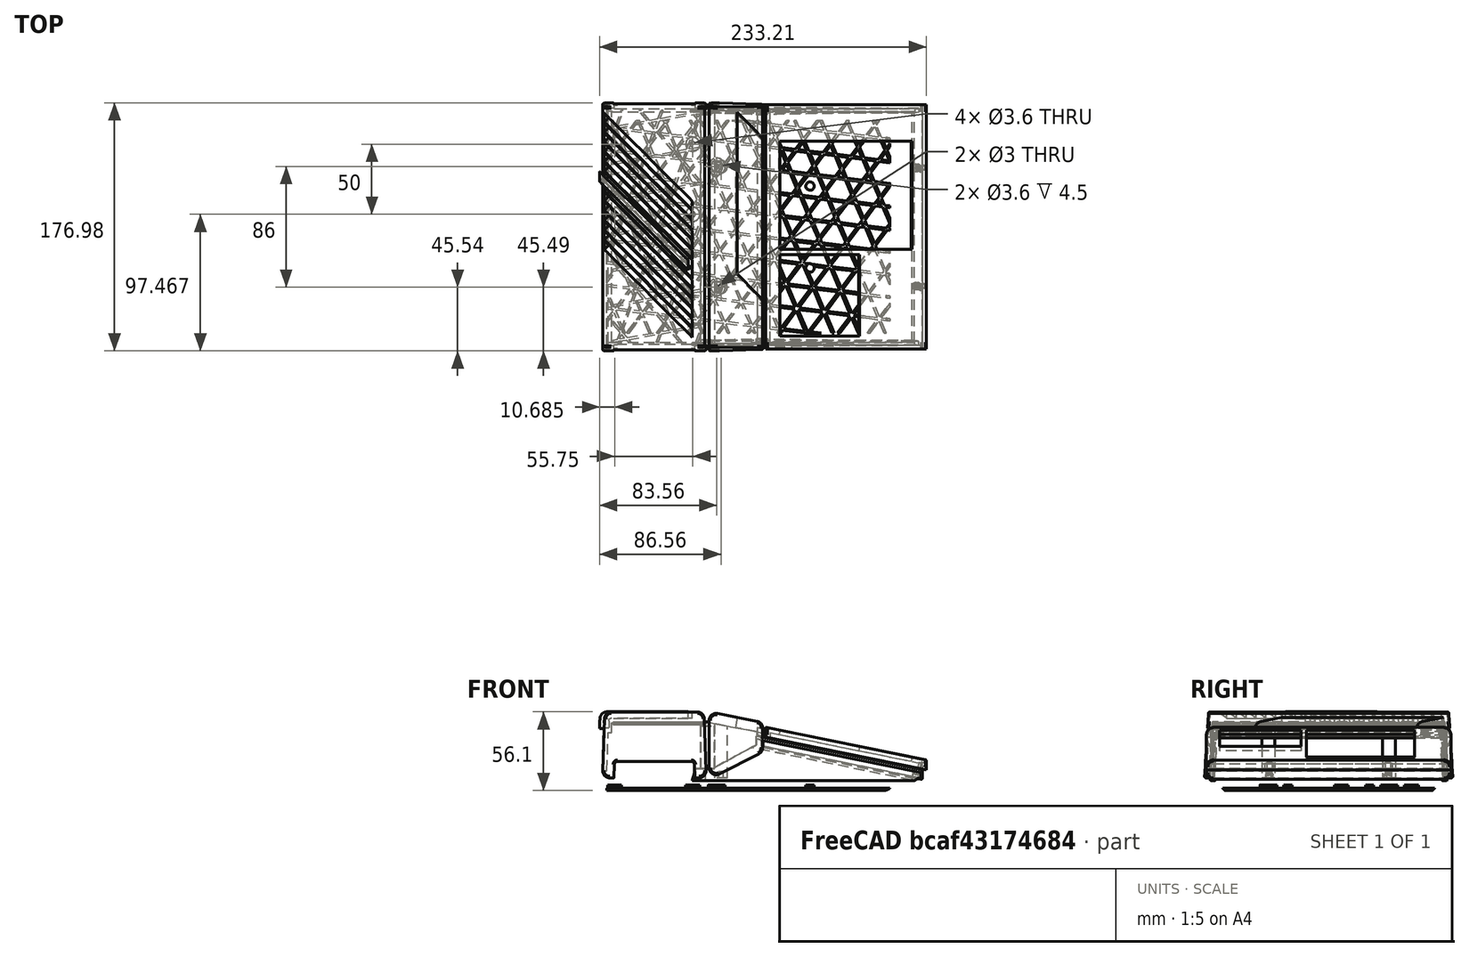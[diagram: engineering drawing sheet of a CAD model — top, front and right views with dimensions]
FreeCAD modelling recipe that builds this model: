
FCSTD DOCUMENT  (FreeCAD 0.20R29177 +426 (Git))
Label: SidecarXE85-case
License: All rights reserved
LicenseURL: http://en.wikipedia.org/wiki/All_rights_reserved
objects: Part::FeaturePython×61, Sketcher::SketchObject×58, PartDesign::Plane×37, PartDesign::Pad×26, PartDesign::Pocket×26, PartDesign::Body×23, Surface::GeomFillSurface×22, PartDesign::FeatureBase×18, PartDesign::Line×12, Part::Part2DObjectPython×10, Part::Compound×8, Surface::Sections×8, PartDesign::Fillet×7, PartDesign::LinearPattern×6, PartDesign::ShapeBinder×5, Surface::Filling×3, PartDesign::Draft×2, Part::Feature×2, Part::Offset×2, Part::Fuse×2, +13 more types
note: 410 computed .brp shape members not serialized (recipe doc carries the construction recipe); baked Part::Feature solids carry a one-line shape summary decoded from their .brp

FEATURE [Sketcher::SketchObject] Sketch  label="SketchBack"
  FullyConstrained = true
  MapMode = 5
  Placement = pos=(0,0,0) rot=(1,0,0;1.5708rad)
  Support = -> [XZ_Plane]
  sketch-geometry (4):
    g0: LineSegment StartX=0 StartY=12 StartZ=0 EndX=1.5 EndY=59 EndZ=0
    g1: LineSegment StartX=1.5 StartY=59 StartZ=0 EndX=72.5 EndY=59 EndZ=0
    g2: LineSegment StartX=72.5 StartY=59 StartZ=0 EndX=74 EndY=12 EndZ=0
    g3: LineSegment StartX=74 StartY=12 StartZ=0 EndX=0 EndY=12 EndZ=0
  constraints (12):
    c: PointOnObject(g0,g-2)
    c: Coincident(g0,g1)
    c: Horizontal(g1)
    c: Coincident(g1,g2)
    c: Coincident(g2,g3)
    c: Coincident(g3,g0)
    c: Horizontal(g3)
    c: DistanceX(g1,g1) = 71
    c: DistanceY(g0,g0) = 47
    c: DistanceY(g-1,g0) = 12
    c: DistanceX(g0,g0) = 1.5
    c: DistanceX(g1,g2) = 1.5
FEATURE [PartDesign::Pad] Pad  label="ExtrudeBack"
  Direction = (0,-1,-2e-16)
  Length = 177.1
  Length2 = 10
  Placement = pos=(0,0,0) rot=(1,0,0;1.5708rad)
  Profile = -> Sketch
  ReferenceAxis = -> Sketch [N_Axis]
  Type = 0
  expr: Length = <<Params>>.Width + 2.7
FEATURE [Spreadsheet::Sheet] Spreadsheet  label="Params"
  cells = A1=Width; B1(Width)=174.4; A2=BigFillet; B2(BigFillet)=5; A3=Walls; B3(Walls)=3
FEATURE [PartDesign::Fillet] Fillet  label="BigFilletBack"
  Base = -> Pad [Edge1,Edge2,Edge5,Edge8]
  BaseFeature = -> Pad
  Placement = pos=(0,0,0) rot=(1,0,0;1.5708rad)
  Radius = 5
  SupportTransform = false
  UseAllEdges = false
  expr: Radius = <<Params>>.BigFillet
FEATURE [Sketcher::SketchObject] Sketch001  label="SketchMiddle"
  FullyConstrained = true
  MapMode = 5
  Placement = pos=(0,0,0) rot=(1,0,0;1.5708rad)
  Support = -> [XZ_Plane001]
  sketch-geometry (4):
    g0: LineSegment StartX=76 StartY=11 StartZ=0 EndX=76 EndY=59 EndZ=0
    g1: LineSegment StartX=76 StartY=59 StartZ=0 EndX=114.286 EndY=51.5741 EndZ=0
    g2: LineSegment StartX=114.286 StartY=51.5741 StartZ=0 EndX=114.286 EndY=30.5741 EndZ=0
    g3: LineSegment StartX=114.286 StartY=30.5741 StartZ=0 EndX=76 EndY=11 EndZ=0
  constraints (12):
    c: Vertical(g0)
    c: Coincident(g0,g1)
    c: Coincident(g1,g2)
    c: Vertical(g2)
    c: Coincident(g2,g3)
    c: Coincident(g3,g0)
    c: Distance(g0,g1) = 39
    c: DistanceY(g2,g1) = 21
    c: Distance(g2,g0) = 43
    c: DistanceY(g0,g0) = 48
    c: DistanceY(g-1,g0) = 11
    c: DistanceX(g-1,g0) = 76
FEATURE [PartDesign::Pad] Pad001  label="ExtrudeMiddle"
  Direction = (0,-1,-2e-16)
  Length = 177.1
  Length2 = 10
  Placement = pos=(0,0,0) rot=(1,0,0;1.5708rad)
  Profile = -> Sketch001
  ReferenceAxis = -> Sketch001 [N_Axis]
  Type = 0
  expr: Length = <<Params>>.Width + 2.7
FEATURE [PartDesign::Fillet] Fillet001  label="BigFilletMiddle"
  Base = -> Pad001 [Edge1,Edge2,Edge5,Edge8]
  BaseFeature = -> Pad001
  Placement = pos=(0,0,0) rot=(1,0,0;1.5708rad)
  Radius = 5
  SupportTransform = false
  UseAllEdges = false
  expr: Radius = <<Params>>.BigFillet
FEATURE [Sketcher::SketchObject] Sketch002  label="SketchKeyboardTop"
  FullyConstrained = true
  MapMode = 5
  Placement = pos=(0,0,0) rot=(1,0,0;1.5708rad)
  Support = -> [XZ_Plane002]
  sketch-geometry (4):
    g0: LineSegment StartX=116.5 StartY=41 StartZ=0 EndX=116.5 EndY=48 EndZ=0
    g1: LineSegment StartX=116.5 StartY=48 StartZ=0 EndX=231.151 EndY=24.674 EndZ=0
    g2: LineSegment StartX=231.151 StartY=24.674 StartZ=0 EndX=231.151 EndY=17.674 EndZ=0
    g3: LineSegment StartX=231.151 StartY=17.674 StartZ=0 EndX=116.5 EndY=41 EndZ=0
  constraints (12):
    c: Vertical(g0)
    c: Coincident(g0,g1)
    c: Coincident(g1,g2)
    c: Vertical(g2)
    c: Coincident(g2,g3)
    c: Coincident(g3,g0)
    c: Parallel(g1,g3)
    c: Angle(g1,g-1) = 0.200713
    c: DistanceY(g0,g0) = 7
    c: Distance(g0,g2) = 117
    c: DistanceX(g-1,g0) = 116.5
    c: DistanceY(g-1,g0) = 41
FEATURE [PartDesign::Pad] Pad002  label="ExtrudeKeyboardTop"
  Direction = (0,-1,-2e-16)
  Length = 174.4
  Length2 = 10
  Placement = pos=(0,0,0) rot=(1,0,0;1.5708rad)
  Profile = -> Sketch002
  ReferenceAxis = -> Sketch002 [N_Axis]
  Type = 0
  expr: Length = <<Params>>.Width
FEATURE [PartDesign::Fillet] Fillet002  label="BigFilletKeyboardTop"
  Base = -> Pad002 [Edge7,Edge6]
  BaseFeature = -> Pad002
  Placement = pos=(0,0,0) rot=(1,0,0;1.5708rad)
  Radius = 5
  SupportTransform = false
  UseAllEdges = false
  expr: Radius = <<Params>>.BigFillet
FEATURE [PartDesign::Line] DatumLine  label="BottomLeftDatumLine"
  AttacherType = Attacher::AttachEngineLine
  Length = 20
  MapMode = 29
  Placement = pos=(0,-177.1,12) rot=(0.57735,-0.57735,-0.57735;2.0944rad)
  ResizeMode = 0
  Support = -> [Fillet]
FEATURE [PartDesign::Line] DatumLine001  label="BottomRightDatumLine"
  AttacherType = Attacher::AttachEngineLine
  Length = 20
  MapMode = 29
  Placement = pos=(0,2.7e-15,12) rot=(0.57735,-0.57735,-0.57735;2.0944rad)
  ResizeMode = 0
  Support = -> [Fillet]
FEATURE [PartDesign::Line] DatumLine002  label="TopLeftDatumLine"
  AttacherType = Attacher::AttachEngineLine
  AttachmentOffset = pos=(2.7,0,0) rot=(0,0,1;0rad)
  Length = 20
  MapMode = 29
  Placement = pos=(0,-174.4,59) rot=(0.57735,0.57735,0.57735;2.0944rad)
  ResizeMode = 0
  Support = -> [Fillet]
FEATURE [PartDesign::Line] DatumLine003  label="TopRightDatumLine"
  AttacherType = Attacher::AttachEngineLine
  AttachmentOffset = pos=(-2.7,0,0) rot=(0,0,1;0rad)
  Length = 20
  MapMode = 29
  Placement = pos=(0,-2.7,59) rot=(0.57735,0.57735,0.57735;2.0944rad)
  ResizeMode = 0
  Support = -> [Fillet]
FEATURE [PartDesign::Plane] DatumPlane  label="LeftCutDatumPlane"
  Length = 287.424
  MapMode = 13
  Placement = pos=(0.333333,-175.3,43.3333) rot=(0,0.727101,0.68653;3.14159rad)
  ResizeMode = 0
  Support = -> [DatumLine002,DatumLine]
  Width = 126.721
FEATURE [PartDesign::Plane] DatumPlane001  label="RightCutDatumPlane"
  Length = 287.424
  MapMode = 13
  Placement = pos=(0.333333,-1.8,43.3333) rot=(0,0.68653,0.727101;3.14159rad)
  ResizeMode = 0
  Support = -> [DatumLine003,DatumLine001]
  Width = 126.721
FEATURE [PartDesign::Draft] Draft  label="DraftBack"
  Angle = 3.5
  Base = -> Fillet [Face5,Face2]
  BaseFeature = -> Fillet
  NeutralPlane = -> Fillet [Face6]
  Placement = pos=(0,0,0) rot=(1,0,0;1.5708rad)
  Reversed = true
  SupportTransform = false
FEATURE [PartDesign::Plane] DatumPlane002  label="BottomDatumPlane"
  Length = 60
  MapMode = 5
  Placement = pos=(0,2.7e-15,12) rot=(1,0,0;3.14159rad)
  ResizeMode = 0
  Support = -> [Draft]
  Width = 60
FEATURE [PartDesign::Draft] Draft001  label="DraftMiddle"
  Angle = 3.5
  Base = -> Fillet001 [Face2,Face5]
  BaseFeature = -> Fillet001
  NeutralPlane = -> DatumPlane002
  Placement = pos=(0,0,0) rot=(1,0,0;1.5708rad)
  Reversed = true
  SupportTransform = false
FEATURE [PartDesign::Thickness] Thickness
  Base = -> Fillet002 [Face7]
  BaseFeature = -> Fillet002
  Intersection = false
  Join = 1
  Mode = 0
  Reversed = true
  SupportTransform = false
  Value = 3
  expr: Value = <<Params>>.Walls
FEATURE [Sketcher::SketchObject] Sketch003  label="BackCutSchema"
  ExternalGeometry = -> [Draft]
  FullyConstrained = true
  MapMode = 5
  Placement = pos=(-0.382589,0,0.0122103) rot=(-0.695738,0,0.718296;3.14159rad)
  Support = -> [Draft]
  expr: Constraints[4] = 90 - 3.5
  expr: Constraints[5] = 90 - 3.5
  expr: Constraints[6] = <<Params>>.Width - 2 * <<Params>>.Walls - 4
  sketch-geometry (6):
    g0: LineSegment StartX=0 StartY=3.22001 StartZ=0 EndX=-51.1749 EndY=6.35 EndZ=0
    g1: LineSegment StartX=-51.1749 StartY=170.75 StartZ=0 EndX=0 EndY=173.88 EndZ=0
    g2: LineSegment StartX=0 StartY=173.88 StartZ=0 EndX=0 EndY=3.22001 EndZ=0
    g3: LineSegment StartX=-54.1749 StartY=174.521 StartZ=0 EndX=-51.1749 EndY=170.75 EndZ=0
    g4: LineSegment StartX=-51.1749 StartY=6.35 StartZ=0 EndX=-54.1749 EndY=2.57859 EndZ=0
    g5: LineSegment StartX=-51.1749 StartY=170.75 StartZ=0 EndX=-51.1749 EndY=6.35 EndZ=0
  constraints (16):
    c: PointOnObject(g0,g-2)
    c: PointOnObject(g1,g-2)
    c: Coincident(g1,g2)
    c: Coincident(g2,g0)
    c: Angle(g1,g2) = 1.50971
    c: Angle(g2,g0) = 1.50971
    c: DistanceY(g0,g1) = 164.4
    c: Coincident(g3,g-3)
    c: Coincident(g3,g1)
    c: Coincident(g4,g0)
    c: Coincident(g4,g-4)
    c: Equal(g3,g4)
    c: Coincident(g5,g1)
    c: Coincident(g5,g0)
    c: Vertical(g5)
    c: DistanceX(g3,g1) = 3
FEATURE [PartDesign::Pocket] Pocket  label="BackCut"
  BaseFeature = -> Draft
  Direction = (1,0,0)
  Length = 0
  Length2 = 5
  Placement = pos=(0,0,0) rot=(1,0,0;1.5708rad)
  Profile = -> Sketch003
  ReferenceAxis = -> Sketch003 [N_Axis]
  Type = 3
  UpToFace = -> Draft [Face10]
  UseCustomVector = true
FEATURE [PartDesign::Plane] DatumPlane003  label="BackVerticalDatumPlane"
  Length = 329.861
  MapMode = 13
  Placement = pos=(1.77559,-2.74097,9.71983) rot=(0.058644,0.617116,0.784684;2.99273rad)
  ResizeMode = 0
  Support = -> [Pocket,Z_Axis]
  Width = 180.015
FEATURE [Sketcher::SketchObject] Sketch004  label="KeyboardHoleSketch"
  ExternalGeometry = -> [Thickness]
  FullyConstrained = true
  MapMode = 5
  Placement = pos=(14.0081,0,68.8522) rot=(0,1,0;0.200713rad)
  Support = -> [Thickness]
  expr: Constraints[16] = 19.05 * 4 + 1
  expr: Constraints[17] = 19.05 * 3 + 1
  expr: Constraints[18] = 19.05 / 4 - 1
  expr: Constraints[20] = 19.05 * 5 + 1
  expr: Constraints[21] = 19.05 * 3 + 1
  sketch-geometry (10):
    g0: LineSegment StartX=114.742 StartY=-25.94 StartZ=0 EndX=210.992 EndY=-25.94 EndZ=0
    g1: LineSegment StartX=210.992 StartY=-25.94 StartZ=0 EndX=210.992 EndY=-103.14 EndZ=0
    g2: LineSegment StartX=210.992 StartY=-103.14 StartZ=0 EndX=114.742 EndY=-103.14 EndZ=0
    g3: LineSegment StartX=114.742 StartY=-103.14 StartZ=0 EndX=114.742 EndY=-25.94 EndZ=0
    g4: LineSegment StartX=114.742 StartY=-106.902 StartZ=0 EndX=172.892 EndY=-106.902 EndZ=0
    g5: LineSegment StartX=172.892 StartY=-106.902 StartZ=0 EndX=172.892 EndY=-165.052 EndZ=0
    g6: LineSegment StartX=172.892 StartY=-165.052 StartZ=0 EndX=114.742 EndY=-165.052 EndZ=0
    g7: LineSegment StartX=114.742 StartY=-165.052 StartZ=0 EndX=114.742 EndY=-106.902 EndZ=0
    g8: LineSegment StartX=114.742 StartY=-25.94 StartZ=0 EndX=114.742 EndY=-5 EndZ=0
    g9: LineSegment StartX=114.742 StartY=-165.052 StartZ=0 EndX=114.742 EndY=-169.4 EndZ=0
  constraints (30):
    c: Coincident(g0,g1)
    c: Coincident(g1,g2)
    c: Coincident(g2,g3)
    c: Coincident(g3,g0)
    c: Horizontal(g0)
    c: Horizontal(g2)
    c: Vertical(g1)
    c: Vertical(g3)
    c: Coincident(g4,g5)
    c: Coincident(g5,g6)
    c: Coincident(g6,g7)
    c: Coincident(g7,g4)
    c: Horizontal(g4)
    c: Horizontal(g6)
    c: Vertical(g5)
    c: Vertical(g7)
    c: DistanceY(g3,g3) = 77.2
    c: DistanceY(g7,g7) = 58.15
    c: DistanceY(g4,g2) = 3.7625
    c: PointOnObject(g4,g3)
    c: DistanceX(g0,g0) = 96.25
    c: DistanceX(g4,g4) = 58.15
    c: Coincident(g8,g0)
    c: PointOnObject(g8,g-4)
    c: Vertical(g8)
    c: Coincident(g9,g6)
    c: PointOnObject(g9,g-5)
    c: Vertical(g9)
    c: DistanceY(g0,g8) = 20.94
    c: DistanceX(g0,g-4) = 10.6
FEATURE [PartDesign::Pocket] Pocket001  label="KeyHoles"
  BaseFeature = -> Thickness
  Direction = (-0.199368,0,-0.979925)
  Length = 5
  Length2 = 5
  Profile = -> Sketch004
  ReferenceAxis = -> Sketch004 [N_Axis]
  Type = 0
FEATURE [Sketcher::SketchObject] Sketch005  label="MiddlePocketSketch"
  ExternalGeometry = -> [Draft001]
  FullyConstrained = true
  MapMode = 5
  Placement = pos=(76,0,0) rot=(0.707107,0,-0.707107;3.14159rad)
  Support = -> [Draft001]
  expr: Constraints[15] = <<Params>>.Walls / cos(10)
  sketch-geometry (6):
    g0: LineSegment StartX=-1.54556 StartY=174.608 StartZ=0 EndX=-51.5456 EndY=171.55 EndZ=0
    g1: LineSegment StartX=-51.5456 StartY=171.55 StartZ=0 EndX=-51.5456 EndY=5.5501 EndZ=0
    g2: LineSegment StartX=-51.5456 StartY=5.5501 StartZ=0 EndX=-1.54556 EndY=2.49197 EndZ=0
    g3: LineSegment StartX=-1.54556 StartY=2.49197 StartZ=0 EndX=-1.54556 EndY=174.608 EndZ=0
    g4: LineSegment StartX=-57.8456 StartY=174.296 StartZ=0 EndX=-51.5456 EndY=171.55 EndZ=0
    g5: LineSegment StartX=-51.5456 StartY=5.5501 StartZ=0 EndX=-57.8456 EndY=2.80403 EndZ=0
  constraints (16):
    c: Coincident(g0,g1)
    c: Vertical(g1)
    c: Coincident(g1,g2)
    c: Coincident(g2,g3)
    c: Coincident(g3,g0)
    c: Vertical(g3)
    c: Parallel(g0,g-3)
    c: Parallel(g-4,g2)
    c: Coincident(g4,g-5)
    c: Coincident(g4,g0)
    c: Coincident(g5,g1)
    c: Coincident(g5,g-5)
    c: Equal(g4,g5)
    c: DistanceX(g4,g0) = 6.3
    c: DistanceX(g0,g0) = 50
    c: DistanceY(g0,g-3) = 3.04628
FEATURE [PartDesign::Pocket] Pocket002  label="MiddlePocket"
  AlongSketchNormal = false
  BaseFeature = -> Draft001
  Direction = (-0.98,0,0.19)
  Length = 0
  Length2 = 5
  Placement = pos=(0,0,0) rot=(1,0,0;1.5708rad)
  Profile = -> Sketch005
  ReferenceAxis = -> Sketch005 [N_Axis]
  Reversed = true
  Type = 3
  UpToFace = -> Draft001 [Face10]
  UseCustomVector = true
FEATURE [PartDesign::Body] Body001  label="Middle"
  Group = -> [Sketch001,Pad001,Fillet001,DatumPlane002,Draft001,Sketch005,Pocket002]
  Origin = -> Origin001
  Tip = -> Pocket002
FEATURE [PartDesign::Plane] DatumPlane004  label="SevenMmBelowTopDatumPlane"
  AttachmentOffset = pos=(0,0,-7) rot=(0,0,1;0rad)
  Length = 301.649
  MapMode = 5
  Placement = pos=(0,1.29e-14,58.161) rot=(1,0,0;3.14159rad)
  ResizeMode = 0
  Support = -> [Pocket]
  Width = 247.533
FEATURE [PartDesign::Plane] DatumPlane007
  AttachmentOffset = pos=(0,0,-1.35) rot=(0,0,1;0rad)
  Length = 311.586
  MapMode = 5
  Placement = pos=(13.739,0,67.5293) rot=(0,1,0;0.200713rad)
  ResizeMode = 0
  Support = -> [Pocket001]
  Width = 245.423
FEATURE [PartDesign::Line] DatumLine007
  AttacherType = Attacher::AttachEngineLine
  Length = 20
  MapMode = 29
  Placement = pos=(116.5,0,48) rot=(1,0,0;1.5708rad)
  ResizeMode = 0
  Support = -> [Pocket001]
FEATURE [PartDesign::Line] DatumLine008
  AttacherType = Attacher::AttachEngineLine
  Length = 20
  MapMode = 29
  Placement = pos=(14.0081,-169.4,68.8522) rot=(0.612272,0.612272,0.500247;2.2139rad)
  ResizeMode = 0
  Support = -> [Pocket001]
FEATURE [PartDesign::Line] DatumLine009
  AttacherType = Attacher::AttachEngineLine
  Length = 20
  MapMode = 29
  Placement = pos=(14.0081,-5,68.8522) rot=(0.612272,0.612272,0.500247;2.2139rad)
  ResizeMode = 0
  Support = -> [Pocket001]
FEATURE [Sketcher::SketchObject] Sketch009  label="ConnectionKeyboardMiddleSketch"
  ExternalGeometry = -> [DatumLine009,DatumLine008,DatumLine007]
  FullyConstrained = true
  MapMode = 5
  Placement = pos=(13.739,0,67.5293) rot=(0,1,0;0.200713rad)
  Support = -> [DatumPlane007]
  expr: Constraints[9] = <<Params>>.Width - 6
  sketch-geometry (7):
    g0: LineSegment StartX=106.592 StartY=-3 StartZ=0 EndX=98.5916 EndY=-3 EndZ=0
    g1: LineSegment StartX=98.5916 StartY=-3 StartZ=0 EndX=98.5916 EndY=-171.4 EndZ=0
    g2: LineSegment StartX=98.5916 StartY=-171.4 StartZ=0 EndX=106.592 EndY=-171.4 EndZ=0
    g3: LineSegment StartX=106.592 StartY=-171.4 StartZ=0 EndX=106.592 EndY=-3 EndZ=0
    g4: GeomPoint X=104.592 Y=-169.4 Z=0
    g5: LineSegment StartX=104.592 StartY=-169.4 StartZ=0 EndX=106.592 EndY=-171.4 EndZ=0
    g6: LineSegment StartX=104.592 StartY=-5 StartZ=0 EndX=106.592 EndY=-3 EndZ=0
  constraints (19):
    c: Coincident(g0,g1)
    c: Coincident(g1,g2)
    c: Coincident(g2,g3)
    c: Coincident(g3,g0)
    c: Horizontal(g0)
    c: Horizontal(g2)
    c: Vertical(g1)
    c: Vertical(g3)
    c: DistanceX(g0,g0) = 8
    c: DistanceY(g3,g3) = 168.4
    c: PointOnObject(g4,g-5)
    c: PointOnObject(g4,g-4)
    c: Coincident(g5,g4)
    c: Coincident(g5,g2)
    c: Coincident(g6,g0)
    c: Equal(g5,g6)
    c: PointOnObject(g6,g-3)
    c: PointOnObject(g6,g-5)
    c: DistanceX(g4,g2) = 2
FEATURE [PartDesign::Pad] Pad006  label="ConnectionKeyboardMiddle"
  BaseFeature = -> Pocket001
  Direction = (0,0,1)
  Length = 5.5
  Length2 = 10
  Profile = -> Sketch009
  ReferenceAxis = -> Sketch009 [N_Axis]
  Reversed = true
  Type = 0
  UseCustomVector = true
FEATURE [PartDesign::Body] Body002  label="KeyboardTop"
  Group = -> [Sketch002,Pad002,Fillet002,Thickness,Sketch004,Pocket001,DatumPlane007,DatumLine007,DatumLine008,DatumLine009,Sketch009,Pad006]
  Origin = -> Origin002
  Placement = pos=(0,-1.35,0) rot=(0,0,1;0rad)
  Tip = -> Pad006
FEATURE [PartDesign::Plane] DatumPlane008
  Length = 119.414
  MapMode = 5
  Placement = pos=(-0.382589,0,0.0122103) rot=(-0.695738,0,0.718296;3.14159rad)
  ResizeMode = 0
  Support = -> [Pad]
  Width = 229.321
FEATURE [Sketcher::SketchObject] Sketch013
  FullyConstrained = false
  MapMode = 5
  Placement = pos=(6.46926,-2e-15,0) rot=(0.57735,-0.57735,-0.57735;2.0944rad)
  sketch-geometry (4):
    g0: LineSegment StartX=170.75 StartY=54.1595 StartZ=0 EndX=171.362 EndY=44.1595 EndZ=0
    g1: LineSegment StartX=171.362 StartY=44.1595 StartZ=0 EndX=5.73806 EndY=44.1595 EndZ=0
    g2: LineSegment StartX=5.73806 StartY=44.1595 StartZ=0 EndX=6.35 EndY=54.1595 EndZ=0
    g3: LineSegment StartX=6.35 StartY=54.1595 StartZ=0 EndX=170.75 EndY=54.1595 EndZ=0
  constraints (6):
    c: Coincident(g0,g1)
    c: Horizontal(g1)
    c: Coincident(g1,g2)
    c: Coincident(g2,g3)
    c: Coincident(g3,g0)
    c: DistanceY(g0,g0) = 10
FEATURE [PartDesign::Plane] DatumPlane010
  AttachmentOffset = pos=(0,0,62) rot=(0,0,1;0rad)
  Length = 228.09
  MapMode = 5
  Placement = pos=(62,-1.38e-14,1.38e-14) rot=(0.57735,0.57735,0.57735;2.0944rad)
  ResizeMode = 0
  Support = -> [YZ_Plane]
  Width = 110.055
FEATURE [Part::Feature] Projection_Object  label="Projection Object"
  Placement = pos=(0,-1,0) rot=(0,0,1;0rad)
  shape: bbox 73.68 x 73.68 x 47 mm, 0 faces, 0 solids (baked)
FEATURE [PartDesign::ShapeBinder] ShapeBinder  label="SideProjectionBinder1"
  Placement = pos=(0,-1,0) rot=(0,0,1;0rad)
  Support = -> [Projection_Object]
  TraceSupport = false
FEATURE [Part::Feature] Projection_Object001  label="Projection Object001"
  shape: bbox 67.49 x 67.49 x 41.84 mm, 0 faces, 0 solids (baked)
FEATURE [PartDesign::ShapeBinder] ShapeBinder003  label="SideProjectionBinder2"
  Support = -> [Projection_Object001]
  TraceSupport = false
FEATURE [PartDesign::Body] Body003  label="VentIntermediary"
  Group = -> [ShapeBinder,ShapeBinder003]
  Origin = -> Origin004
FEATURE [PartDesign::Plane] DatumPlane017
  AttachmentOffset = pos=(0,0,70) rot=(0,0,1;0rad)
  Length = 228.09
  MapMode = 5
  Placement = pos=(70,-1.55e-14,1.55e-14) rot=(0.57735,0.57735,0.57735;2.0944rad)
  ResizeMode = 0
  Support = -> [YZ_Plane]
  Width = 110.055
FEATURE [Sketcher::SketchObject] Sketch023
  FullyConstrained = false
  MapMode = 5
  Placement = pos=(70,-1.55e-14,1.55e-14) rot=(0.57735,0.57735,0.57735;2.0944rad)
  Support = -> [DatumPlane017]
  expr: Constraints[11] = <<Params>>.Walls
  expr: Constraints[14] = <<Params>>.Walls
  expr: Constraints[15] = <<Params>>.Walls
  sketch-geometry (8):
    g0: LineSegment StartX=-173.764 StartY=18.5595 StartZ=0 EndX=-171.721 EndY=51.9595 EndZ=0
    g1: LineSegment StartX=-171.721 StartY=51.9595 StartZ=0 EndX=-5.37859 EndY=51.9595 EndZ=0
    g2: LineSegment StartX=-5.37859 StartY=51.9595 StartZ=0 EndX=-3.33575 EndY=18.5595 EndZ=0
    g3: LineSegment StartX=-3.33575 StartY=18.5595 StartZ=0 EndX=-6.33575 EndY=18.5595 EndZ=0
    g4: LineSegment StartX=-6.33575 StartY=18.5595 StartZ=0 EndX=-8.1951 EndY=48.9595 EndZ=0
    g5: LineSegment StartX=-8.1951 StartY=48.9595 StartZ=0 EndX=-168.905 EndY=48.9595 EndZ=0
    g6: LineSegment StartX=-168.905 StartY=48.9595 StartZ=0 EndX=-170.764 EndY=18.5595 EndZ=0
    g7: LineSegment StartX=-170.764 StartY=18.5595 StartZ=0 EndX=-173.764 EndY=18.5595 EndZ=0
  constraints (17):
    c: Coincident(g0,g1)
    c: Horizontal(g1)
    c: Coincident(g1,g2)
    c: Coincident(g2,g3)
    c: Horizontal(g3)
    c: Coincident(g3,g4)
    c: Coincident(g4,g5)
    c: Horizontal(g5)
    c: Coincident(g5,g6)
    c: Coincident(g6,g7)
    c: Coincident(g7,g0)
    c: DistanceY(g5,g0) = 3
    c: Parallel(g0,g6)
    c: Parallel(g2,g4)
    c: DistanceX(g0,g6) = 3
    c: DistanceX(g3,g2) = 3
    c: Tangent(g7,g3)
FEATURE [PartDesign::Pad] Pad011  label="ConnectionBackMiddle"
  BaseFeature = -> Pocket
  Direction = (1,-1e-16,1e-16)
  Length = 10
  Length2 = 10
  Placement = pos=(0,0,0) rot=(1,0,0;1.5708rad)
  Profile = -> Sketch023
  ReferenceAxis = -> Sketch023 [N_Axis]
  Type = 0
FEATURE [Sketcher::SketchObject] Sketch010  label="BackWallSketch"
  ExternalGeometry = -> [Pad011]
  FullyConstrained = true
  MapMode = 5
  Placement = pos=(-0.382589,0,0.0122103) rot=(-0.695738,0,0.718296;3.14159rad)
  Support = -> [DatumPlane008]
  sketch-geometry (4):
    g0: LineSegment StartX=-51.1749 StartY=170.75 StartZ=0 EndX=-17.156 EndY=172.831 EndZ=0
    g1: LineSegment StartX=-17.156 StartY=172.831 StartZ=0 EndX=-17.156 EndY=4.26932 EndZ=0
    g2: LineSegment StartX=-17.156 StartY=4.26932 StartZ=0 EndX=-51.1749 EndY=6.35 EndZ=0
    g3: LineSegment StartX=-51.1749 StartY=6.35 StartZ=0 EndX=-51.1749 EndY=170.75 EndZ=0
  constraints (8):
    c: Coincident(g0,g1)
    c: Coincident(g1,g2)
    c: Coincident(g2,g3)
    c: Coincident(g3,g0)
    c: Coincident(g0,g-3)
    c: Coincident(g-3,g0)
    c: Coincident(g2,g-4)
    c: Coincident(g1,g-4)
FEATURE [PartDesign::Pad] Pad007  label="BackWall"
  BaseFeature = -> Pad011
  Direction = (-1,0,0)
  Length = 3
  Length2 = 10
  Placement = pos=(0,0,0) rot=(1,0,0;1.5708rad)
  Profile = -> Sketch010
  ReferenceAxis = -> Sketch010 [N_Axis]
  Reversed = true
  Type = 0
  UseCustomVector = true
  expr: Length = <<Params>>.Walls
FEATURE [PartDesign::Boolean] Boolean  label="MiddleKeyboardBool"
  BaseFeature = -> Pad007
  Group = -> [Body001,Body002]
  Type = 0
FEATURE [Sketcher::SketchObject] Sketch011  label="ConsoleKeyHoleSketch"
  ExternalGeometry = -> [Boolean]
  FullyConstrained = true
  MapMode = 5
  Placement = pos=(13.784,-1.59e-14,71.0672) rot=(0,1,0;0.191578rad)
  Support = -> [Boolean]
  sketch-geometry (4):
    g0: LineSegment StartX=104.379 StartY=-27.29 StartZ=0 EndX=83.8786 EndY=-6.79 EndZ=0
    g1: LineSegment StartX=83.8786 StartY=-6.79 StartZ=0 EndX=83.8786 EndY=-122.09 EndZ=0
    g2: LineSegment StartX=83.8786 StartY=-122.09 StartZ=0 EndX=104.379 EndY=-142.59 EndZ=0
    g3: LineSegment StartX=104.379 StartY=-142.59 StartZ=0 EndX=104.379 EndY=-27.29 EndZ=0
  constraints (12):
    c: Coincident(g1,g2)
    c: Coincident(g0,g1)
    c: Coincident(g2,g3)
    c: Vertical(g1)
    c: Vertical(g3)
    c: Angle(g1,g0) = 0.785398
    c: Angle(g3,g2) = 0.785398
    c: DistanceX(g0,g0) = 20.5
    c: DistanceY(g1,g0) = 115.3
    c: Coincident(g0,g3)
    c: PointOnObject(g0,g-3)
    c: DistanceX(g0,g-3) = 11
FEATURE [PartDesign::Pocket] Pocket003  label="ConsoleKeyHole"
  BaseFeature = -> Boolean
  Direction = (-0.190408,2e-16,-0.981705)
  Length = 12
  Length2 = 5
  Profile = -> Sketch011
  ReferenceAxis = -> Sketch011 [N_Axis]
  Type = 0
FEATURE [PartDesign::Pad] Pad009  label="InsideBackVentBump"
  BaseFeature = -> Pocket003
  Direction = (-1,0,0)
  Length = 4
  Length2 = 10
  Profile = -> Sketch013
  ReferenceAxis = -> Sketch013 [N_Axis]
  Type = 0
FEATURE [PartDesign::Line] DatumLine019
  AttacherType = Attacher::AttachEngineLine
  Length = 20
  MapMode = 29
  Placement = pos=(56.9285,-173.59,69.3916) rot=(0.698753,0.658583,0.279309;2.56539rad)
  ResizeMode = 0
  Support = -> [Pad009]
FEATURE [PartDesign::Line] DatumLine024
  AttacherType = Attacher::AttachEngineLine
  Length = 20
  MapMode = 29
  Placement = pos=(206.756,-27.29,-42.065) rot=(0.705321,-0.705321,-0.071022;2.99979rad)
  ResizeMode = 0
  Support = -> [Boolean]
FEATURE [PartDesign::Line] DatumLine025
  AttacherType = Attacher::AttachEngineLine
  Length = 20
  MapMode = 29
  Placement = pos=(119.5,0,40.3896) rot=(0,0.707107,0.707107;3.14159rad)
  ResizeMode = 0
  Support = -> [Boolean]
FEATURE [PartDesign::Line] DatumLine026
  AttacherType = Attacher::AttachEngineLine
  Length = 20
  MapMode = 46
  Placement = pos=(10.1621,-0.315568,17.0116) rot=(0,1,0;1.56847rad)
  ResizeMode = 0
  Support = -> [Pad009]
FEATURE [PartDesign::Plane] DatumPlane011
  Length = 287.573
  MapMode = 13
  Placement = pos=(29.6604,-1.16859,31.0085) rot=(1,7.1e-05,6.7e-05;1.63186rad)
  ResizeMode = 0
  Support = -> [DatumLine026,Pad009]
  Width = 127.569
FEATURE [Sketcher::SketchObject] Sketch018  label="JoystickOpening"
  ExternalGeometry = -> [Pad009]
  FullyConstrained = true
  MapMode = 5
  Placement = pos=(0,0,0) rot=(1,0,0;1.5708rad)
  Support = -> [XZ_Plane003]
  sketch-geometry (10):
    g0: LineSegment StartX=8.25 StartY=12 StartZ=0 EndX=8.56269 EndY=21.7143 EndZ=0
    g1: LineSegment StartX=10.5617 StartY=23.65 StartZ=0 EndX=63.4383 EndY=23.65 EndZ=0
    g2: LineSegment StartX=65.4373 StartY=21.7143 StartZ=0 EndX=65.75 EndY=12 EndZ=0
    g3: LineSegment StartX=65.75 StartY=12 StartZ=0 EndX=8.25 EndY=12 EndZ=0
    g4: LineSegment StartX=8.25 StartY=12 StartZ=0 EndX=65.375 EndY=23.65 EndZ=0
    g5: LineSegment StartX=8.625 StartY=23.65 StartZ=0 EndX=65.75 EndY=12 EndZ=0
    g6: ArcOfCircle CenterX=10.5617 CenterY=21.65 CenterZ=0 NormalX=0 NormalY=0 NormalZ=1 AngleXU=0 Radius=2 StartAngle=1.5708 EndAngle=3.10941
    g7: ArcOfCircle CenterX=63.4383 CenterY=21.65 CenterZ=0 NormalX=0 NormalY=0 NormalZ=1 AngleXU=0 Radius=2 StartAngle=0.0321777 EndAngle=1.5708
    g8: LineSegment StartX=5.16212 StartY=12 StartZ=0 EndX=8.25 EndY=12 EndZ=0
    g9: LineSegment StartX=65.75 StartY=12 StartZ=0 EndX=68.8379 EndY=12 EndZ=0
  constraints (26):
    c: Horizontal(g1)
    c: Coincident(g2,g3)
    c: Coincident(g3,g0)
    c: Horizontal(g3)
    c: DistanceX(g5,g4) = 56.75
    c: Coincident(g4,g0)
    c: Coincident(g5,g2)
    c: Equal(g4,g5)
    c: DistanceY(g0,g5) = 11.65
    c: DistanceX(g3,g3) = 57.5
    c: PointOnObject(g5,g0)
    c: PointOnObject(g5,g1)
    c: Tangent(g0,g6) = 1.5708
    c: Tangent(g1,g6) = 1.5708
    c: PointOnObject(g4,g1)
    c: PointOnObject(g4,g2)
    c: Tangent(g1,g7) = 1.5708
    c: Tangent(g2,g7) = 1.5708
    c: Radius(g6) = 2
    c: Radius(g7) = 2
    c: PointOnObject(g0,g-4)
    c: Coincident(g8,g-4)
    c: Coincident(g8,g0)
    c: Coincident(g9,g2)
    c: Coincident(g9,g-4)
    c: Equal(g8,g9)
FEATURE [PartDesign::Pocket] Pocket004  label="RightJoystickPorts"
  BaseFeature = -> Pad009
  Direction = (0,1,2e-16)
  Length = 5
  Length2 = 5
  Profile = -> Sketch018
  ReferenceAxis = -> Sketch018 [N_Axis]
  Reversed = true
  Type = 0
FEATURE [PartDesign::Plane] DatumPlane014
  AttachmentOffset = pos=(0,0,179.4) rot=(0,0,1;0rad)
  Length = 285.488
  MapMode = 3
  Placement = pos=(0,-179.4,3.98e-14) rot=(1,0,0;1.5708rad)
  ResizeMode = 0
  Support = -> [Pocket004]
  Width = 113.337
  expr: .AttachmentOffset.Base.z = <<Params>>.Width + 5
FEATURE [Sketcher::SketchObject] Sketch019
  ExternalGeometry = -> [Pocket004]
  FullyConstrained = true
  MapMode = 5
  Placement = pos=(0,-179.4,3.98e-14) rot=(1,0,0;1.5708rad)
  Support = -> [DatumPlane014]
  sketch-geometry (10):
    g0: LineSegment StartX=8.25 StartY=12 StartZ=0 EndX=8.56269 EndY=21.7143 EndZ=0
    g1: LineSegment StartX=10.5617 StartY=23.65 StartZ=0 EndX=63.4383 EndY=23.65 EndZ=0
    g2: LineSegment StartX=65.4373 StartY=21.7143 StartZ=0 EndX=65.75 EndY=12 EndZ=0
    g3: LineSegment StartX=65.75 StartY=12 StartZ=0 EndX=8.25 EndY=12 EndZ=0
    g4: LineSegment StartX=8.25 StartY=12 StartZ=0 EndX=65.375 EndY=23.65 EndZ=0
    g5: LineSegment StartX=8.625 StartY=23.65 StartZ=0 EndX=65.75 EndY=12 EndZ=0
    g6: ArcOfCircle CenterX=10.5617 CenterY=21.65 CenterZ=0 NormalX=0 NormalY=0 NormalZ=1 AngleXU=0 Radius=2 StartAngle=1.5708 EndAngle=3.10941
    g7: ArcOfCircle CenterX=63.4383 CenterY=21.65 CenterZ=0 NormalX=0 NormalY=0 NormalZ=1 AngleXU=0 Radius=2 StartAngle=0.0321777 EndAngle=1.5708
    g8: LineSegment StartX=5.16212 StartY=12 StartZ=0 EndX=8.25 EndY=12 EndZ=0
    g9: LineSegment StartX=65.75 StartY=12 StartZ=0 EndX=68.8379 EndY=12 EndZ=0
  constraints (26):
    c: Horizontal(g1)
    c: Coincident(g2,g3)
    c: Coincident(g3,g0)
    c: Coincident(g4,g0)
    c: Coincident(g5,g2)
    c: Equal(g4,g5)
    c: DistanceX(g5,g4) = 56.75
    c: DistanceX(g3,g3) = 57.5
    c: DistanceY(g0,g5) = 11.65
    c: PointOnObject(g5,g0)
    c: PointOnObject(g5,g1)
    c: Tangent(g0,g6) = 1.5708
    c: Tangent(g1,g6) = 1.5708
    c: PointOnObject(g4,g1)
    c: PointOnObject(g4,g2)
    c: Tangent(g1,g7) = 1.5708
    c: Tangent(g2,g7) = 1.5708
    c: Radius(g6) = 2
    c: Radius(g7) = 2
    c: Horizontal(g3)
    c: Coincident(g8,g-3)
    c: Coincident(g8,g0)
    c: Coincident(g9,g2)
    c: Coincident(g9,g-3)
    c: Equal(g8,g9)
    c: PointOnObject(g0,g-3)
FEATURE [PartDesign::Pocket] Pocket005  label="LeftJoystickPorts"
  BaseFeature = -> Pocket004
  Direction = (0,1,-2e-16)
  Length = 7
  Length2 = 5
  Profile = -> Sketch019
  ReferenceAxis = -> Sketch019 [N_Axis]
  Type = 0
FEATURE [PartDesign::Plane] DatumPlane015  label="VentBasePlane1"
  AttachmentOffset = pos=(-3.5,0,0) rot=(-0.357407,0.862856,0.357407;1.71777rad)
  Length = 116.994
  MapMode = 45
  Placement = pos=(33.5,-88.55,59) rot=(-0.357407,0.862856,0.357407;1.71777rad)
  ResizeMode = 0
  Support = -> [Pocket005]
  Width = 356.981
FEATURE [PartDesign::Plane] DatumPlane016  label="VentBasePlane2"
  AttachmentOffset = pos=(-3.5,7,0) rot=(-0.357407,0.862856,0.357407;1.71777rad)
  Length = 116.994
  MapMode = 45
  Placement = pos=(33.5,-81.55,59) rot=(-0.357407,0.862856,0.357407;1.71777rad)
  ResizeMode = 0
  Support = -> [Pocket005]
  Width = 356.981
FEATURE [PartDesign::ShapeBinder] ShapeBinder001  label="VentBasePlane1Binder"
  Placement = pos=(33.5,-88.55,59) rot=(-0.357407,0.862856,0.357407;1.71777rad)
  Support = -> [DatumPlane015]
  TraceSupport = false
FEATURE [PartDesign::ShapeBinder] ShapeBinder002  label="VentBasePlane2Binder"
  Placement = pos=(33.5,-81.55,59) rot=(-0.357407,0.862856,0.357407;1.71777rad)
  Support = -> [DatumPlane016]
  TraceSupport = false
FEATURE [Sketcher::SketchObject] Sketch020
  FullyConstrained = true
  MapMode = 5
  Placement = pos=(33.5,-88.55,59) rot=(-0.357407,0.862856,0.357407;1.71777rad)
  Support = -> [ShapeBinder001]
  sketch-geometry (6):
    g0: LineSegment StartX=-118.88 StartY=71.68 StartZ=0 EndX=118.88 EndY=71.68 EndZ=0
    g1: LineSegment StartX=118.88 StartY=71.68 StartZ=0 EndX=118.88 EndY=-71.68 EndZ=0
    g2: LineSegment StartX=118.88 StartY=-71.68 StartZ=0 EndX=-118.88 EndY=-71.68 EndZ=0
    g3: LineSegment StartX=-118.88 StartY=-71.68 StartZ=0 EndX=-118.88 EndY=71.68 EndZ=0
    g4: LineSegment StartX=-118.88 StartY=-71.68 StartZ=0 EndX=118.88 EndY=71.68 EndZ=0
    g5: LineSegment StartX=-118.88 StartY=71.68 StartZ=0 EndX=118.88 EndY=-71.68 EndZ=0
  constraints (16):
    c: Coincident(g0,g1)
    c: Coincident(g1,g2)
    c: Coincident(g2,g3)
    c: Coincident(g3,g0)
    c: Horizontal(g0)
    c: Horizontal(g2)
    c: Vertical(g1)
    c: Vertical(g3)
    c: Coincident(g4,g2)
    c: Coincident(g4,g0)
    c: PointOnObject(g-1,g4)
    c: DistanceX(g0,g0) = 237.76
    c: DistanceY(g3,g3) = 143.36
    c: Coincident(g5,g0)
    c: Coincident(g5,g1)
    c: PointOnObject(g-1,g5)
FEATURE [PartDesign::Pad] Pad010  label="IntermediaryProjectionTarget"
  Direction = (0.707107,0.707107,1e-16)
  Length = 4.94975
  Length2 = 10
  Placement = pos=(33.5,-88.55,59) rot=(-0.357407,0.862856,0.357407;1.71777rad)
  Profile = -> Sketch020
  ReferenceAxis = -> Sketch020 [N_Axis]
  Type = 0
  expr: Length = 7 / sqrt(2)
FEATURE [Sketcher::SketchObject] Sketch021  label="VentSketch1"
  FullyConstrained = true
  MapMode = 5
  Placement = pos=(33.5,-88.55,59) rot=(-0.357407,0.862856,0.357407;1.71777rad)
  Support = -> [ShapeBinder001]
  sketch-geometry (7):
    g0: LineSegment StartX=0 StartY=-43.48 StartZ=0 EndX=9e-16 EndY=38.52 EndZ=0
    g1: LineSegment StartX=4.84 StartY=45.59 StartZ=0 EndX=11.84 EndY=45.9042 EndZ=0
    g2: ArcOfEllipse CenterX=4.99846 CenterY=38.52 CenterZ=0 NormalX=0 NormalY=0 NormalZ=1 MajorRadius=7.07356 MinorRadius=4.99846 AngleXU=1.5708 StartAngle=0.031707 EndAngle=1.5708
    g3: LineSegment StartX=4.99846 StartY=45.5936 StartZ=0 EndX=4.99846 EndY=31.4464 EndZ=0
    g4: LineSegment StartX=4e-16 StartY=38.52 StartZ=0 EndX=9.99692 EndY=38.52 EndZ=0
    g5: GeomPoint X=4.99846 Y=43.5251 Z=0
    g6: GeomPoint X=4.99846 Y=33.5149 Z=0
  constraints (12):
    c: PointOnObject(g0,g-2)
    c: PointOnObject(g0,g-2)
    c: InternalAlignment(g3-g6 -> g2) x4
    c: Tangent(g2,g1) = 1.5708
    c: Tangent(g2,g0) = 1.5708
    c: Angle(g0,g1) = 1.61565
    c: Vertical(g3)
    c: DistanceY(g0,g1) = 7.07
    c: DistanceX(g0,g1) = 4.84
    c: DistanceX(g1,g1) = 7
    c: DistanceY(g0,g0) = 82
    c: DistanceY(g-1,g0) = 38.52
FEATURE [Sketcher::SketchObject] Sketch022  label="VentSketch2"
  FullyConstrained = true
  MapMode = 5
  Placement = pos=(33.5,-81.55,59) rot=(-0.357407,0.862856,0.357407;1.71777rad)
  Support = -> [ShapeBinder002]
  sketch-geometry (10):
    g0: LineSegment StartX=0 StartY=-43.48 StartZ=0 EndX=1.2177e-12 EndY=38.52 EndZ=0
    g1: LineSegment StartX=4.84 StartY=45.59 StartZ=0 EndX=11.84 EndY=45.9042 EndZ=0
    g2: ArcOfEllipse CenterX=4.99846 CenterY=38.52 CenterZ=0 NormalX=0 NormalY=0 NormalZ=1 MajorRadius=7.07356 MinorRadius=4.99846 AngleXU=1.5708 StartAngle=0.031707 EndAngle=1.5708
    g3: LineSegment StartX=4.99846 StartY=45.5936 StartZ=0 EndX=4.99846 EndY=31.4464 EndZ=0
    g4: LineSegment StartX=1.2209e-12 StartY=38.52 StartZ=0 EndX=9.99692 EndY=38.52 EndZ=0
    g5: GeomPoint X=4.99846 Y=43.5251 Z=0
    g6: GeomPoint X=4.99846 Y=33.5149 Z=0
    g7: LineSegment StartX=5 StartY=-43.48 StartZ=0 EndX=5 EndY=38.9042 EndZ=0
    g8: ArcOfCircle CenterX=7 CenterY=38.9042 CenterZ=0 NormalX=0 NormalY=0 NormalZ=1 AngleXU=0 Radius=2 StartAngle=1.5708 EndAngle=3.14159
    g9: LineSegment StartX=7 StartY=40.9042 StartZ=0 EndX=11.84 EndY=40.9042 EndZ=0
  constraints (21):
    c: PointOnObject(g0,g-2)
    c: PointOnObject(g0,g-2)
    c: DistanceY(g0,g0) = 82
    c: DistanceX(g1,g1) = 7
    c: Angle(g0,g1) = 1.61565
    c: DistanceY(g0,g1) = 7.07
    c: InternalAlignment(g3-g6 -> g2) x4
    c: Tangent(g2,g1) = 1.5708
    c: Tangent(g2,g0) = 1.5708
    c: DistanceX(g0,g1) = 4.84
    c: Vertical(g7)
    c: Horizontal(g9)
    c: Radius(g8) = 2
    c: Tangent(g9,g8) = 1.5708
    c: Tangent(g8,g7) = 1.5708
    c: DistanceY(g9,g1) = 5
    c: DistanceX(g0,g7) = 5
    c: Horizontal(g0,g7)
    c: Vertical(g9,g1)
    c: DistanceY(g-1,g0) = 38.52
    c: Vertical(g3)
FEATURE [Sketcher::SketchObject] Sketch024
  AttachmentOffset = pos=(0,0,-12) rot=(0,0,1;0rad)
  ExternalGeometry = -> [Pocket005]
  FullyConstrained = true
  MapMode = 3
  Placement = pos=(0,2.7e-15,12) rot=(1,0,0;3.14159rad)
  Support = -> [Pad]
  sketch-geometry (4):
    g0: Circle CenterX=84.5 CenterY=45.5501 CenterZ=0 NormalX=0 NormalY=0 NormalZ=1 AngleXU=0 Radius=4.5
    g1: Circle CenterX=84.5 CenterY=131.55 CenterZ=0 NormalX=0 NormalY=0 NormalZ=1 AngleXU=0 Radius=4.5
    g2: LineSegment StartX=84.5 StartY=131.55 StartZ=0 EndX=80 EndY=171.55 EndZ=0
    g3: LineSegment StartX=84.5 StartY=45.5501 StartZ=0 EndX=80 EndY=5.5501 EndZ=0
  constraints (10):
    c: Vertical(g0,g1)
    c: Diameter(g0) = 9
    c: Diameter(g1) = 9
    c: Coincident(g2,g1)
    c: Coincident(g2,g-3)
    c: Coincident(g3,g0)
    c: Coincident(g3,g-3)
    c: Tangent(g1,g-3)
    c: Equal(g2,g3)
    c: DistanceY(g2,g2) = 40
FEATURE [PartDesign::Line] DatumLine027
  AttacherType = Attacher::AttachEngineLine
  Length = 20
  MapMode = 29
  Placement = pos=(73.5657,-176.745,-32.9193) rot=(0.236749,0.264698,0.934818;1.74884rad)
  ResizeMode = 0
  Support = -> [Pocket005]
FEATURE [Part::Part2DObjectPython] Shape2DView  label="TopProjectionTop"  # Draft 2D object (typed FeaturePython)
  AutoUpdate = true
  Clip = false
  FuseArch = false
  HiddenLines = false
  InPlace = true
  OnlySolids = false
  Projection = (0,0,1)
  ProjectionMode = 0
  SegmentLength = 0.05
  Tessellation = false
  VisibleOnly = false
FEATURE [Part::Part2DObjectPython] Shape2DView001  label="TopProjectionLeft"  # Draft 2D object (typed FeaturePython)
  AutoUpdate = true
  Clip = false
  FuseArch = false
  HiddenLines = false
  InPlace = true
  OnlySolids = false
  Placement = pos=(0,0,0) rot=(0,0,-1;1.5708rad)
  Projection = (0,-1,0)
  ProjectionMode = 0
  SegmentLength = 0.05
  Tessellation = false
  VisibleOnly = false
FEATURE [Part::Part2DObjectPython] Shape2DView002  label="TopProjectionFront"  # Draft 2D object (typed FeaturePython)
  AutoUpdate = true
  Clip = false
  FuseArch = false
  HiddenLines = false
  InPlace = true
  OnlySolids = false
  Placement = pos=(0,0,0) rot=(0,0,1;3.14159rad)
  Projection = (1,-1.19209e-07,1.68587e-07)
  ProjectionMode = 0
  SegmentLength = 0.05
  Tessellation = false
  VisibleOnly = false
FEATURE [Part::Part2DObjectPython] Shape2DView003  label="TopProjectionBottom"  # Draft 2D object (typed FeaturePython)
  AutoUpdate = true
  Clip = false
  FuseArch = false
  HiddenLines = false
  InPlace = true
  OnlySolids = false
  Placement = pos=(-73,0,0) rot=(0,0,-1;1.5708rad)
  Projection = (0,8.74228e-08,-1)
  ProjectionMode = 0
  SegmentLength = 0.05
  Tessellation = false
  VisibleOnly = false
FEATURE [Part::Compound] Compound001  label="CaseTopProjections"
  Links = -> [Shape2DView,Shape2DView001,Shape2DView002,Shape2DView003]
FEATURE [Sketcher::SketchObject] Sketch028  label="BottomSketch1"
  FullyConstrained = true
  MapMode = 5
  Support = -> [XY_Plane020]
  expr: Constraints[11] = <<Params>>.Width - 344 + 318
  expr: Constraints[16] = <<Params>>.Width + 2.7
  sketch-geometry (7):
    g0: LineSegment StartX=0 StartY=-14.35 StartZ=0 EndX=202 EndY=-14.35 EndZ=0
    g1: LineSegment StartX=202 StartY=-14.35 StartZ=0 EndX=202 EndY=-162.75 EndZ=0
    g2: LineSegment StartX=202 StartY=-162.75 StartZ=0 EndX=0 EndY=-162.75 EndZ=0
    g3: LineSegment StartX=0 StartY=-162.75 StartZ=0 EndX=0 EndY=-14.35 EndZ=0
    g4: GeomPoint X=0 Y=-177.1 Z=0
    g5: LineSegment StartX=0 StartY=0 StartZ=0 EndX=0 EndY=-14.35 EndZ=0
    g6: LineSegment StartX=0 StartY=-162.75 StartZ=0 EndX=0 EndY=-177.1 EndZ=0
  constraints (18):
    c: Coincident(g0,g1)
    c: Coincident(g1,g2)
    c: Coincident(g2,g3)
    c: Coincident(g3,g0)
    c: Horizontal(g0)
    c: Horizontal(g2)
    c: Vertical(g1)
    c: Vertical(g3)
    c: PointOnObject(g0,g-2)
    c: PointOnObject(g4,g-2)
    c: DistanceX(g0,g0) = 202
    c: DistanceY(g1,g1) = 148.4
    c: Coincident(g5,g-1)
    c: Coincident(g5,g0)
    c: Coincident(g6,g2)
    c: Coincident(g6,g4)
    c: DistanceY(g4,g5) = 177.1
    c: Equal(g5,g6)
FEATURE [PartDesign::Body] Body017  label="BottomReference"
  Group = -> [Sketch028]
  Origin = -> Origin020
FEATURE [PartDesign::Plane] DatumPlane018  label="4mmAboveBottom"
  AttachmentOffset = pos=(0,0,4) rot=(0,0,1;0rad)
  Length = 722.974
  MapMode = 2
  Placement = pos=(0,0,4) rot=(0,0,1;0rad)
  ResizeMode = 0
  Support = -> [XY_Plane020]
  Width = 722.974
FEATURE [Sketcher::SketchObject] Sketch029  label="BottomSketch2"
  FullyConstrained = true
  MapMode = 5
  Placement = pos=(0,0,4) rot=(0,0,1;0rad)
  Support = -> [DatumPlane018]
  expr: Constraints[17] = <<Params>>.Width + 326 - 344
  expr: Constraints[1] = <<Params>>.Width + 2.7
  sketch-geometry (7):
    g0: GeomPoint X=0 Y=-177.1 Z=0
    g1: LineSegment StartX=0 StartY=-10.35 StartZ=0 EndX=210 EndY=-10.35 EndZ=0
    g2: LineSegment StartX=210 StartY=-10.35 StartZ=0 EndX=210 EndY=-166.75 EndZ=0
    g3: LineSegment StartX=210 StartY=-166.75 StartZ=0 EndX=0 EndY=-166.75 EndZ=0
    g4: LineSegment StartX=0 StartY=-166.75 StartZ=0 EndX=0 EndY=-10.35 EndZ=0
    g5: LineSegment StartX=0 StartY=0 StartZ=0 EndX=0 EndY=-10.35 EndZ=0
    g6: LineSegment StartX=0 StartY=-166.75 StartZ=0 EndX=0 EndY=-177.1 EndZ=0
  constraints (18):
    c: PointOnObject(g0,g-2)
    c: DistanceY(g0,g-1) = 177.1
    c: Coincident(g1,g2)
    c: Coincident(g2,g3)
    c: Coincident(g3,g4)
    c: Coincident(g4,g1)
    c: Horizontal(g1)
    c: Horizontal(g3)
    c: Vertical(g2)
    c: Vertical(g4)
    c: PointOnObject(g1,g-2)
    c: Coincident(g5,g-1)
    c: Coincident(g5,g1)
    c: Coincident(g6,g3)
    c: Coincident(g6,g0)
    c: Equal(g5,g6)
    c: DistanceX(g1,g1) = 210
    c: DistanceY(g2,g2) = 156.4
FEATURE [Sketcher::SketchObject] Sketch030  label="BottomSketch3"
  FullyConstrained = true
  MapMode = 5
  Placement = pos=(0,0,4) rot=(0,0,1;0rad)
  Support = -> [DatumPlane018]
  expr: Constraints[17] = <<Params>>.Width + 335 - 344
  expr: Constraints[1] = <<Params>>.Width + 2.7
  sketch-geometry (7):
    g0: GeomPoint X=0 Y=-177.1 Z=0
    g1: LineSegment StartX=0 StartY=-5.85 StartZ=0 EndX=214 EndY=-5.85 EndZ=0
    g2: LineSegment StartX=214 StartY=-5.85 StartZ=0 EndX=214 EndY=-171.25 EndZ=0
    g3: LineSegment StartX=214 StartY=-171.25 StartZ=0 EndX=0 EndY=-171.25 EndZ=0
    g4: LineSegment StartX=0 StartY=-171.25 StartZ=0 EndX=0 EndY=-5.85 EndZ=0
    g5: LineSegment StartX=0 StartY=0 StartZ=0 EndX=0 EndY=-5.85 EndZ=0
    g6: LineSegment StartX=0 StartY=-171.25 StartZ=0 EndX=0 EndY=-177.1 EndZ=0
  constraints (18):
    c: PointOnObject(g0,g-2)
    c: DistanceY(g0,g-1) = 177.1
    c: Coincident(g1,g2)
    c: Coincident(g2,g3)
    c: Coincident(g3,g4)
    c: Coincident(g4,g1)
    c: Horizontal(g1)
    c: Horizontal(g3)
    c: Vertical(g2)
    c: Vertical(g4)
    c: PointOnObject(g1,g-2)
    c: Coincident(g5,g-1)
    c: Coincident(g5,g1)
    c: Coincident(g6,g3)
    c: Coincident(g6,g0)
    c: Equal(g5,g6)
    c: DistanceX(g1,g1) = 214
    c: DistanceY(g2,g2) = 165.4
FEATURE [PartDesign::Plane] DatumPlane019  label="12mmAboveBottom"
  AttachmentOffset = pos=(0,0,8) rot=(0,0,1;0rad)
  Length = 722.974
  MapMode = 5
  Placement = pos=(0,0,12) rot=(0,0,1;0rad)
  ResizeMode = 0
  Support = -> [DatumPlane018]
  Width = 722.974
FEATURE [Sketcher::SketchObject] Sketch031  label="BottomSketch4"
  FullyConstrained = true
  MapMode = 5
  Placement = pos=(0,0,12) rot=(0,0,1;0rad)
  Support = -> [DatumPlane019]
  expr: Constraints[16] = <<Params>>.Width + 339 - 344
  expr: Constraints[1] = <<Params>>.Width + 2.7
  sketch-geometry (7):
    g0: GeomPoint X=0 Y=-177.1 Z=0
    g1: LineSegment StartX=0 StartY=-3.85 StartZ=0 EndX=226 EndY=-3.85 EndZ=0
    g2: LineSegment StartX=226 StartY=-3.85 StartZ=0 EndX=226 EndY=-173.25 EndZ=0
    g3: LineSegment StartX=226 StartY=-173.25 StartZ=0 EndX=0 EndY=-173.25 EndZ=0
    g4: LineSegment StartX=0 StartY=-173.25 StartZ=0 EndX=0 EndY=-3.85 EndZ=0
    g5: LineSegment StartX=0 StartY=0 StartZ=0 EndX=0 EndY=-3.85 EndZ=0
    g6: LineSegment StartX=0 StartY=-173.25 StartZ=0 EndX=0 EndY=-177.1 EndZ=0
  constraints (18):
    c: PointOnObject(g0,g-2)
    c: DistanceY(g0,g-1) = 177.1
    c: Coincident(g1,g2)
    c: Coincident(g2,g3)
    c: Coincident(g3,g4)
    c: Coincident(g4,g1)
    c: Horizontal(g1)
    c: Horizontal(g3)
    c: Vertical(g2)
    c: Vertical(g4)
    c: PointOnObject(g1,g-2)
    c: Coincident(g5,g-1)
    c: Coincident(g5,g1)
    c: Coincident(g6,g3)
    c: Coincident(g6,g0)
    c: Equal(g5,g6)
    c: DistanceY(g2,g2) = 169.4
    c: DistanceX(g1,g1) = 226
FEATURE [Surface::GeomFillSurface] Surface011
  BoundaryList = -> [Sketch028]
  FillType = 0
FEATURE [Surface::Sections] Surface012
  NSections = -> [Sketch028,Sketch029]
FEATURE [Surface::Sections] Surface013
  NSections = -> [Sketch030,Sketch031]
FEATURE [Part::FeaturePython] Line012  # WARN: FeaturePython — macro-defined, semantics opaque (R4)
  Vertex1 = -> Surface013 [Vertex1]
  Vertex2 = -> Surface012 [Vertex2]
FEATURE [Surface::Sections] Surface014
  NSections = -> [Sketch030,Sketch031]
FEATURE [Surface::Sections] Surface015
  NSections = -> [Sketch028,Sketch029]
FEATURE [Surface::Sections] Surface016
  NSections = -> [Sketch028,Sketch029]
FEATURE [Surface::Sections] Surface017
  NSections = -> [Sketch030,Sketch031]
FEATURE [Surface::Sections] Surface018
  NSections = -> [Sketch030,Sketch031]
FEATURE [Surface::Sections] Surface019
  NSections = -> [Sketch028,Sketch029]
FEATURE [Part::FeaturePython] Line013  # WARN: FeaturePython — macro-defined, semantics opaque (R4)
  Vertex1 = -> Sketch029 [Vertex4]
  Vertex2 = -> Sketch030 [Vertex4]
FEATURE [Surface::Filling] Surface020
  Anisotropy = false
  BoundaryEdges = -> [Surface012,Line012,Surface013,Surface017,Surface014,Line013,Surface015,Surface016]
  BoundaryOrder = [0,0,0,0,0,0,0,0]
  Degree = 3
  Iterations = 2
  MaximumDegree = 8
  MaximumSegments = 9
  PointsOnCurve = 15
  TolAngular = 0.01
  TolCurvature = 0.1
  Tolerance2d = 1e-05
  Tolerance3d = 0.0001
FEATURE [Part::Offset] Offset
  Fill = false
  Intersection = false
  Join = 0
  Mode = 0
  SelfIntersection = false
  Source = -> Surface011
  Value = -3
FEATURE [Part::Offset] Offset001
  Fill = false
  Intersection = false
  Join = 0
  Mode = 0
  SelfIntersection = false
  Source = -> Surface020
  Value = 3
FEATURE [Part::Offset2D] Offset2D
  Fill = false
  Intersection = false
  Join = 0
  Mode = 1
  SelfIntersection = false
  Source = -> Sketch031
  Value = -3
FEATURE [Part::Face] Face
  FaceMakerClass = Part::FaceMakerBullseye
  Sources = -> [Offset2D,Sketch031]
FEATURE [Part::FeaturePython] Line014  # WARN: FeaturePython — macro-defined, semantics opaque (R4)
  Vertex1 = -> Offset001 [Vertex8]
  Vertex2 = -> Offset [Vertex2]
FEATURE [Part::FeaturePython] Line015  # WARN: FeaturePython — macro-defined, semantics opaque (R4)
  Vertex1 = -> Offset [Vertex4]
  Vertex2 = -> Offset001 [Vertex2]
FEATURE [Surface::GeomFillSurface] Surface022
  BoundaryList = -> [Offset001,Line014,Offset,Line015]
  FillType = 0
FEATURE [Part::FeaturePython] Line016  # WARN: FeaturePython — macro-defined, semantics opaque (R4)
FEATURE [Part::FeaturePython] Line017  # WARN: FeaturePython — macro-defined, semantics opaque (R4)
  Placement = pos=(3,0,0) rot=(0,0,1;0rad)
  Vertex1 = -> Offset001 [Vertex6]
  Vertex2 = -> Offset001 [Vertex7]
  expr: .Placement.Base.x = <<Params>>.Walls
FEATURE [Part::FeaturePython] Line018  # WARN: FeaturePython — macro-defined, semantics opaque (R4)
  Placement = pos=(3,0,0) rot=(0,0,1;0rad)
  Vertex1 = -> Offset [Vertex3]
  Vertex2 = -> Offset [Vertex1]
  expr: .Placement.Base.x = <<Params>>.Walls
FEATURE [Part::FeaturePython] Line019  # WARN: FeaturePython — macro-defined, semantics opaque (R4)
  Placement = pos=(3,0,0) rot=(0,0,1;0rad)
  Vertex1 = -> Offset001 [Vertex1]
  Vertex2 = -> Offset001 [Vertex3]
  expr: .Placement.Base.x = <<Params>>.Walls
FEATURE [Part::FeaturePython] Line020  # WARN: FeaturePython — macro-defined, semantics opaque (R4)
  Placement = pos=(0,-2,0) rot=(0,0,1;0rad)
  Vertex1 = -> Line019 [Vertex2]
  Vertex2 = -> Offset001 [Vertex4]
FEATURE [Part::FeaturePython] Line021  # WARN: FeaturePython — macro-defined, semantics opaque (R4)
  Placement = pos=(0,2,0) rot=(0,0,1;0rad)
  Vertex1 = -> Line017 [Vertex1]
  Vertex2 = -> Offset001 [Vertex5]
FEATURE [Part::FeaturePython] Line022  # WARN: FeaturePython — macro-defined, semantics opaque (R4)
  Vertex1 = -> Line021 [Vertex2]
  Vertex2 = -> Offset2D [Vertex3]
FEATURE [Part::FeaturePython] Line023  # WARN: FeaturePython — macro-defined, semantics opaque (R4)
  Vertex1 = -> Line021 [Vertex1]
  Vertex2 = -> Offset2D [Vertex4]
FEATURE [Part::FeaturePython] Line024  # WARN: FeaturePython — macro-defined, semantics opaque (R4)
  Vertex1 = -> Line018 [Vertex2]
  Vertex2 = -> Line017 [Vertex2]
FEATURE [Part::FeaturePython] Line025  # WARN: FeaturePython — macro-defined, semantics opaque (R4)
  Vertex1 = -> Line018 [Vertex1]
  Vertex2 = -> Line019 [Vertex1]
FEATURE [Part::FeaturePython] Line026  # WARN: FeaturePython — macro-defined, semantics opaque (R4)
  Vertex1 = -> Line020 [Vertex1]
  Vertex2 = -> Offset2D [Vertex1]
FEATURE [Part::FeaturePython] Line027  # WARN: FeaturePython — macro-defined, semantics opaque (R4)
  Vertex1 = -> Offset2D [Vertex2]
  Vertex2 = -> Line020 [Vertex2]
FEATURE [Part::FeaturePython] Line028  # WARN: FeaturePython — macro-defined, semantics opaque (R4)
  Vertex1 = -> Line027 [Vertex2]
  Vertex2 = -> Line021 [Vertex2]
FEATURE [Surface::GeomFillSurface] Surface023
  BoundaryList = -> [Line027,Offset2D,Line022]
  FillType = 0
FEATURE [Part::FeaturePython] Line029  # WARN: FeaturePython — macro-defined, semantics opaque (R4)
  Vertex1 = -> Line018 [Vertex2]
  Vertex2 = -> Line014 [Vertex2]
FEATURE [Part::FeaturePython] Line030  # WARN: FeaturePython — macro-defined, semantics opaque (R4)
  Vertex1 = -> Line014 [Vertex1]
  Vertex2 = -> Line017 [Vertex2]
FEATURE [Surface::GeomFillSurface] Surface024
  BoundaryList = -> [Line030,Line024,Line029,Line014]
  FillType = 0
FEATURE [Part::FeaturePython] Line031  # WARN: FeaturePython — macro-defined, semantics opaque (R4)
  Vertex1 = -> Line019 [Vertex1]
  Vertex2 = -> Line024 [Vertex2]
FEATURE [Surface::GeomFillSurface] Surface025
  BoundaryList = -> [Line024,Line031,Line025]
  FillType = 0
FEATURE [Surface::GeomFillSurface] Surface026
  BoundaryList = -> [Line020,Line026,Offset2D]
  FillType = 0
FEATURE [Part::FeaturePython] Line032  # WARN: FeaturePython — macro-defined, semantics opaque (R4)
  Vertex1 = -> Line015 [Vertex2]
  Vertex2 = -> Line019 [Vertex1]
FEATURE [Part::FeaturePython] Line033  # WARN: FeaturePython — macro-defined, semantics opaque (R4)
  Vertex1 = -> Line018 [Vertex1]
  Vertex2 = -> Line015 [Vertex1]
FEATURE [Surface::GeomFillSurface] Surface027
  BoundaryList = -> [Line032,Line015,Line033,Line025]
  FillType = 0
FEATURE [Surface::GeomFillSurface] Surface028
  BoundaryList = -> [Line022,Offset2D,Line023]
  FillType = 0
FEATURE [Surface::GeomFillSurface] Surface029
  BoundaryList = -> [Line026,Offset2D,Line023]
  FillType = 0
FEATURE [Surface::GeomFillSurface] Surface030
  BoundaryList = -> [Surface025,Surface027,Surface022]
  FillType = 0
FEATURE [Part::Compound] Compound002  label="OuterShell"
  Links = -> [Surface011,Surface012,Surface020,Surface013,Surface017,Surface016,Surface015,Surface014,Surface018,Surface019]
FEATURE [Part::FeaturePython] Line034  # WARN: FeaturePython — macro-defined, semantics opaque (R4)
  Vertex1 = -> Surface025 [Vertex4]
  Vertex2 = -> Surface026 [Vertex2]
FEATURE [Part::FeaturePython] Line035  # WARN: FeaturePython — macro-defined, semantics opaque (R4)
  Vertex1 = -> Surface024 [Vertex3]
  Vertex2 = -> Surface028 [Vertex2]
FEATURE [Part::FeaturePython] Line036  # WARN: FeaturePython — macro-defined, semantics opaque (R4)
  Vertex1 = -> Surface023 [Vertex1]
  Vertex2 = -> Line035 [Vertex2]
FEATURE [Part::FeaturePython] Line037  # WARN: FeaturePython — macro-defined, semantics opaque (R4)
  Vertex1 = -> Line036 [Vertex1]
  Vertex2 = -> Surface026 [Vertex4]
FEATURE [Surface::Filling] Surface031
  Anisotropy = false
  BoundaryEdges = -> [Line035,Line036,Line037,Surface026,Line034,Surface027,Surface022,Surface024]
  BoundaryOrder = [0,0,0,0,0,0,0,0]
  Degree = 3
  Iterations = 2
  MaximumDegree = 8
  MaximumSegments = 9
  PointsOnCurve = 15
  TolAngular = 0.01
  TolCurvature = 0.1
  Tolerance2d = 1e-05
  Tolerance3d = 0.0001
FEATURE [Part::Compound] Compound003  label="InnerShell"
  Links = -> [Surface031,Surface022,Surface023,Face,Surface026,Surface027,Surface030,Surface028,Surface024,Surface025,Surface029]
FEATURE [Part::FeaturePython] Solid001  label="BottomPlateSolid"  # WARN: FeaturePython — macro-defined, semantics opaque (R4)
  Faces = -> [Compound003,Compound002]
  Placement = pos=(2.5,0,0) rot=(0,0,1;0rad)
  ShapeStatus = Solid
FEATURE [Part::Compound] Compound004  label="BottomPlateConstruction"
  Links = -> [Line012,Line013,Offset,Offset001,Line014,Line015,Line016,Line017,Line018,Line019,Line020,Line021,Line022,Line023,Line024,Line025,Line026,Line027,Line028,Line029,Line030,Line031,Line032,Line033,Surface011,Surface020,Line034,Line035,Line036,Line037]
FEATURE [PartDesign::Pad] Pad014  label="ScrewColumns"
  BaseFeature = -> Pocket005
  Direction = (0,-2e-16,-1)
  Length = 44
  Length2 = 10
  Profile = -> Sketch024
  ReferenceAxis = -> Sketch024 [N_Axis]
  Reversed = true
  Type = 0
FEATURE [Sketcher::SketchObject] Sketch025
  ExternalGeometry = -> [Pad014]
  FullyConstrained = true
  MapMode = 5
  Placement = pos=(0,2.6e-15,12) rot=(1,0,0;3.14159rad)
  Support = -> [Pad014]
  sketch-geometry (2):
    g0: Circle CenterX=84.5 CenterY=45.5501 CenterZ=0 NormalX=0 NormalY=0 NormalZ=1 AngleXU=0 Radius=1.8
    g1: Circle CenterX=84.5 CenterY=131.55 CenterZ=0 NormalX=0 NormalY=0 NormalZ=1 AngleXU=0 Radius=1.8
  constraints (4):
    c: Diameter(g0) = 3.6
    c: Diameter(g1) = 3.6
    c: Coincident(g-3,g1)
    c: Coincident(g-4,g0)
FEATURE [PartDesign::Pocket] Pocket006  label="ScrewInsertHoles"
  BaseFeature = -> Pad014
  Direction = (0,2e-16,1)
  Length = 4.5
  Length2 = 5
  Profile = -> Sketch025
  ReferenceAxis = -> Sketch025 [N_Axis]
  Type = 0
FEATURE [Sketcher::SketchObject] Sketch026
  ExternalGeometry = -> [Pocket006]
  FullyConstrained = true
  MapMode = 5
  Placement = pos=(12.6406,0,62.1304) rot=(0.994969,0,-0.100188;3.14159rad)
  Support = -> [Pocket006]
  sketch-geometry (6):
    g0: ArcOfCircle CenterX=219.926 CenterY=130.75 CenterZ=0 NormalX=0 NormalY=0 NormalZ=1 AngleXU=0 Radius=3.5 StartAngle=1.5708 EndAngle=4.71239
    g1: ArcOfCircle CenterX=219.926 CenterY=46.35 CenterZ=0 NormalX=0 NormalY=0 NormalZ=1 AngleXU=0 Radius=3.5 StartAngle=1.5708 EndAngle=4.71239
    g2: LineSegment StartX=219.926 StartY=134.25 StartZ=0 EndX=219.926 EndY=127.25 EndZ=0
    g3: LineSegment StartX=219.926 StartY=49.85 StartZ=0 EndX=219.926 EndY=42.85 EndZ=0
    g4: LineSegment StartX=219.926 StartY=46.35 StartZ=0 EndX=219.926 EndY=4.35 EndZ=0
    g5: LineSegment StartX=219.926 StartY=130.75 StartZ=0 EndX=219.926 EndY=172.75 EndZ=0
  constraints (18):
    c: Coincident(g2,g0)
    c: Coincident(g2,g0)
    c: Coincident(g3,g1)
    c: Coincident(g3,g1)
    c: Radius(g1) = 3.5
    c: Radius(g0) = 3.5
    c: PointOnObject(g0,g-3)
    c: PointOnObject(g1,g-3)
    c: PointOnObject(g1,g-3)
    c: PointOnObject(g1,g-3)
    c: PointOnObject(g0,g-3)
    c: PointOnObject(g0,g-3)
    c: Coincident(g4,g1)
    c: Coincident(g4,g-3)
    c: Coincident(g5,g0)
    c: Coincident(g5,g-3)
    c: Equal(g4,g5)
    c: DistanceY(g4,g4) = 42
FEATURE [PartDesign::Pad] Pad013  label="FrontScrewColumns"
  BaseFeature = -> Pocket006
  Direction = (-0.199368,0,-0.979925)
  Length = 5
  Length2 = 10
  Profile = -> Sketch026
  ReferenceAxis = -> Sketch026 [N_Axis]
  Reversed = true
  Type = 0
FEATURE [Sketcher::SketchObject] Sketch027
  ExternalGeometry = -> [Pad013]
  FullyConstrained = true
  MapMode = 5
  Placement = pos=(12.6406,0,62.1304) rot=(0.994969,0,-0.100188;3.14159rad)
  Support = -> [Pad013]
  sketch-geometry (2):
    g0: Circle CenterX=219.926 CenterY=46.35 CenterZ=0 NormalX=0 NormalY=0 NormalZ=1 AngleXU=0 Radius=1.8
    g1: Circle CenterX=219.926 CenterY=130.75 CenterZ=0 NormalX=0 NormalY=0 NormalZ=1 AngleXU=0 Radius=1.8
  constraints (4):
    c: Diameter(g0) = 3.6
    c: Diameter(g1) = 3.6
    c: Coincident(g1,g-3)
    c: Coincident(g0,g-4)
FEATURE [PartDesign::Pocket] Pocket007  label="FrontScrewInsertHoles"
  BaseFeature = -> Pad013
  Direction = (0.199368,0,0.979925)
  Length = 4.5
  Length2 = 5
  Profile = -> Sketch027
  ReferenceAxis = -> Sketch027 [N_Axis]
  Type = 0
  expr: .Direction.y = sin(11.5)
  expr: .Direction.z = cos(11.5)
FEATURE [PartDesign::Fillet] Fillet003
  Base = -> Pocket007 [Face4,Face58,Face56,Face2]
  BaseFeature = -> Pocket007
  Radius = 1
  SupportTransform = false
  UseAllEdges = false
FEATURE [Part::FeaturePython] Line  # WARN: FeaturePython — macro-defined, semantics opaque (R4)
  Vertex1 = -> Sketch022 [Vertex4]
  Vertex2 = -> Sketch022 [Vertex8]
FEATURE [Part::FeaturePython] Line038  # WARN: FeaturePython — macro-defined, semantics opaque (R4)
  Vertex1 = -> Sketch022 [Vertex8]
  Vertex2 = -> Sketch021 [Vertex4]
FEATURE [Part::FeaturePython] Line039  # WARN: FeaturePython — macro-defined, semantics opaque (R4)
  Vertex1 = -> Sketch022 [Vertex4]
  Vertex2 = -> Sketch021 [Vertex4]
FEATURE [Surface::GeomFillSurface] Surface
  BoundaryList = -> [Line039,Line,Line038]
  FillType = 0
FEATURE [Part::FeaturePython] Line040  # WARN: FeaturePython — macro-defined, semantics opaque (R4)
  Vertex1 = -> Sketch022 [Vertex3]
  Vertex2 = -> Sketch022 [Vertex7]
FEATURE [Part::FeaturePython] Line041  # WARN: FeaturePython — macro-defined, semantics opaque (R4)
  Vertex1 = -> Sketch022 [Vertex7]
  Vertex2 = -> Sketch021 [Vertex3]
FEATURE [Part::FeaturePython] Line042  # WARN: FeaturePython — macro-defined, semantics opaque (R4)
  Vertex1 = -> Sketch022 [Vertex3]
  Vertex2 = -> Sketch021 [Vertex3]
FEATURE [Part::FeaturePython] Line043  # WARN: FeaturePython — macro-defined, semantics opaque (R4)
  Vertex1 = -> Sketch022 [Vertex6]
  Vertex2 = -> Sketch022 [Vertex2]
FEATURE [Part::FeaturePython] Line044  # WARN: FeaturePython — macro-defined, semantics opaque (R4)
  Vertex1 = -> Sketch022 [Vertex6]
  Vertex2 = -> Sketch021 [Vertex2]
FEATURE [Part::FeaturePython] Line045  # WARN: FeaturePython — macro-defined, semantics opaque (R4)
  Vertex1 = -> Sketch021 [Vertex2]
  Vertex2 = -> Sketch022 [Vertex2]
FEATURE [Part::FeaturePython] Line046  # WARN: FeaturePython — macro-defined, semantics opaque (R4)
  Vertex1 = -> Sketch022 [Vertex5]
  Vertex2 = -> Sketch022 [Vertex1]
FEATURE [Part::FeaturePython] Line047  # WARN: FeaturePython — macro-defined, semantics opaque (R4)
  Vertex1 = -> Sketch022 [Vertex5]
  Vertex2 = -> Sketch021 [Vertex1]
FEATURE [Part::FeaturePython] Line048  # WARN: FeaturePython — macro-defined, semantics opaque (R4)
  Vertex1 = -> Sketch022 [Vertex1]
  Vertex2 = -> Sketch021 [Vertex1]
FEATURE [Surface::GeomFillSurface] Surface032
  BoundaryList = -> [Line048,Line047,Line046]
  FillType = 0
FEATURE [Surface::GeomFillSurface] Surface033
  BoundaryList = -> [Sketch022,Line043,Line046]
  FillType = 0
FEATURE [Surface::GeomFillSurface] Surface034
  BoundaryList = -> [Line044,Sketch022,Line047,Sketch021]
  FillType = 0
FEATURE [Surface::GeomFillSurface] Surface035
  BoundaryList = -> [Line045,Sketch022,Line048,Sketch021]
  FillType = 0
FEATURE [Surface::GeomFillSurface] Surface036
  BoundaryList = -> [Line041,Sketch022,Line044,Sketch021]
  FillType = 0
FEATURE [Surface::GeomFillSurface] Surface037
  BoundaryList = -> [Line040,Sketch022,Line043]
  FillType = 0
FEATURE [Surface::GeomFillSurface] Surface038
  BoundaryList = -> [Line,Sketch022,Line040]
  FillType = 0
FEATURE [Surface::GeomFillSurface] Surface039
  BoundaryList = -> [Line038,Sketch022,Line041,Sketch021]
  FillType = 0
FEATURE [Surface::GeomFillSurface] Surface040
  BoundaryList = -> [Line039,Sketch022,Line042,Sketch021]
  FillType = 0
FEATURE [Surface::GeomFillSurface] Surface041
  BoundaryList = -> [Line042,Sketch022,Line045,Sketch021]
  FillType = 0
FEATURE [Part::FeaturePython] Solid  label="Vent"  # WARN: FeaturePython — macro-defined, semantics opaque (R4)
  Faces = -> [Surface,Surface032,Surface033,Surface034,Surface035,Surface036,Surface037,Surface038,Surface039,Surface040,Surface041]
  Placement = pos=(-0.1,0,0.1) rot=(0,0,1;0rad)
  ShapeStatus = Solid
FEATURE [PartDesign::Body] Body018
  Origin = -> Origin021
FEATURE [PartDesign::FeatureBase] Clone
  BaseFeature = -> Solid
  Placement = pos=(-0.1,7,0.1) rot=(0,0,1;0rad)
FEATURE [PartDesign::Body] Body019
  Origin = -> Origin022
FEATURE [PartDesign::FeatureBase] Clone001
  BaseFeature = -> Solid
  Placement = pos=(-0.1,14,0.1) rot=(0,0,1;0rad)
FEATURE [PartDesign::Body] Body020
  Origin = -> Origin023
FEATURE [PartDesign::FeatureBase] Clone002
  BaseFeature = -> Solid
  Placement = pos=(-0.1,21,0.1) rot=(0,0,1;0rad)
FEATURE [PartDesign::Body] Body021
  Origin = -> Origin024
FEATURE [PartDesign::FeatureBase] Clone003
  BaseFeature = -> Solid
  Placement = pos=(-0.1,28,0.1) rot=(0,0,1;0rad)
FEATURE [Part::Compound] Compound  label="VentIntermediates"
  Links = -> [Surface041,Line,Line038,Line039,Surface,Line040,Line041,Line042,Line043,Line044,Line045,Line046,Line047,Line048,Surface032,Surface033,Surface034,Surface035,Surface036,Surface037,Surface038,Surface039,Surface040]
FEATURE [PartDesign::Body] Body022
  Origin = -> Origin025
FEATURE [PartDesign::FeatureBase] Clone004
  BaseFeature = -> Solid
  Placement = pos=(-0.1,35,0.1) rot=(0,0,1;0rad)
FEATURE [PartDesign::Body] Body023
  Origin = -> Origin026
FEATURE [PartDesign::FeatureBase] Clone005
  BaseFeature = -> Solid
  Placement = pos=(-0.1,42,0.1) rot=(0,0,1;0rad)
FEATURE [PartDesign::Body] Body024
  Origin = -> Origin027
FEATURE [PartDesign::FeatureBase] Clone006
  BaseFeature = -> Solid
  Placement = pos=(-0.1,-7,0.1) rot=(0,0,1;0rad)
FEATURE [PartDesign::Body] Body025
  Origin = -> Origin028
FEATURE [PartDesign::FeatureBase] Clone007
  BaseFeature = -> Solid
  Placement = pos=(-0.1,-14,0.1) rot=(0,0,1;0rad)
FEATURE [PartDesign::Body] Body026
  Origin = -> Origin029
FEATURE [PartDesign::FeatureBase] Clone008
  BaseFeature = -> Solid
  Placement = pos=(-0.1,-21,0.1) rot=(0,0,1;0rad)
FEATURE [PartDesign::Body] Body027
  Origin = -> Origin030
FEATURE [PartDesign::FeatureBase] Clone009
  BaseFeature = -> Solid
  Placement = pos=(-0.1,-28,0.1) rot=(0,0,1;0rad)
FEATURE [PartDesign::Body] Body028
  Origin = -> Origin031
FEATURE [PartDesign::FeatureBase] Clone010
  BaseFeature = -> Solid
  Placement = pos=(-0.1,-35,0.1) rot=(0,0,1;0rad)
FEATURE [PartDesign::Body] Body029
  Origin = -> Origin032
FEATURE [PartDesign::FeatureBase] Clone011
  BaseFeature = -> Solid
  Placement = pos=(-0.1,-42,0.1) rot=(0,0,1;0rad)
FEATURE [PartDesign::Body] Body030
  Origin = -> Origin033
FEATURE [PartDesign::FeatureBase] Clone012
  BaseFeature = -> Solid
  Placement = pos=(-0.1,-49,0.1) rot=(0,0,1;0rad)
FEATURE [Part::Compound] Compound005  label="VentSet"
  Links = -> [Body030,Solid,Body018,Body019,Body020,Body021,Compound,Body022,Body023,Body024,Body025,Body026,Body027,Body028,Body029]
FEATURE [Part::MultiFuse] Fusion  label="AllVentsInASolid"
  Placement = pos=(3,0,0.5) rot=(0,0,1;0rad)
  Shapes = -> [Clone012,Solid,Clone,Clone001,Clone002,Clone003,Clone004,Clone005,Clone006,Clone007,Clone008,Clone009,Clone010,Clone011]
FEATURE [PartDesign::FeatureBase] BaseFeature  label="BottomPlateIntermediary"
  BaseFeature = -> Solid001
FEATURE [PartDesign::Plane] DatumPlane020  label="FrontDatumPlane"
  AttachmentOffset = pos=(0,0,-231.15) rot=(0,0,1;0rad)
  Length = 88.9342
  MapMode = 3
  Placement = pos=(231.15,-7.7e-14,5.13e-14) rot=(0,-1,0;1.5708rad)
  ResizeMode = 0
  Support = -> [Z_Axis034]
  Width = 223.758
FEATURE [PartDesign::FeatureBase] BaseFeature001
  BaseFeature = -> BaseFeature
FEATURE [PartDesign::ShapeBinder] ShapeBinder004
  Support = -> [BaseFeature001]
  TraceSupport = false
FEATURE [Sketcher::SketchObject] Sketch032  label="FrontSketch"
  ExternalGeometry = -> [ShapeBinder004]
  FullyConstrained = true
  MapMode = 5
  Placement = pos=(231.15,-7.7e-14,5.13e-14) rot=(0,-1,0;1.5708rad)
  Support = -> [DatumPlane020]
  expr: Constraints[12] = <<Params>>.BigFillet
  expr: Constraints[2] = <<Params>>.BigFillet
  expr: Constraints[7] = <<Params>>.Width - 10
  sketch-geometry (8):
    g0: LineSegment StartX=10.6 StartY=-6.35 StartZ=0 EndX=10.6 EndY=-170.75 EndZ=0
    g1: ArcOfCircle CenterX=15.6 CenterY=-6.35 CenterZ=0 NormalX=0 NormalY=0 NormalZ=1 AngleXU=0 Radius=5 StartAngle=1.5708 EndAngle=3.14159
    g2: LineSegment StartX=17.6 StartY=-1.35 StartZ=0 EndX=15.6 EndY=-1.35 EndZ=0
    g3: ArcOfCircle CenterX=15.6 CenterY=-170.75 CenterZ=0 NormalX=0 NormalY=0 NormalZ=1 AngleXU=0 Radius=5 StartAngle=3.14159 EndAngle=4.71239
    g4: LineSegment StartX=15.6 StartY=-175.75 StartZ=0 EndX=17.6 EndY=-175.75 EndZ=0
    g5: LineSegment StartX=17.6 StartY=-1.35 StartZ=0 EndX=17.6 EndY=-175.75 EndZ=0
    g6: LineSegment StartX=12 StartY=-3.85 StartZ=0 EndX=15.6 EndY=-1.35 EndZ=0
    g7: LineSegment StartX=12 StartY=-173.25 StartZ=0 EndX=15.6 EndY=-175.75 EndZ=0
  constraints (24):
    c: Vertical(g0)
    c: Angle(g1) = 1.5708
    c: Radius(g1) = 5
    c: Horizontal(g0,g1)
    c: Coincident(g0,g1)
    c: Horizontal(g2)
    c: DistanceX(g2,g2) = 2
    c: DistanceY(g0,g0) = 164.4
    c: Coincident(g1,g2)
    c: Coincident(g3,g0)
    c: Angle(g3) = 1.5708
    c: Horizontal(g0,g3)
    c: Radius(g3) = 5
    c: Coincident(g4,g3)
    c: Horizontal(g4)
    c: DistanceX(g4,g4) = 2
    c: DistanceX(g-1,g1) = 15.6
    c: Coincident(g5,g2)
    c: Coincident(g5,g4)
    c: Coincident(g6,g-3)
    c: Coincident(g6,g1)
    c: Coincident(g7,g-3)
    c: Coincident(g7,g3)
    c: Equal(g6,g7)
FEATURE [PartDesign::Pad] Pad015  label="KeyboardBottomExtrusion"
  Direction = (-0.979925,0,0.199368)
  Length = 114.65
  Length2 = 10
  Placement = pos=(231.15,-7.7e-14,5.1e-14) rot=(0,-1,0;1.5708rad)
  Profile = -> Sketch032
  ReferenceAxis = -> Sketch032 [N_Axis]
  Type = 0
  UseCustomVector = true
  expr: .Direction.x = -cos(11.5)
  expr: .Direction.z = sin(11.5)
FEATURE [PartDesign::Fillet] Fillet007
  Base = -> Pad015 [Edge9,Edge6,Edge3,Edge17,Edge15,Edge10,Edge7,Edge16,Edge18]
  BaseFeature = -> Pad015
  Placement = pos=(231.15,-7.7e-14,5.1e-14) rot=(0,-1,0;1.5708rad)
  Radius = 1
  SupportTransform = false
  UseAllEdges = false
FEATURE [PartDesign::Fillet] Fillet008
  Base = -> Fillet003 [Edge198,Edge289,Edge293,Edge200]
  BaseFeature = -> Fillet003
  Radius = 1
  SupportTransform = false
  UseAllEdges = false
FEATURE [PartDesign::Fillet] Fillet009
  Base = -> Fillet008 [Edge359,Edge355,Edge345,Edge357,Edge361,Edge330,Edge328,Edge327,Edge329,Edge331]
  BaseFeature = -> Fillet008
  Radius = 1
  SupportTransform = false
  UseAllEdges = false
FEATURE [PartDesign::Body] Body  label="Top"
  Group = -> [Sketch,Pad,DatumPlane008,Fillet,DatumLine,DatumLine001,DatumLine002,DatumLine003,DatumPlane,DatumPlane001,Draft,Sketch003,Pocket,DatumPlane003,DatumPlane004,DatumPlane017,Sketch023,Sketch010,Pad011,Pad007,Boolean,Sketch011,Pocket003,Sketch013,Pad009,DatumPlane010,DatumLine019,DatumLine024,DatumLine025,DatumLine026,DatumPlane011,Sketch018,Pocket004,DatumPlane014,Sketch019,Pocket005,DatumPlane015,+13 more]
  Origin = -> Origin
  Tip = -> Fillet009
FEATURE [Sketcher::SketchObject] Sketch034
  ExternalGeometry = -> [BaseFeature001]
  FullyConstrained = true
  MapMode = 5
  Placement = pos=(2.5,0,12) rot=(0,0,1;0rad)
  Support = -> [Solid001]
  expr: Constraints[7] = <<Params>>.Walls
  sketch-geometry (6):
    g0: LineSegment StartX=0.5 StartY=-4 StartZ=0 EndX=3.5 EndY=-4 EndZ=0
    g1: LineSegment StartX=3.5 StartY=-4 StartZ=0 EndX=3.5 EndY=-173.4 EndZ=0
    g2: LineSegment StartX=3.5 StartY=-173.4 StartZ=0 EndX=0.5 EndY=-173.4 EndZ=0
    g3: LineSegment StartX=0.5 StartY=-173.4 StartZ=0 EndX=0.5 EndY=-4 EndZ=0
    g4: LineSegment StartX=-2.5 StartY=-3.85 StartZ=0 EndX=0.5 EndY=-4 EndZ=0
    g5: LineSegment StartX=0.5 StartY=-173.4 StartZ=0 EndX=-2.5 EndY=-173.25 EndZ=0
  constraints (16):
    c: Coincident(g0,g1)
    c: Coincident(g1,g2)
    c: Coincident(g2,g3)
    c: Coincident(g3,g0)
    c: Horizontal(g0)
    c: Horizontal(g2)
    c: Vertical(g1)
    c: DistanceX(g0,g0) = 3
    c: Vertical(g3)
    c: Coincident(g4,g0)
    c: Coincident(g5,g2)
    c: Equal(g4,g5)
    c: DistanceY(g0,g4) = 0.15
    c: Coincident(g4,g-3)
    c: Coincident(g5,g-3)
    c: DistanceX(g4,g0) = 3
FEATURE [PartDesign::Plane] DatumPlane021
  AttachmentOffset = pos=(0,0,3.5) rot=(1,0,0;0.05236rad)
  Length = 726.007
  MapMode = 5
  Placement = pos=(0,-3.5,-8e-16) rot=(1,0,0;1.62316rad)
  ResizeMode = 0
  Support = -> [XZ_Plane020]
  Width = 756.712
FEATURE [PartDesign::Pad] Pad016  label="BottomPlate"
  Direction = (-0.55,0,1)
  Length = 5.15
  Length2 = 10
  Placement = pos=(2.5,0,0) rot=(0,0,1;0rad)
  Profile = -> Sketch034
  ReferenceAxis = -> Sketch034 [N_Axis]
  TaperAngle = -3
  Type = 0
  UseCustomVector = true
FEATURE [Sketcher::SketchObject] Sketch036
  ExternalGeometry = -> [Pad016]
  FullyConstrained = true
  MapMode = 45
  Placement = pos=(112.527,-4.84091,8.03636) rot=(0.61864,0.619273,0.483514;4.04153rad)
  Support = -> [Pad016]
  sketch-geometry (9):
    g0: LineSegment StartX=3.96711 StartY=115.977 StartZ=0 EndX=3.96711 EndY=-45.44 EndZ=0
    g1: LineSegment StartX=1.96711 StartY=113.06 StartZ=0 EndX=1.96711 EndY=-45.44 EndZ=0
    g2: LineSegment StartX=3.96711 StartY=115.977 StartZ=0 EndX=-4.26684 EndY=103.968 EndZ=0
    g3: GeomPoint X=1.96711 Y=-31.5232 Z=0
    g4: GeomPoint X=3.96711 Y=-31.5232 Z=0
    g5: GeomPoint X=1.96711 Y=-1.52316 Z=0
    g6: GeomPoint X=3.96711 Y=-1.52316 Z=0
    g7: LineSegment StartX=1.96711 StartY=-1.52316 StartZ=0 EndX=3.96711 EndY=-1.52316 EndZ=0
    g8: LineSegment StartX=1.96711 StartY=-31.5232 StartZ=0 EndX=3.96711 EndY=-31.5232 EndZ=0
  constraints (21):
    c: Vertical(g1)
    c: DistanceY(g1,g1) = 158.5
    c: PointOnObject(g3,g1)
    c: PointOnObject(g4,g0)
    c: PointOnObject(g5,g1)
    c: PointOnObject(g6,g0)
    c: Horizontal(g5,g6)
    c: Horizontal(g3,g4)
    c: DistanceY(g6,g0) = 117.5
    c: DistanceY(g4,g0) = 147.5
    c: Coincident(g7,g5)
    c: Coincident(g7,g6)
    c: Coincident(g8,g3)
    c: Coincident(g8,g4)
    c: Coincident(g2,g-3)
    c: Coincident(g0,g2)
    c: Vertical(g0)
    c: Coincident(g0,g-4)
    c: PointOnObject(g1,g2)
    c: Horizontal(g1,g0)
    c: DistanceX(g1,g0) = 2
FEATURE [Sketcher::SketchObject] Sketch035
  ExternalGeometry = -> [Pad016]
  FullyConstrained = true
  MapMode = 5
  Placement = pos=(0,-3.5,-8e-16) rot=(1,0,0;1.62316rad)
  Support = -> [DatumPlane021]
  sketch-geometry (6):
    g0: LineSegment StartX=228.5 StartY=12.0019 StartZ=0 EndX=116.789 EndY=34.7298 EndZ=0
    g1: LineSegment StartX=112.789 StartY=35.5436 StartZ=0 EndX=81.5 EndY=18.5019 EndZ=0
    g2: LineSegment StartX=81.5 StartY=18.5019 StartZ=0 EndX=69.5 EndY=18.5019 EndZ=0
    g3: LineSegment StartX=112.789 StartY=35.5436 StartZ=0 EndX=112.789 EndY=41.7436 EndZ=0
    g4: LineSegment StartX=112.789 StartY=41.7436 StartZ=0 EndX=116.789 EndY=40.9298 EndZ=0
    g5: LineSegment StartX=116.789 StartY=40.9298 StartZ=0 EndX=116.789 EndY=34.7298 EndZ=0
  constraints (18):
    c: Distance(g0) = 114
    c: DistanceX(g1,g0) = 147
    c: Coincident(g2,g1)
    c: Horizontal(g2)
    c: DistanceX(g2,g2) = 12
    c: Angle(g0,g-1) = 0.200713
    c: Coincident(g-3,g0)
    c: DistanceY(g-3,g2) = 6.5
    c: Coincident(g1,g3)
    c: Vertical(g3)
    c: Coincident(g3,g4)
    c: Coincident(g4,g5)
    c: Coincident(g5,g0)
    c: Vertical(g5)
    c: Angle(g4,g-1) = 0.200713
    c: DistanceY(g3,g3) = 6.2
    c: Equal(g3,g5)
    c: DistanceX(g4,g4) = 4
FEATURE [Part::FeaturePython] Line049  # WARN: FeaturePython — macro-defined, semantics opaque (R4)
  Vertex1 = -> Sketch036 [Vertex1]
  Vertex2 = -> Sketch036 [Vertex3]
FEATURE [Part::FeaturePython] Line050  # WARN: FeaturePython — macro-defined, semantics opaque (R4)
  Vertex1 = -> Sketch036 [Vertex1]
  Vertex2 = -> Sketch035 [Vertex2]
FEATURE [Part::FeaturePython] Line051  # WARN: FeaturePython — macro-defined, semantics opaque (R4)
  Vertex1 = -> Sketch035 [Vertex2]
  Vertex2 = -> Sketch035 [Vertex3]
FEATURE [Part::FeaturePython] Line052  # WARN: FeaturePython — macro-defined, semantics opaque (R4)
  Vertex1 = -> Sketch035 [Vertex3]
  Vertex2 = -> Sketch035 [Vertex4]
FEATURE [Part::FeaturePython] Line053  # WARN: FeaturePython — macro-defined, semantics opaque (R4)
  Vertex1 = -> Sketch036 [Vertex3]
  Vertex2 = -> Sketch036 [Vertex5]
FEATURE [Part::FeaturePython] Line054  # WARN: FeaturePython — macro-defined, semantics opaque (R4)
  Vertex1 = -> Sketch036 [Vertex5]
  Vertex2 = -> Sketch036 [Vertex7]
FEATURE [Part::FeaturePython] Line055  # WARN: FeaturePython — macro-defined, semantics opaque (R4)
  Vertex1 = -> Sketch036 [Vertex7]
  Vertex2 = -> Sketch036 [Vertex4]
FEATURE [Part::FeaturePython] Line056  # WARN: FeaturePython — macro-defined, semantics opaque (R4)
  Vertex1 = -> Sketch036 [Vertex1]
  Vertex2 = -> Sketch036 [Vertex2]
FEATURE [Part::FeaturePython] Line057  # WARN: FeaturePython — macro-defined, semantics opaque (R4)
  Vertex1 = -> Sketch036 [Vertex6]
  Vertex2 = -> Sketch036 [Vertex8]
FEATURE [Part::FeaturePython] Interpolation_Curve001  # WARN: FeaturePython — macro-defined, semantics opaque (R4)
  CustomTangents = true
  DetectAligned = false
  Parameters = [0,0.23076,1]
  Parametrization = 0
  Periodic = false
  PointList = -> [Line055,Line057,Sketch035]
  Polygonal = false
  Tangents = (3) [(-0.02,0.31,0.95),(-0.02,0.31,0.95),(0.12,-0.32,0.94)]
  Tolerance = 1e-07
  UTurns = 0
  VTurns = 0
  WireOutput = false
FEATURE [Part::FeaturePython] Interpolation_Curve002  # WARN: FeaturePython — macro-defined, semantics opaque (R4)
  CustomTangents = true
  DetectAligned = false
  Parameters = [0,0.1,1]
  Parametrization = 3
  Periodic = false
  PointList = -> [Line053,Line057,Line050]
  Polygonal = false
  Tangents = (3) [(0,0.26,0.96),(0,0.13,0.48),(0,0,1)]
  Tolerance = 1e-07
  UTurns = 0
  VTurns = 0
  WireOutput = false
FEATURE [Part::FeaturePython] Line058  # WARN: FeaturePython — macro-defined, semantics opaque (R4)
  Vertex1 = -> Line055 [Vertex2]
  Vertex2 = -> Sketch035 [Vertex7]
FEATURE [Part::FeaturePython] Line059  # WARN: FeaturePython — macro-defined, semantics opaque (R4)
  Vertex1 = -> Line057 [Vertex1]
  Vertex2 = -> Line056 [Vertex1]
FEATURE [Part::FeaturePython] SplitCurve  # WARN: FeaturePython — macro-defined, semantics opaque (R4)
  Distance = 0
  NormalizedParameters = [0,0.884765,1]
  Source = -> Interpolation_Curve002 [Edge1]
  Values = 80%
FEATURE [Part::FeaturePython] Line060  # WARN: FeaturePython — macro-defined, semantics opaque (R4)
  Vertex1 = -> SplitCurve [Vertex2]
  Vertex2 = -> Line056 [Vertex1]
FEATURE [Part::FeaturePython] Line062  # WARN: FeaturePython — macro-defined, semantics opaque (R4)
  Vertex1 = -> Line058 [Vertex2]
  Vertex2 = -> Interpolation_Curve001 [Vertex2]
FEATURE [Part::FeaturePython] Line064  # WARN: FeaturePython — macro-defined, semantics opaque (R4)
  Vertex1 = -> Sketch035 [Vertex5]
  Vertex2 = -> Sketch035 [Vertex4]
FEATURE [Part::FeaturePython] Line063  # WARN: FeaturePython — macro-defined, semantics opaque (R4)
  Vertex1 = -> Line064 [Vertex1]
  Vertex2 = -> Line062 [Vertex2]
FEATURE [PartDesign::Body] Body032  label="BottomPlateBody"
  Origin = -> Origin035
  Placement = pos=(3,0,0) rot=(0,0,1;0rad)
FEATURE [PartDesign::FeatureBase] BaseFeature002
  BaseFeature = -> Pad016
FEATURE [PartDesign::Plane] DatumPlane022
  AttachmentOffset = pos=(0,0,173.1) rot=(0,0,1;0rad)
  Length = 722.974
  MapMode = 5
  Placement = pos=(0,-173.1,-3.84e-14) rot=(1,0,0;1.5708rad)
  ResizeMode = 0
  Support = -> [XZ_Plane035]
  Width = 722.974
  expr: .AttachmentOffset.Base.z = <<Params>>.Width - 1.3
FEATURE [Sketcher::SketchObject] Sketch037
  FullyConstrained = true
  MapMode = 5
  Placement = pos=(0,-173.1,-3.84e-14) rot=(1,0,0;1.5708rad)
  Support = -> [DatumPlane022]
  sketch-geometry (12):
    g0: LineSegment StartX=80 StartY=9.2 StartZ=0 EndX=93.5 EndY=9.2 EndZ=0
    g1: LineSegment StartX=93.5 StartY=9.2 StartZ=0 EndX=93.5 EndY=5 EndZ=0
    g2: LineSegment StartX=93.5 StartY=5 StartZ=0 EndX=80 EndY=5 EndZ=0
    g3: LineSegment StartX=80 StartY=5 StartZ=0 EndX=80 EndY=9.2 EndZ=0
    g4: LineSegment StartX=30.75 StartY=9.5 StartZ=0 EndX=8.75 EndY=9.5 EndZ=0
    g5: LineSegment StartX=8.75 StartY=9.5 StartZ=0 EndX=8.75 EndY=21.5 EndZ=0
    g6: LineSegment StartX=8.75 StartY=21.5 StartZ=0 EndX=30.75 EndY=21.5 EndZ=0
    g7: LineSegment StartX=30.75 StartY=21.5 StartZ=0 EndX=30.75 EndY=9.5 EndZ=0
    g8: LineSegment StartX=59.15 StartY=9.5 StartZ=0 EndX=37.15 EndY=9.5 EndZ=0
    g9: LineSegment StartX=37.15 StartY=9.5 StartZ=0 EndX=37.15 EndY=21.5 EndZ=0
    g10: LineSegment StartX=37.15 StartY=21.5 StartZ=0 EndX=59.15 EndY=21.5 EndZ=0
    g11: LineSegment StartX=59.15 StartY=21.5 StartZ=0 EndX=59.15 EndY=9.5 EndZ=0
  constraints (36):
    c: Coincident(g0,g1)
    c: Coincident(g1,g2)
    c: Coincident(g2,g3)
    c: Coincident(g3,g0)
    c: Horizontal(g0)
    c: Horizontal(g2)
    c: Vertical(g1)
    c: Vertical(g3)
    c: DistanceX(g0,g0) = 13.5
    c: DistanceY(g1,g1) = 4.2
    c: DistanceX(g-1,g2) = 80
    c: DistanceY(g-1,g2) = 5
    c: Horizontal(g4)
    c: Coincident(g4,g5)
    c: Vertical(g5)
    c: Coincident(g5,g6)
    c: Horizontal(g6)
    c: Coincident(g6,g7)
    c: Vertical(g7)
    c: Horizontal(g8)
    c: Coincident(g8,g9)
    c: Vertical(g9)
    c: Coincident(g9,g10)
    c: Horizontal(g10)
    c: Coincident(g10,g11)
    c: Vertical(g11)
    c: Equal(g5,g9)
    c: DistanceX(g6,g6) = 22
    c: DistanceX(g-1,g4) = 8.75
    c: DistanceX(g6,g9) = 6.4
    c: DistanceY(g5,g5) = 12
    c: DistanceY(g-1,g4) = 9.5
    c: Coincident(g4,g7)
    c: Coincident(g8,g11)
    c: Equal(g6,g10)
    c: Horizontal(g4,g8)
FEATURE [Sketcher::SketchObject] Sketch038
  FullyConstrained = true
  MapMode = 5
  Placement = pos=(0,-173.1,-3.84e-14) rot=(1,0,0;1.5708rad)
  Support = -> [DatumPlane022]
  sketch-geometry (11):
    g0: LineSegment StartX=5.5 StartY=11.95 StartZ=0 EndX=62.5 EndY=11.95 EndZ=0
    g1: LineSegment StartX=62.5 StartY=11.95 StartZ=0 EndX=62.5 EndY=23.45 EndZ=0
    g2: LineSegment StartX=62.5 StartY=23.45 StartZ=0 EndX=5.5 EndY=23.45 EndZ=0
    g3: LineSegment StartX=5.5 StartY=23.45 StartZ=0 EndX=5.5 EndY=11.95 EndZ=0
    g4: LineSegment StartX=5.5 StartY=11.95 StartZ=0 EndX=5.75 EndY=21.5023 EndZ=0
    g5: LineSegment StartX=62.5 StartY=11.95 StartZ=0 EndX=62.25 EndY=21.5023 EndZ=0
    g6: LineSegment StartX=7.74932 StartY=23.45 StartZ=0 EndX=60.2507 EndY=23.45 EndZ=0
    g7: ArcOfCircle CenterX=7.74932 CenterY=21.45 CenterZ=0 NormalX=0 NormalY=0 NormalZ=1 AngleXU=0 Radius=2 StartAngle=1.5708 EndAngle=3.11543
    g8: GeomPoint X=5.80097 Y=23.45 Z=0
    g9: ArcOfCircle CenterX=60.2507 CenterY=21.45 CenterZ=0 NormalX=0 NormalY=0 NormalZ=1 AngleXU=0 Radius=2 StartAngle=0.0261657 EndAngle=1.5708
    g10: GeomPoint X=62.199 Y=23.45 Z=0
  constraints (28):
    c: Coincident(g0,g1)
    c: Coincident(g1,g2)
    c: Coincident(g2,g3)
    c: Coincident(g3,g0)
    c: Horizontal(g0)
    c: Horizontal(g2)
    c: DistanceX(g2,g2) = 57
    c: DistanceY(g1,g1) = 11.5
    c: DistanceX(g-1,g0) = 5.5
    c: DistanceY(g-1,g0) = 11.95
    c: Coincident(g4,g0)
    c: PointOnObject(g8,g2)
    c: Coincident(g5,g0)
    c: PointOnObject(g10,g2)
    c: PointOnObject(g8,g4)
    c: PointOnObject(g8,g6)
    c: Tangent(g4,g7) = 1.5708
    c: Tangent(g6,g7) = 1.5708
    c: PointOnObject(g10,g6)
    c: PointOnObject(g10,g5)
    c: Tangent(g6,g9) = 1.5708
    c: Tangent(g5,g9) = -1.5708
    c: Equal(g4,g5)
    c: Vertical(g1)
    c: Vertical(g3)
    c: Horizontal(g4,g5)
    c: DistanceX(g4,g5) = 56.5
    c: Radius(g7) = 2
FEATURE [PartDesign::Pad] Pad017  label="LeftJoystickPane"
  Direction = (0,-1,-2e-16)
  Length = 3
  Length2 = 10
  Placement = pos=(0,-173.1,-3.8e-14) rot=(1,0,0;1.5708rad)
  Profile = -> Sketch038
  ReferenceAxis = -> Sketch038 [N_Axis]
  Reversed = true
  Type = 0
  expr: Length = <<Params>>.Walls
FEATURE [PartDesign::Pocket] Pocket009  label="BottomLeftJoystickPorts"
  Direction = (0,1,2e-16)
  Length = 21
  Length2 = 5
  Midplane = true
  Profile = -> Sketch037
  ReferenceAxis = -> Sketch037 [N_Axis]
  Type = 0
FEATURE [PartDesign::Plane] DatumPlane023
  AttachmentOffset = pos=(0,0,4.02) rot=(0,0,1;0rad)
  Length = 722.974
  MapMode = 5
  Placement = pos=(0,-4.02,-9e-16) rot=(1,0,0;1.5708rad)
  ResizeMode = 0
  Support = -> [XZ_Plane035]
  Width = 722.974
FEATURE [Sketcher::SketchObject] Sketch039
  FullyConstrained = true
  MapMode = 5
  Placement = pos=(0,-4.02,-9e-16) rot=(1,0,0;1.5708rad)
  Support = -> [DatumPlane023]
  sketch-geometry (8):
    g0: LineSegment StartX=5.75 StartY=21.5023 StartZ=0 EndX=5.5 EndY=11.95 EndZ=0
    g1: LineSegment StartX=5.5 StartY=11.95 StartZ=0 EndX=62.5 EndY=11.95 EndZ=0
    g2: LineSegment StartX=62.5 StartY=11.95 StartZ=0 EndX=62.25 EndY=21.5023 EndZ=0
    g3: LineSegment StartX=60.2507 StartY=23.45 StartZ=0 EndX=7.74932 EndY=23.45 EndZ=0
    g4: ArcOfCircle CenterX=7.74932 CenterY=21.45 CenterZ=0 NormalX=0 NormalY=0 NormalZ=1 AngleXU=0 Radius=2 StartAngle=1.5708 EndAngle=3.11543
    g5: GeomPoint X=5.80097 Y=23.45 Z=0
    g6: ArcOfCircle CenterX=60.2507 CenterY=21.45 CenterZ=0 NormalX=0 NormalY=0 NormalZ=1 AngleXU=0 Radius=2 StartAngle=0.0261657 EndAngle=1.5708
    g7: GeomPoint X=62.199 Y=23.45 Z=0
  constraints (20):
    c: Coincident(g0,g1)
    c: Horizontal(g1)
    c: Coincident(g1,g2)
    c: Horizontal(g3)
    c: PointOnObject(g5,g0)
    c: PointOnObject(g5,g3)
    c: Tangent(g0,g4) = -1.5708
    c: Tangent(g3,g4) = -1.5708
    c: PointOnObject(g7,g3)
    c: PointOnObject(g7,g2)
    c: Tangent(g3,g6) = -1.5708
    c: Tangent(g2,g6) = -1.5708
    c: Equal(g4,g6)
    c: Radius(g4) = 2
    c: Equal(g0,g2)
    c: DistanceX(g1,g1) = 57
    c: DistanceX(g0,g2) = 56.5
    c: DistanceY(g1,g3) = 11.5
    c: DistanceY(g-1,g0) = 11.95
    c: DistanceX(g-1,g0) = 5.5
FEATURE [PartDesign::Pad] Pad018  label="RightJoystickPane"
  BaseFeature = -> Pocket009
  Direction = (0,-1,-2e-16)
  Length = 3
  Length2 = 10
  Profile = -> Sketch039
  ReferenceAxis = -> Sketch039 [N_Axis]
  Type = 0
  expr: Length = <<Params>>.Walls
FEATURE [Sketcher::SketchObject] Sketch040
  FullyConstrained = true
  MapMode = 5
  Placement = pos=(0,-4.02,-9e-16) rot=(1,0,0;1.5708rad)
  Support = -> [DatumPlane023]
  sketch-geometry (8):
    g0: LineSegment StartX=8.75 StartY=21.5 StartZ=0 EndX=27.95 EndY=21.5 EndZ=0
    g1: LineSegment StartX=27.95 StartY=21.5 StartZ=0 EndX=27.95 EndY=9.5 EndZ=0
    g2: LineSegment StartX=27.95 StartY=9.5 StartZ=0 EndX=8.75 EndY=9.5 EndZ=0
    g3: LineSegment StartX=8.75 StartY=9.5 StartZ=0 EndX=8.75 EndY=21.5 EndZ=0
    g4: LineSegment StartX=39.95 StartY=21.5 StartZ=0 EndX=59.15 EndY=21.5 EndZ=0
    g5: LineSegment StartX=59.15 StartY=21.5 StartZ=0 EndX=59.15 EndY=9.5 EndZ=0
    g6: LineSegment StartX=59.15 StartY=9.5 StartZ=0 EndX=39.95 EndY=9.5 EndZ=0
    g7: LineSegment StartX=39.95 StartY=9.5 StartZ=0 EndX=39.95 EndY=21.5 EndZ=0
  constraints (24):
    c: Coincident(g0,g1)
    c: Coincident(g1,g2)
    c: Coincident(g2,g3)
    c: Coincident(g3,g0)
    c: Horizontal(g0)
    c: Horizontal(g2)
    c: Vertical(g1)
    c: Vertical(g3)
    c: Coincident(g4,g5)
    c: Coincident(g5,g6)
    c: Coincident(g6,g7)
    c: Coincident(g7,g4)
    c: Horizontal(g4)
    c: Horizontal(g6)
    c: Vertical(g5)
    c: Vertical(g7)
    c: Equal(g0,g4)
    c: Equal(g3,g7)
    c: Horizontal(g0,g4)
    c: DistanceX(g0,g4) = 12
    c: DistanceX(g0,g0) = 19.2
    c: DistanceX(g-1,g2) = 8.75
    c: DistanceY(g-1,g2) = 9.5
    c: DistanceY(g3,g3) = 12
FEATURE [PartDesign::Pocket] Pocket010  label="BottomRightJoystickPorts"
  BaseFeature = -> Pocket009
  Direction = (0,1,2e-16)
  Length = 10
  Length2 = 5
  Midplane = true
  Profile = -> Sketch040
  ReferenceAxis = -> Sketch040 [N_Axis]
  Type = 0
FEATURE [Sketcher::SketchObject] Sketch041  label="JoystickGlyphSketch"
  FullyConstrained = true
  MapMode = 5
  Placement = pos=(0,-4.02,-9e-16) rot=(1,0,0;1.5708rad)
  Support = -> [DatumPlane023]
  sketch-geometry (20):
    g0: LineSegment StartX=33.05 StartY=18.4033 StartZ=0 EndX=31.2983 EndY=16.6517 EndZ=0
    g1: LineSegment StartX=31.2983 StartY=16.6517 StartZ=0 EndX=33.95 EndY=14 EndZ=0
    g2: LineSegment StartX=33.95 StartY=14 StartZ=0 EndX=36.6017 EndY=16.6517 EndZ=0
    g3: LineSegment StartX=36.6017 StartY=16.6517 StartZ=0 EndX=34.85 EndY=18.4033 EndZ=0
    g4: LineSegment StartX=34.85 StartY=18.4033 StartZ=0 EndX=34.85 EndY=16.6517 EndZ=0
    g5: LineSegment StartX=33.05 StartY=18.4033 StartZ=0 EndX=33.05 EndY=16.6517 EndZ=0
    g6: ArcOfCircle CenterX=33.95 CenterY=16.6517 CenterZ=0 NormalX=0 NormalY=0 NormalZ=1 AngleXU=0 Radius=0.9 StartAngle=3.14159 EndAngle=6.28319
    g7: LineSegment StartX=31.2983 StartY=16.2325 StartZ=0 EndX=33.7732 EndY=13.7576 EndZ=0
    g8: LineSegment StartX=33.7732 StartY=13.7576 StartZ=0 EndX=33.7732 EndY=12.6576 EndZ=0
    g9: LineSegment StartX=33.7732 StartY=12.6576 StartZ=0 EndX=31.2983 EndY=15.1325 EndZ=0
    g10: LineSegment StartX=31.2983 StartY=15.1325 StartZ=0 EndX=31.2983 EndY=16.2325 EndZ=0
    g11: LineSegment StartX=36.6017 StartY=16.2325 StartZ=0 EndX=34.1268 EndY=13.7576 EndZ=0
    g12: LineSegment StartX=34.1268 StartY=13.7576 StartZ=0 EndX=34.1268 EndY=12.6576 EndZ=0
    g13: LineSegment StartX=34.1268 StartY=12.6576 StartZ=0 EndX=36.6017 EndY=15.1325 EndZ=0
    g14: LineSegment StartX=36.6017 StartY=15.1325 StartZ=0 EndX=36.6017 EndY=16.2325 EndZ=0
    g15: ArcOfCircle CenterX=33.95 CenterY=16.6517 CenterZ=0 NormalX=0 NormalY=0 NormalZ=1 AngleXU=0 Radius=0.7 StartAngle=3.14159 EndAngle=6.28319
    g16: Circle CenterX=33.95 CenterY=20.2933 CenterZ=0 NormalX=0 NormalY=0 NormalZ=1 AngleXU=0 Radius=0.7
    g17: ArcOfCircle CenterX=33.95 CenterY=20.2933 CenterZ=0 NormalX=0 NormalY=0 NormalZ=1 AngleXU=0 Radius=0.9 StartAngle=3.82127 EndAngle=5.60351
    g18: LineSegment StartX=33.25 StartY=16.6517 StartZ=0 EndX=33.25 EndY=19.7276 EndZ=0
    g19: LineSegment StartX=34.65 StartY=19.7276 StartZ=0 EndX=34.65 EndY=16.6517 EndZ=0
  constraints (61):
    c: Coincident(g0,g1)
    c: Coincident(g1,g2)
    c: Coincident(g2,g3)
    c: Coincident(g3,g4)
    c: Vertical(g4)
    c: Coincident(g5,g0)
    c: Vertical(g5)
    c: Coincident(g6,g5)
    c: Coincident(g6,g4)
    c: Angle(g4,g3) = 0.785398
    c: Equal(g3,g0)
    c: Horizontal(g0,g2)
    c: Vertical(g6,g1)
    c: Equal(g1,g2)
    c: Angle(g1,g0) = 1.5708
    c: DistanceX(g0,g3) = 1.8
    c: Distance(g2) = 3.75
    c: Coincident(g7,g8)
    c: Vertical(g8)
    c: Coincident(g8,g9)
    c: Coincident(g9,g10)
    c: Coincident(g10,g7)
    c: Vertical(g10)
    c: Angle(g8,g9) = 0.785398
    c: Equal(g8,g10)
    c: Vertical(g7,g0)
    c: DistanceY(g8,g8) = 1.1
    c: Distance(g7) = 3.5
    c: Coincident(g11,g12)
    c: Vertical(g12)
    c: Coincident(g12,g13)
    c: Coincident(g13,g14)
    c: Coincident(g14,g11)
    c: Vertical(g14)
    c: Equal(g8,g12)
    c: Equal(g7,g11)
    c: Vertical(g2,g11)
    c: Angle(g13,g12) = 0.785398
    c: Coincident(g15,g6)
    c: Horizontal(g5,g15)
    c: Horizontal(g6,g15)
    c: Diameter(g16) = 1.4
    c: Vertical(g6,g16)
    c: Equal(g17,g6)
    c: Horizontal(g7,g11)
    c: Coincident(g18,g15)
    c: Coincident(g18,g17)
    c: Vertical(g18)
    c: Coincident(g19,g17)
    c: Coincident(g19,g15)
    c: Vertical(g19)
    c: Tangent(g18,g16)
    c: Parallel(g2,g11)
    c: Distance(g1,g11) = 0.3
    c: Tangent(g0,g16)
    c: Coincident(g17,g16)
    c: Horizontal(g0,g6)
    c: Horizontal(g15,g15)
    c: Horizontal(g15,g4)
    c: DistanceX(g-1,g6) = 33.95
    c: DistanceY(g-1,g1) = 14
FEATURE [PartDesign::Pad] Pad019  label="JoystickGlyph"
  BaseFeature = -> Pocket010
  Direction = (0,-1,-2e-16)
  Length = 0.5
  Length2 = 10
  Midplane = true
  Profile = -> Sketch041
  ReferenceAxis = -> Sketch041 [N_Axis]
  Type = 0
FEATURE [PartDesign::Plane] DatumPlane024
  AttachmentOffset = pos=(0,0,2.9) rot=(0,0,1;0rad)
  Length = 722.974
  MapMode = 5
  Placement = pos=(0,0,2.9) rot=(0,0,1;0rad)
  ResizeMode = 0
  Support = -> [XY_Plane035]
  Width = 722.974
FEATURE [Sketcher::SketchObject] Sketch042
  FullyConstrained = true
  MapMode = 5
  Placement = pos=(0,0,2.9) rot=(0,0,1;0rad)
  Support = -> [DatumPlane024]
  expr: Constraints[4] = <<Params>>.Width - 88.40000000000001
  sketch-geometry (2):
    g0: Circle CenterX=81.5 CenterY=-131.5 CenterZ=0 NormalX=0 NormalY=0 NormalZ=1 AngleXU=0 Radius=6
    g1: Circle CenterX=81.5 CenterY=-45.5 CenterZ=0 NormalX=0 NormalY=0 NormalZ=1 AngleXU=0 Radius=6
  constraints (6):
    c: Vertical(g1,g0)
    c: Equal(g1,g0)
    c: Diameter(g1) = 12
    c: DistanceY(g1,g-1) = 45.5  'd1'
    c: DistanceY(g0,g1) = 86
    c: DistanceX(g-1,g1) = 81.5
FEATURE [PartDesign::Pad] Pad020  label="BottomScrewColumns"
  Direction = (0,0,1)
  Length = 9
  Length2 = 10
  Placement = pos=(0,0,2.9) rot=(0,0,1;0rad)
  Profile = -> Sketch042
  ReferenceAxis = -> Sketch042 [N_Axis]
  Type = 0
FEATURE [Sketcher::SketchObject] Sketch043
  ExternalGeometry = -> [Pad020]
  FullyConstrained = true
  MapMode = 5
  Placement = pos=(0,0,14.8) rot=(0,0,1;0rad)
  Support = -> [Pad020]
  sketch-geometry (2):
    g0: Circle CenterX=81.5 CenterY=-131.5 CenterZ=0 NormalX=0 NormalY=0 NormalZ=1 AngleXU=0 Radius=1.5
    g1: Circle CenterX=81.5 CenterY=-45.5 CenterZ=0 NormalX=0 NormalY=0 NormalZ=1 AngleXU=0 Radius=1.5
  constraints (4):
    c: Equal(g0,g1)
    c: Diameter(g0) = 3
    c: Coincident(g0,g-4)
    c: Coincident(g1,g-3)
FEATURE [PartDesign::Pocket] Pocket011  label="BottomScrewHoles"
  BaseFeature = -> Pad020
  Direction = (0,0,-1)
  Length = 15
  Length2 = 5
  Profile = -> Sketch043
  ReferenceAxis = -> Sketch043 [N_Axis]
  Type = 0
FEATURE [PartDesign::Plane] DatumPlane025  label="BottomPlane"
  Length = 722.974
  MapMode = 5
  ResizeMode = 0
  Support = -> [XY_Plane035]
  Width = 722.974
FEATURE [Sketcher::SketchObject] Sketch044
  ExternalGeometry = -> [Pocket011]
  FullyConstrained = true
  MapMode = 5
  Support = -> [DatumPlane025]
  sketch-geometry (24):
    g0: ArcOfCircle CenterX=79.75 CenterY=-129.75 CenterZ=0 NormalX=0 NormalY=0 NormalZ=1 AngleXU=0 Radius=2 StartAngle=1.5708 EndAngle=3.14159
    g1: LineSegment StartX=79.75 StartY=-127.75 StartZ=0 EndX=83.25 EndY=-127.75 EndZ=0
    g2: ArcOfCircle CenterX=83.25 CenterY=-129.75 CenterZ=0 NormalX=0 NormalY=0 NormalZ=1 AngleXU=0 Radius=2 StartAngle=-9e-16 EndAngle=1.5708
    g3: LineSegment StartX=85.25 StartY=-129.75 StartZ=0 EndX=85.25 EndY=-133.25 EndZ=0
    g4: ArcOfCircle CenterX=83.25 CenterY=-133.25 CenterZ=0 NormalX=0 NormalY=0 NormalZ=1 AngleXU=0 Radius=2 StartAngle=4.71239 EndAngle=6.28319
    g5: LineSegment StartX=83.25 StartY=-135.25 StartZ=0 EndX=79.75 EndY=-135.25 EndZ=0
    g6: ArcOfCircle CenterX=79.75 CenterY=-133.25 CenterZ=0 NormalX=0 NormalY=0 NormalZ=1 AngleXU=0 Radius=2 StartAngle=3.14159 EndAngle=4.71239
    g7: LineSegment StartX=77.75 StartY=-133.25 StartZ=0 EndX=77.75 EndY=-129.75 EndZ=0
    g8: GeomPoint X=77.75 Y=-127.75 Z=0
    g9: GeomPoint X=85.25 Y=-135.25 Z=0
    g10: ArcOfCircle CenterX=79.75 CenterY=-43.75 CenterZ=0 NormalX=0 NormalY=0 NormalZ=1 AngleXU=0 Radius=2 StartAngle=1.5708 EndAngle=3.14159
    g11: LineSegment StartX=79.75 StartY=-41.75 StartZ=0 EndX=83.25 EndY=-41.75 EndZ=0
    g12: ArcOfCircle CenterX=83.25 CenterY=-43.75 CenterZ=0 NormalX=0 NormalY=0 NormalZ=1 AngleXU=0 Radius=2 StartAngle=2e-16 EndAngle=1.5708
    g13: LineSegment StartX=85.25 StartY=-43.75 StartZ=0 EndX=85.25 EndY=-47.25 EndZ=0
    g14: ArcOfCircle CenterX=83.25 CenterY=-47.25 CenterZ=0 NormalX=0 NormalY=0 NormalZ=1 AngleXU=0 Radius=2 StartAngle=4.71239 EndAngle=6.28319
    g15: LineSegment StartX=83.25 StartY=-49.25 StartZ=0 EndX=79.75 EndY=-49.25 EndZ=0
    g16: ArcOfCircle CenterX=79.75 CenterY=-47.25 CenterZ=0 NormalX=0 NormalY=0 NormalZ=1 AngleXU=0 Radius=2 StartAngle=3.14159 EndAngle=4.71239
    g17: LineSegment StartX=77.75 StartY=-47.25 StartZ=0 EndX=77.75 EndY=-43.75 EndZ=0
    g18: GeomPoint X=77.75 Y=-41.75 Z=0
    g19: GeomPoint X=85.25 Y=-49.25 Z=0
    g20: LineSegment StartX=79.75 StartY=-129.75 StartZ=0 EndX=83.25 EndY=-133.25 EndZ=0
    g21: LineSegment StartX=79.75 StartY=-133.25 StartZ=0 EndX=83.25 EndY=-129.75 EndZ=0
    g22: LineSegment StartX=79.75 StartY=-43.75 StartZ=0 EndX=83.25 EndY=-47.25 EndZ=0
    g23: LineSegment StartX=83.25 StartY=-43.75 StartZ=0 EndX=79.75 EndY=-47.25 EndZ=0
  constraints (56):
    c: Tangent(g0,g1) = 1.5708
    c: Tangent(g1,g2) = 1.5708
    c: Tangent(g2,g3) = 1.5708
    c: Tangent(g3,g4) = 1.5708
    c: Tangent(g4,g5) = 1.5708
    c: Tangent(g5,g6) = 1.5708
    c: Tangent(g6,g7) = 1.5708
    c: Tangent(g7,g0) = 1.5708
    c: Horizontal(g1)
    c: Horizontal(g5)
    c: Vertical(g3)
    c: Vertical(g7)
    c: Equal(g0,g2)
    c: Equal(g2,g4)
    c: Equal(g4,g6)
    c: PointOnObject(g8,g1)
    c: PointOnObject(g8,g7)
    c: PointOnObject(g9,g3)
    c: PointOnObject(g9,g5)
    c: Tangent(g10,g11) = 1.5708
    c: Tangent(g11,g12) = 1.5708
    c: Tangent(g12,g13) = 1.5708
    c: Tangent(g13,g14) = 1.5708
    c: Tangent(g14,g15) = 1.5708
    c: Tangent(g15,g16) = 1.5708
    c: Tangent(g16,g17) = 1.5708
    c: Tangent(g17,g10) = 1.5708
    c: Horizontal(g11)
    c: Horizontal(g15)
    c: Vertical(g13)
    c: Vertical(g17)
    c: Equal(g10,g12)
    c: Equal(g12,g14)
    c: Equal(g14,g16)
    c: PointOnObject(g18,g11)
    c: PointOnObject(g18,g17)
    c: PointOnObject(g19,g13)
    c: PointOnObject(g19,g15)
    c: Radius(g0) = 2
    c: Equal(g0,g10)
    c: Equal(g1,g7)
    c: Equal(g7,g11)
    c: Equal(g11,g17)
    c: DistanceX(g6,g3) = 7.5
    c: Coincident(g20,g0)
    c: Coincident(g20,g4)
    c: Coincident(g21,g6)
    c: Coincident(g21,g2)
    c: Coincident(g22,g10)
    c: Coincident(g22,g14)
    c: Coincident(g23,g12)
    c: Coincident(g23,g16)
    c: PointOnObject(g-3,g22)
    c: PointOnObject(g-3,g23)
    c: PointOnObject(g-4,g21)
    c: PointOnObject(g-4,g20)
FEATURE [PartDesign::Pocket] Pocket012  label="BottomScrewPockets"
  BaseFeature = -> Pad020
  Direction = (0,0,-1)
  Length = 5.5
  Length2 = 5
  Profile = -> Sketch044
  ReferenceAxis = -> Sketch044 [N_Axis]
  Reversed = true
  Type = 0
FEATURE [PartDesign::Plane] DatumPlane026  label="TopOfBottomOfKeyboardPlane"
  AttachmentOffset = pos=(0,0,64) rot=(0,1,0;0.200713rad)
  Length = 1000
  MapMode = 5
  Placement = pos=(0,0,64) rot=(0,1,0;0.200713rad)
  ResizeMode = 1
  Support = -> [XY_Plane035]
  Width = 350
FEATURE [Sketcher::SketchObject] Sketch045
  ExternalGeometry = -> [Pocket012]
  FullyConstrained = true
  MapMode = 5
  Placement = pos=(0,0,64) rot=(0,1,0;0.200713rad)
  Support = -> [DatumPlane026]
  sketch-geometry (16):
    g0: LineSegment StartX=226.068 StartY=-124.8 StartZ=0 EndX=228.268 EndY=-124.8 EndZ=0
    g1: LineSegment StartX=228.268 StartY=-124.8 StartZ=0 EndX=228.268 EndY=-136.8 EndZ=0
    g2: LineSegment StartX=228.268 StartY=-136.8 StartZ=0 EndX=226.068 EndY=-136.8 EndZ=0
    g3: LineSegment StartX=228.268 StartY=-40.3 StartZ=0 EndX=228.268 EndY=-52.3 EndZ=0
    g4: LineSegment StartX=226.068 StartY=-124.8 StartZ=0 EndX=223.068 EndY=-124.8 EndZ=0
    g5: LineSegment StartX=226.068 StartY=-136.8 StartZ=0 EndX=223.068 EndY=-136.8 EndZ=0
    g6: LineSegment StartX=221.068 StartY=-126.8 StartZ=0 EndX=221.068 EndY=-134.8 EndZ=0
    g7: ArcOfCircle CenterX=223.068 CenterY=-126.8 CenterZ=0 NormalX=0 NormalY=0 NormalZ=1 AngleXU=0 Radius=2 StartAngle=1.5708 EndAngle=3.14159
    g8: ArcOfCircle CenterX=223.068 CenterY=-134.8 CenterZ=0 NormalX=0 NormalY=0 NormalZ=1 AngleXU=0 Radius=2 StartAngle=3.14159 EndAngle=4.71239
    g9: LineSegment StartX=228.268 StartY=-40.3 StartZ=0 EndX=223.068 EndY=-40.3 EndZ=0
    g10: LineSegment StartX=228.268 StartY=-52.3 StartZ=0 EndX=223.068 EndY=-52.3 EndZ=0
    g11: LineSegment StartX=221.068 StartY=-42.3 StartZ=0 EndX=221.068 EndY=-50.3 EndZ=0
    g12: ArcOfCircle CenterX=223.068 CenterY=-42.3 CenterZ=0 NormalX=0 NormalY=0 NormalZ=1 AngleXU=0 Radius=2 StartAngle=1.5708 EndAngle=3.14159
    g13: ArcOfCircle CenterX=223.068 CenterY=-50.3 CenterZ=0 NormalX=0 NormalY=0 NormalZ=1 AngleXU=0 Radius=2 StartAngle=3.14159 EndAngle=4.71239
    g14: LineSegment StartX=221.068 StartY=-7.85 StartZ=0 EndX=228.268 EndY=-40.3 EndZ=0
    g15: LineSegment StartX=228.268 StartY=-136.8 StartZ=0 EndX=221.068 EndY=-169.25 EndZ=0
  constraints (50):
    c: Coincident(g0,g1)
    c: Vertical(g1)
    c: Coincident(g1,g2)
    c: Horizontal(g2)
    c: Vertical(g3)
    c: Vertical(g3,g1)
    c: Coincident(g4,g0)
    c: Horizontal(g4)
    c: Coincident(g5,g2)
    c: Horizontal(g5)
    c: Vertical(g6)
    c: Coincident(g7,g6)
    c: Coincident(g7,g4)
    c: Coincident(g8,g5)
    c: Coincident(g8,g6)
    c: Horizontal(g6,g7)
    c: Horizontal(g8,g6)
    c: Vertical(g5,g8)
    c: Vertical(g4,g7)
    c: Vertical(g7,g8)
    c: Horizontal(g0)
    c: DistanceX(g6,g0) = 5
    c: Vertical(g0,g2)
    c: Radius(g7) = 2
    c: DistanceY(g1,g1) = 12
    c: DistanceX(g0,g0) = 2.2
    c: Coincident(g9,g3)
    c: Horizontal(g9)
    c: Coincident(g10,g3)
    c: Horizontal(g10)
    c: Vertical(g11)
    c: Coincident(g12,g9)
    c: Coincident(g12,g11)
    c: Coincident(g13,g11)
    c: Coincident(g13,g10)
    c: Vertical(g12,g9)
    c: Vertical(g10,g13)
    c: Horizontal(g11,g12)
    c: Horizontal(g11,g13)
    c: Radius(g12) = 2
    c: Equal(g12,g13)
    c: Vertical(g11,g6)
    c: DistanceY(g3,g3) = 12
    c: Coincident(g14,g-3)
    c: Coincident(g14,g3)
    c: Coincident(g15,g1)
    c: Coincident(g15,g-3)
    c: Equal(g14,g15)
    c: PointOnObject(g11,g-3)
    c: DistanceY(g5,g9) = 96.5
FEATURE [PartDesign::Plane] DatumPlane027  label="UnderKeyboardPlane"
  AttachmentOffset = pos=(0,0,52) rot=(0,1,0;0.200713rad)
  Length = 841.351
  MapMode = 5
  Placement = pos=(0,0,52) rot=(0,1,0;0.200713rad)
  ResizeMode = 0
  Support = -> [XY_Plane035]
  Width = 733.331
FEATURE [Sketcher::SketchObject] Sketch048
  ExternalGeometry = -> [Fillet007]
  FullyConstrained = true
  MapMode = 5
  Placement = pos=(234.588,-7.73e-14,16.9004) rot=(0.099689,0.099689,0.990012;1.58083rad)
  Support = -> [Fillet007]
  sketch-geometry (4):
    g0: Circle CenterX=-46.35 CenterY=6.60888 CenterZ=0 NormalX=0 NormalY=0 NormalZ=1 AngleXU=0 Radius=1.5
    g1: Circle CenterX=-130.75 CenterY=6.60888 CenterZ=0 NormalX=0 NormalY=0 NormalZ=1 AngleXU=0 Radius=1.5
    g2: LineSegment StartX=-174.75 StartY=3.50888 StartZ=0 EndX=-130.75 EndY=6.60888 EndZ=0
    g3: LineSegment StartX=-46.35 StartY=6.60888 StartZ=0 EndX=-2.35 EndY=3.50888 EndZ=0
  constraints (10):
    c: Equal(g0,g1)
    c: Radius(g0) = 1.5
    c: Horizontal(g1,g0)
    c: Coincident(g2,g-3)
    c: Coincident(g2,g1)
    c: Coincident(g3,g0)
    c: Coincident(g3,g-3)
    c: Equal(g2,g3)
    c: DistanceX(g2,g2) = 44
    c: DistanceY(g2,g1) = 3.1
FEATURE [PartDesign::Pocket] Pocket015
  BaseFeature = -> Fillet007
  Direction = (-0.199368,-2e-16,-0.979925)
  Length = 8
  Length2 = 5
  Placement = pos=(231.15,-7.7e-14,5.1e-14) rot=(0,-1,0;1.5708rad)
  Profile = -> Sketch048
  ReferenceAxis = -> Sketch048 [N_Axis]
  Type = 0
FEATURE [PartDesign::Plane] DatumPlane028  label="BottomOfControlPcbPlane"
  AttachmentOffset = pos=(0,0,7) rot=(0,0,1;0rad)
  Length = 722.974
  MapMode = 5
  Placement = pos=(0,0,7) rot=(0,0,1;0rad)
  ResizeMode = 0
  Support = -> [XY_Plane035]
  Width = 722.974
FEATURE [Sketcher::SketchObject] Sketch051
  FullyConstrained = true
  MapMode = 5
  Placement = pos=(0,0,7) rot=(0,0,1;0rad)
  Support = -> [DatumPlane028]
  sketch-geometry (14):
    g0: Circle CenterX=8.625 CenterY=-79.5725 CenterZ=0 NormalX=0 NormalY=0 NormalZ=1 AngleXU=0 Radius=5
    g1: Circle CenterX=8.625 CenterY=-29.5725 CenterZ=0 NormalX=0 NormalY=0 NormalZ=1 AngleXU=0 Radius=5
    g2: Circle CenterX=64.375 CenterY=-79.5725 CenterZ=0 NormalX=0 NormalY=0 NormalZ=1 AngleXU=0 Radius=5
    g3: Circle CenterX=64.375 CenterY=-29.5725 CenterZ=0 NormalX=0 NormalY=0 NormalZ=1 AngleXU=0 Radius=5
    g4: LineSegment StartX=3.5 StartY=-7.9 StartZ=0 EndX=69.5 EndY=-7.9 EndZ=0
    g5: LineSegment StartX=69.5 StartY=-7.9 StartZ=0 EndX=69.5 EndY=-93.05 EndZ=0
    g6: LineSegment StartX=69.5 StartY=-93.05 StartZ=0 EndX=3.5 EndY=-93.05 EndZ=0
    g7: LineSegment StartX=3.5 StartY=-93.05 StartZ=0 EndX=3.5 EndY=-7.9 EndZ=0
    g8: LineSegment StartX=3.5 StartY=-7.9 StartZ=0 EndX=8.625 EndY=-29.5725 EndZ=0
    g9: LineSegment StartX=64.375 StartY=-29.5725 StartZ=0 EndX=69.5 EndY=-7.9 EndZ=0
    g10: Circle CenterX=8.625 CenterY=-29.5725 CenterZ=0 NormalX=0 NormalY=0 NormalZ=1 AngleXU=0 Radius=1.8
    g11: Circle CenterX=64.375 CenterY=-29.5725 CenterZ=0 NormalX=0 NormalY=0 NormalZ=1 AngleXU=0 Radius=1.8
    g12: Circle CenterX=64.375 CenterY=-79.5725 CenterZ=0 NormalX=0 NormalY=0 NormalZ=1 AngleXU=0 Radius=1.8
    g13: Circle CenterX=8.625 CenterY=-79.5725 CenterZ=0 NormalX=0 NormalY=0 NormalZ=1 AngleXU=0 Radius=1.8
  constraints (36):
    c: Equal(g0,g1)
    c: Equal(g2,g3)
    c: Equal(g0,g2)
    c: Diameter(g1) = 10
    c: Horizontal(g0,g2)
    c: Horizontal(g1,g3)
    c: Vertical(g0,g1)
    c: Vertical(g2,g3)
    c: DistanceX(g1,g3) = 55.75
    c: DistanceY(g0,g1) = 50
    c: Coincident(g4,g5)
    c: Coincident(g5,g6)
    c: Coincident(g6,g7)
    c: Coincident(g7,g4)
    c: Horizontal(g4)
    c: Horizontal(g6)
    c: Vertical(g5)
    c: Vertical(g7)
    c: DistanceX(g4,g4) = 66
    c: DistanceY(g7,g7) = 85.15
    c: Coincident(g8,g4)
    c: Coincident(g8,g1)
    c: Coincident(g9,g3)
    c: Coincident(g9,g4)
    c: Equal(g8,g9)
    c: DistanceY(g3,g4) = 21.6725
    c: Coincident(g10,g1)
    c: Coincident(g11,g3)
    c: Coincident(g12,g2)
    c: Coincident(g13,g0)
    c: Equal(g10,g11)
    c: Equal(g13,g12)
    c: Equal(g10,g13)
    c: Diameter(g10) = 3.6
    c: DistanceX(g-1,g4) = 3.5
    c: DistanceY(g4,g-1) = 7.9
FEATURE [PartDesign::Plane] DatumPlane029  label="BackOfInsidePlane"
  AttachmentOffset = pos=(0,0,3.1) rot=(0,0,1;0rad)
  Length = 722.974
  MapMode = 5
  Placement = pos=(3.1,-7e-16,7e-16) rot=(0.57735,0.57735,0.57735;2.0944rad)
  ResizeMode = 0
  Support = -> [YZ_Plane035]
  Width = 722.974
FEATURE [PartDesign::Plane] DatumPlane030  label="UndersidePlane"
  AttachmentOffset = pos=(0,0,57.5) rot=(0,1,0;0.200713rad)
  Length = 310.207
  MapMode = 5
  Placement = pos=(0,0,57.5) rot=(0,1,0;0.200713rad)
  ResizeMode = 0
  Support = -> [XY_Plane034]
  Width = 246.806
FEATURE [Sketcher::SketchObject] Sketch049
  FullyConstrained = true
  MapMode = 5
  Placement = pos=(-1.8e-15,0,57.5) rot=(0,1,0;0.200713rad)
  Support = -> [DatumPlane030]
  sketch-geometry (16):
    g0: LineSegment StartX=230.75 StartY=-43.85 StartZ=0 EndX=231.75 EndY=-43.85 EndZ=0
    g1: LineSegment StartX=233.75 StartY=-45.85 StartZ=0 EndX=233.75 EndY=-46.85 EndZ=0
    g2: LineSegment StartX=230.75 StartY=-48.85 StartZ=0 EndX=231.75 EndY=-48.85 EndZ=0
    g3: ArcOfCircle CenterX=231.75 CenterY=-45.85 CenterZ=0 NormalX=0 NormalY=0 NormalZ=1 AngleXU=0 Radius=2 StartAngle=9e-16 EndAngle=1.5708
    g4: ArcOfCircle CenterX=231.75 CenterY=-46.85 CenterZ=0 NormalX=0 NormalY=0 NormalZ=1 AngleXU=0 Radius=2 StartAngle=4.71239 EndAngle=6.28318
    g5: LineSegment StartX=230.75 StartY=-128.25 StartZ=0 EndX=231.75 EndY=-128.25 EndZ=0
    g6: LineSegment StartX=230.75 StartY=-133.25 StartZ=0 EndX=231.75 EndY=-133.25 EndZ=0
    g7: LineSegment StartX=233.75 StartY=-130.25 StartZ=0 EndX=233.75 EndY=-131.25 EndZ=0
    g8: ArcOfCircle CenterX=231.75 CenterY=-130.25 CenterZ=0 NormalX=0 NormalY=0 NormalZ=1 AngleXU=0 Radius=2 StartAngle=0 EndAngle=1.5708
    g9: ArcOfCircle CenterX=231.75 CenterY=-131.25 CenterZ=0 NormalX=0 NormalY=0 NormalZ=1 AngleXU=0 Radius=2 StartAngle=4.71239 EndAngle=6.28319
    g10: LineSegment StartX=228.75 StartY=-45.85 StartZ=0 EndX=228.75 EndY=-46.85 EndZ=0
    g11: LineSegment StartX=228.75 StartY=-130.25 StartZ=0 EndX=228.75 EndY=-131.25 EndZ=0
    g12: ArcOfCircle CenterX=230.75 CenterY=-45.85 CenterZ=0 NormalX=0 NormalY=0 NormalZ=1 AngleXU=0 Radius=2 StartAngle=1.5708 EndAngle=3.14159
    g13: ArcOfCircle CenterX=230.75 CenterY=-46.85 CenterZ=0 NormalX=0 NormalY=0 NormalZ=1 AngleXU=0 Radius=2 StartAngle=3.1416 EndAngle=4.71239
    g14: ArcOfCircle CenterX=230.75 CenterY=-130.25 CenterZ=0 NormalX=0 NormalY=0 NormalZ=1 AngleXU=0 Radius=2 StartAngle=1.5708 EndAngle=3.14159
    g15: ArcOfCircle CenterX=230.75 CenterY=-131.25 CenterZ=0 NormalX=0 NormalY=0 NormalZ=1 AngleXU=0 Radius=2 StartAngle=3.14159 EndAngle=4.71239
  constraints (56):
    c: Coincident(g3,g0)
    c: Coincident(g3,g1)
    c: Coincident(g4,g2)
    c: Coincident(g4,g1)
    c: Equal(g3,g4)
    c: Radius(g3) = 2
    c: Coincident(g8,g5)
    c: Coincident(g8,g7)
    c: Coincident(g9,g7)
    c: Coincident(g9,g6)
    c: Horizontal(g8,g7)
    c: Horizontal(g9,g7)
    c: Equal(g8,g9)
    c: Equal(g8,g4)
    c: DistanceY(g6,g5) = 5
    c: DistanceY(g5,g0) = 84.4
    c: DistanceX(g-1,g0) = 230.75
    c: DistanceY(g0,g-1) = 43.85
    c: Equal(g7,g6)
    c: Horizontal(g5)
    c: Horizontal(g6)
    c: Vertical(g6,g9)
    c: Vertical(g5,g8)
    c: Vertical(g9,g8)
    c: Equal(g6,g5)
    c: Horizontal(g2)
    c: Horizontal(g0)
    c: Vertical(g4,g2)
    c: Vertical(g3,g0)
    c: Vertical(g1)
    c: Vertical(g2,g5)
    c: Vertical(g0,g2)
    c: Equal(g6,g0)
    c: Vertical(g3,g4)
    c: Horizontal(g3,g1)
    c: Equal(g0,g1)
    c: Vertical(g10)
    c: Vertical(g11)
    c: Vertical(g10,g11)
    c: Horizontal(g10,g1)
    c: Horizontal(g10,g1)
    c: Horizontal(g11,g7)
    c: Horizontal(g11,g7)
    c: Coincident(g12,g10)
    c: Coincident(g12,g0)
    c: Coincident(g13,g10)
    c: Coincident(g13,g2)
    c: Coincident(g14,g11)
    c: Coincident(g14,g5)
    c: Coincident(g15,g11)
    c: Coincident(g15,g6)
    c: Horizontal(g12,g3)
    c: Horizontal(g13,g4)
    c: Vertical(g13,g2)
    c: Vertical(g15,g6)
    c: Vertical(g15,g14)
FEATURE [PartDesign::Pocket] Pocket016  label="FrontScrewPocket"
  BaseFeature = -> Pocket015
  Direction = (-0.199368,0,-0.979925)
  Length = 3.05
  Length2 = 5
  Placement = pos=(231.15,-7.7e-14,5.1e-14) rot=(0,-1,0;1.5708rad)
  Profile = -> Sketch049
  ReferenceAxis = -> Sketch049 [N_Axis]
  Reversed = true
  Type = 0
FEATURE [PartDesign::Plane] DatumPlane031
  AttachmentOffset = pos=(0,0,9) rot=(0,0,1;0rad)
  Length = 276.017
  MapMode = 5
  Placement = pos=(0,0,9) rot=(0,0,1;0rad)
  ResizeMode = 0
  Support = -> [XY_Plane036]
  Width = 72.5167
FEATURE [Sketcher::SketchObject] Sketch054
  FullyConstrained = true
  MapMode = 5
  Placement = pos=(0,0,9) rot=(0,0,1;0rad)
  Support = -> [DatumPlane031]
  sketch-geometry (4):
    g0: LineSegment StartX=61.7 StartY=-6 StartZ=0 EndX=76.5 EndY=-6 EndZ=0
    g1: LineSegment StartX=76.5 StartY=-6 StartZ=0 EndX=76.5 EndY=-10 EndZ=0
    g2: LineSegment StartX=76.5 StartY=-10 StartZ=0 EndX=61.7 EndY=-10 EndZ=0
    g3: LineSegment StartX=61.7 StartY=-10 StartZ=0 EndX=61.7 EndY=-6 EndZ=0
  constraints (12):
    c: Coincident(g0,g1)
    c: Coincident(g1,g2)
    c: Coincident(g2,g3)
    c: Coincident(g3,g0)
    c: Horizontal(g0)
    c: Horizontal(g2)
    c: Vertical(g1)
    c: Vertical(g3)
    c: DistanceY(g3,g3) = 4
    c: DistanceX(g2,g2) = 14.8
    c: DistanceX(g-1,g0) = 61.7
    c: DistanceY(g0,g-1) = 6
FEATURE [PartDesign::Plane] DatumPlane032
  AttachmentOffset = pos=(0,0,9) rot=(0,0,1;0rad)
  Length = 276.017
  MapMode = 5
  Placement = pos=(0,0,9) rot=(0,0,1;0rad)
  ResizeMode = 0
  Support = -> [XY_Plane037]
  Width = 72.5167
FEATURE [Sketcher::SketchObject] Sketch055
  FullyConstrained = true
  MapMode = 5
  Placement = pos=(0,0,9) rot=(0,0,1;0rad)
  Support = -> [DatumPlane032]
  sketch-geometry (4):
    g0: LineSegment StartX=65.5 StartY=10 StartZ=0 EndX=76.5 EndY=10 EndZ=0
    g1: LineSegment StartX=76.5 StartY=10 StartZ=0 EndX=76.5 EndY=6 EndZ=0
    g2: LineSegment StartX=76.5 StartY=6 StartZ=0 EndX=65.5 EndY=6 EndZ=0
    g3: LineSegment StartX=65.5 StartY=6 StartZ=0 EndX=65.5 EndY=10 EndZ=0
  constraints (12):
    c: Coincident(g0,g1)
    c: Coincident(g1,g2)
    c: Coincident(g2,g3)
    c: Coincident(g3,g0)
    c: Horizontal(g0)
    c: Horizontal(g2)
    c: Vertical(g1)
    c: Vertical(g3)
    c: DistanceX(g2,g2) = 11
    c: DistanceY(g1,g1) = 4
    c: DistanceX(g-1,g2) = 65.5
    c: DistanceY(g-1,g2) = 6
FEATURE [Sketcher::SketchObject] Sketch056
  ExternalGeometry = -> [Pad015]
  FullyConstrained = true
  MapMode = 5
  Placement = pos=(-1.8e-15,0,57.5) rot=(0,1,0;0.200713rad)
  Support = -> [DatumPlane030]
  sketch-geometry (6):
    g0: LineSegment StartX=94.9644 StartY=-6.3 StartZ=0 EndX=228.464 EndY=-6.3 EndZ=0
    g1: LineSegment StartX=228.464 StartY=-6.3 StartZ=0 EndX=228.464 EndY=-170.8 EndZ=0
    g2: LineSegment StartX=228.464 StartY=-170.8 StartZ=0 EndX=94.9644 EndY=-170.8 EndZ=0
    g3: LineSegment StartX=94.9644 StartY=-170.8 StartZ=0 EndX=94.9644 EndY=-6.3 EndZ=0
    g4: LineSegment StartX=228.464 StartY=-6.3 StartZ=0 EndX=234.464 EndY=-1.35 EndZ=0
    g5: LineSegment StartX=228.464 StartY=-170.8 StartZ=0 EndX=234.464 EndY=-175.75 EndZ=0
  constraints (16):
    c: Coincident(g0,g1)
    c: Coincident(g1,g2)
    c: Coincident(g2,g3)
    c: Coincident(g3,g0)
    c: Horizontal(g0)
    c: Horizontal(g2)
    c: Vertical(g1)
    c: Vertical(g3)
    c: DistanceX(g0,g0) = 133.5
    c: DistanceY(g3,g3) = 164.5
    c: Coincident(g4,g0)
    c: Coincident(g4,g-3)
    c: Coincident(g5,g1)
    c: Coincident(g5,g-3)
    c: Equal(g4,g5)
    c: DistanceX(g4,g4) = 6
FEATURE [PartDesign::Pocket] Pocket023  label="KeyboardHole"
  BaseFeature = -> Pocket016
  Direction = (-0.199368,0,-0.979925)
  Length = 10
  Length2 = 5
  Placement = pos=(231.15,-7.7e-14,5.1e-14) rot=(0,-1,0;1.5708rad)
  Profile = -> Sketch056
  ReferenceAxis = -> Sketch056 [N_Axis]
  Reversed = true
  Type = 0
FEATURE [PartDesign::Body] Body031  label="KeyboardBottom"
  Group = -> [DatumPlane020,Sketch032,ShapeBinder004,Pad015,Fillet007,Sketch048,Pocket015,Sketch049,DatumPlane030,Pocket016,Sketch056,Pocket023]
  Origin = -> Origin034
  Placement = pos=(-3,0,0) rot=(0,0,1;0rad)
  Tip = -> Pocket023
FEATURE [PartDesign::Plane] DatumPlane033  label="BottomOfKeyboardPcbPlane"
  AttachmentOffset = pos=(0,0,55.1807) rot=(0,1,0;0.200713rad)
  Length = 841.351
  MapMode = 5
  Placement = pos=(0,0,55.1807) rot=(0,1,0;0.200713rad)
  ResizeMode = 0
  Support = -> [XY_Plane035]
  Width = 733.331
  expr: .AttachmentOffset.Base.z = 64 - 9 * cos(11.5)
FEATURE [PartDesign::Plane] DatumPlane034  label="TopOfKeyboardPcbPlane"
  AttachmentOffset = pos=(0,0,62.0402) rot=(0,1,0;0.200713rad)
  Length = 841.351
  MapMode = 5
  Placement = pos=(0,0,62.0402) rot=(0,1,0;0.200713rad)
  ResizeMode = 0
  Support = -> [XY_Plane035]
  Width = 733.331
  expr: .AttachmentOffset.Base.z = 64 - 2 * cos(11.5)
FEATURE [PartDesign::Plane] DatumPlane035
  AttachmentOffset = pos=(0,0,219.2) rot=(1,0,0;0.200713rad)
  Length = 65.2242
  MapMode = 5
  Placement = pos=(219.2,-4.87e-14,4.87e-14) rot=(0.612272,0.612272,0.500247;2.2139rad)
  ResizeMode = 0
  Support = -> [YZ_Plane036]
  Width = 131.112
FEATURE [Sketcher::SketchObject] Sketch058
  FullyConstrained = true
  MapMode = 5
  Placement = pos=(219.2,-4.87e-14,4.97e-14) rot=(0.612272,0.612272,0.500247;2.2139rad)
  Support = -> [DatumPlane035]
  sketch-geometry (4):
    g0: LineSegment StartX=-21.3 StartY=17.7 StartZ=0 EndX=-6.3 EndY=17.7 EndZ=0
    g1: LineSegment StartX=-6.3 StartY=17.7 StartZ=0 EndX=-6.3 EndY=10.98 EndZ=0
    g2: LineSegment StartX=-6.3 StartY=10.98 StartZ=0 EndX=-21.3 EndY=10.98 EndZ=0
    g3: LineSegment StartX=-21.3 StartY=10.98 StartZ=0 EndX=-21.3 EndY=17.7 EndZ=0
  constraints (12):
    c: Coincident(g0,g1)
    c: Coincident(g1,g2)
    c: Coincident(g2,g3)
    c: Coincident(g3,g0)
    c: Horizontal(g0)
    c: Horizontal(g2)
    c: Vertical(g1)
    c: Vertical(g3)
    c: DistanceY(g1,g1) = 6.72
    c: DistanceX(g0,g0) = 15
    c: DistanceY(g-1,g0) = 17.7
    c: DistanceX(g0,g-1) = 6.3
FEATURE [Part::FeaturePython] Line065  # WARN: FeaturePython — macro-defined, semantics opaque (R4)
  Vertex1 = -> Line057 [Vertex2]
  Vertex2 = -> SplitCurve [Vertex2]
FEATURE [Surface::Filling] Surface042
  Anisotropy = false
  BoundaryEdges = -> [Line049,Line053,Line054,Line055,Line058,Line062,Line063,Line064,Line052,Line051,Line050]
  BoundaryOrder = [0,0,0,0,0,0,0,0,0,0,0]
  Degree = 3
  Iterations = 2
  MaximumDegree = 8
  MaximumSegments = 9
  PointsOnCurve = 15
  TolAngular = 0.01
  TolCurvature = 0.1
  Tolerance2d = 1e-05
  Tolerance3d = 0.0001
  UnboundEdges = -> [Interpolation_Curve001,Interpolation_Curve002,Line060,Line057,Line059,Line065]
  UnboundOrder = [0,0,0,0,0,0]
FEATURE [Part::Extrusion] Extrude001  label="RightWall"
  Base = -> Surface042
  Dir = (0,-1,0)
  DirMode = 0
  FaceMakerClass = Part::FaceMakerBullseye
  LengthFwd = 3
  LengthRev = 0
  Solid = true
  Symmetric = false
FEATURE [Part::Compound] Compound006  label="RightWallConstruction"
  Links = -> [Line049,Line050,Line051,Line052,Line053,Line054,Line055,Line056,Line057,Interpolation_Curve001,Surface042,Line058,Interpolation_Curve002,SplitCurve,Line060,Line062,Line064,Line063,Line065]
FEATURE [Part::FeaturePython] Clone013  label="LeftWall"  # Draft clone (typed FeaturePython)
  AttacherType = Attacher::AttachEngine3D
  Fuse = false
  Objects = -> [Extrude001]
  Placement = pos=(0,-177.05,0) rot=(0,0,1;0rad)
  Scale = (1,-1,1)
  expr: .Placement.Base.y = -<<Params>>.Width - 2.65
FEATURE [PartDesign::FeatureBase] BaseFeature003
  BaseFeature = -> Extrude001
FEATURE [PartDesign::Pocket] Pocket021  label="RightWallControlPcbClearance"
  BaseFeature = -> BaseFeature003
  Direction = (0,0,-1)
  Length = 50
  Length2 = 5
  Profile = -> Sketch054
  ReferenceAxis = -> Sketch054 [N_Axis]
  Reversed = true
  Type = 0
FEATURE [PartDesign::FeatureBase] BaseFeature004
  BaseFeature = -> Clone013
FEATURE [PartDesign::Pocket] Pocket025  label="RightKeyboardRail"
  BaseFeature = -> Pocket021
  Direction = (-0.979925,3e-16,0.199368)
  Length = 200
  Length2 = 2.2
  Profile = -> Sketch058
  ReferenceAxis = -> Sketch058 [N_Axis]
  Type = 4
FEATURE [PartDesign::Body] Body033  label="RightWallBody"
  BaseFeature = -> Extrude001
  Group = -> [BaseFeature003,DatumPlane031,Sketch054,Pocket021,DatumPlane035,Sketch058,Pocket025]
  Origin = -> Origin036
  Placement = pos=(-3,0,0) rot=(0,0,1;0rad)
  Tip = -> Pocket025
FEATURE [PartDesign::Pocket] Pocket026  label="LeftWallControlPcbClearance"
  BaseFeature = -> BaseFeature004
  Direction = (0,0,-1)
  Length = 50
  Length2 = 5
  Profile = -> Sketch055
  ReferenceAxis = -> Sketch055 [N_Axis]
  Reversed = true
  Type = 0
FEATURE [PartDesign::Plane] DatumPlane036
  AttachmentOffset = pos=(0,0,219.2) rot=(1,0,0;0.200713rad)
  Length = 65.2242
  MapMode = 5
  Placement = pos=(219.2,-4.87e-14,4.87e-14) rot=(0.612272,0.612272,0.500247;2.2139rad)
  ResizeMode = 0
  Support = -> [YZ_Plane037]
  Width = 131.112
FEATURE [Sketcher::SketchObject] Sketch059
  FullyConstrained = true
  MapMode = 5
  Placement = pos=(219.2,-4.87e-14,4.97e-14) rot=(0.612272,0.612272,0.500247;2.2139rad)
  Support = -> [DatumPlane036]
  sketch-geometry (4):
    g0: LineSegment StartX=6.3 StartY=17.72 StartZ=0 EndX=21.3 EndY=17.72 EndZ=0
    g1: LineSegment StartX=21.3 StartY=17.72 StartZ=0 EndX=21.3 EndY=11 EndZ=0
    g2: LineSegment StartX=21.3 StartY=11 StartZ=0 EndX=6.3 EndY=11 EndZ=0
    g3: LineSegment StartX=6.3 StartY=11 StartZ=0 EndX=6.3 EndY=17.72 EndZ=0
  constraints (12):
    c: Coincident(g0,g1)
    c: Coincident(g1,g2)
    c: Coincident(g2,g3)
    c: Coincident(g3,g0)
    c: Horizontal(g0)
    c: Horizontal(g2)
    c: Vertical(g1)
    c: Vertical(g3)
    c: DistanceX(g0,g0) = 15
    c: DistanceY(g1,g1) = 6.72
    c: DistanceX(g-1,g2) = 6.3
    c: DistanceY(g-1,g2) = 11
FEATURE [PartDesign::Pocket] Pocket027  label="LeftKeyboardRail"
  BaseFeature = -> Pocket026
  Direction = (-0.979925,3e-16,0.199368)
  Length = 200
  Length2 = 2.2
  Profile = -> Sketch059
  ReferenceAxis = -> Sketch059 [N_Axis]
  Type = 4
FEATURE [PartDesign::Body] Body034  label="LeftWallBody"
  BaseFeature = -> Clone013
  Group = -> [BaseFeature004,DatumPlane032,Sketch055,Pocket026,DatumPlane036,Sketch059,Pocket027]
  Origin = -> Origin037
  Placement = pos=(-3,-177.05,0) rot=(0,0,1;0rad)
  Tip = -> Pocket027
FEATURE [Sketcher::SketchObject] Sketch060
  FullyConstrained = true
  MapMode = 5
  Placement = pos=(0,0,2.9) rot=(0,0,1;0rad)
  Support = -> [DatumPlane024]
  sketch-geometry (2):
    g0: Circle CenterX=148 CenterY=-59.35 CenterZ=0 NormalX=0 NormalY=0 NormalZ=1 AngleXU=0 Radius=3
    g1: Circle CenterX=148 CenterY=-117.75 CenterZ=0 NormalX=0 NormalY=0 NormalZ=1 AngleXU=0 Radius=3
  constraints (6):
    c: Equal(g0,g1)
    c: Diameter(g0) = 6
    c: DistanceX(g-1,g0) = 148
    c: Vertical(g0,g1)
    c: DistanceY(g1,g0) = 58.4
    c: DistanceY(g0,g-1) = 59.35
FEATURE [PartDesign::Plane] DatumPlane037  label="UnderKeyboardPcbPlane"
  AttachmentOffset = pos=(0,0,55.2) rot=(0,1,0;0.200713rad)
  Length = 841.351
  MapMode = 5
  Placement = pos=(0,0,55.2) rot=(0,1,0;0.200713rad)
  ResizeMode = 0
  Support = -> [XY_Plane035]
  Width = 733.331
FEATURE [PartDesign::Pad] Pad023  label="KeyboardSupportPillars"
  Direction = (0,0,1)
  Length = 10
  Length2 = 10
  Placement = pos=(0,0,2.9) rot=(0,0,1;0rad)
  Profile = -> Sketch060
  ReferenceAxis = -> Sketch060 [N_Axis]
  Type = 3
  UpToFace = -> DatumPlane037
FEATURE [Sketcher::SketchObject] Sketch061
  ExternalGeometry = -> [DatumPlane028,Pad023]
  FullyConstrained = true
  MapMode = 5
  Placement = pos=(3.1,-7e-16,7e-16) rot=(0.57735,0.57735,0.57735;2.0944rad)
  Support = -> [DatumPlane029]
  sketch-geometry (4):
    g0: LineSegment StartX=-65.7225 StartY=10.5 StartZ=0 EndX=-57.2225 EndY=10.5 EndZ=0
    g1: LineSegment StartX=-57.2225 StartY=10.5 StartZ=0 EndX=-57.2225 EndY=7 EndZ=0
    g2: LineSegment StartX=-57.2225 StartY=7 StartZ=0 EndX=-65.7225 EndY=7 EndZ=0
    g3: LineSegment StartX=-65.7225 StartY=7 StartZ=0 EndX=-65.7225 EndY=10.5 EndZ=0
  constraints (12):
    c: Coincident(g0,g1)
    c: Coincident(g1,g2)
    c: Coincident(g2,g3)
    c: Coincident(g3,g0)
    c: Horizontal(g0)
    c: Horizontal(g2)
    c: Vertical(g1)
    c: Vertical(g3)
    c: DistanceY(g1,g1) = 3.5
    c: DistanceX(g0,g0) = 8.5
    c: PointOnObject(g2,g-3)
    c: DistanceX(g-4,g2) = 12.05
FEATURE [PartDesign::Pocket] Pocket028  label="ConfigSwitchWindow"
  Direction = (-1,1e-16,-1e-16)
  Length = 5
  Length2 = 5
  Profile = -> Sketch061
  ReferenceAxis = -> Sketch061 [N_Axis]
  Type = 0
FEATURE [PartDesign::Plane] DatumPlane038
  AttachmentOffset = pos=(0,0,-140) rot=(0,-1,0;0.593412rad)
  Length = 978.351
  MapMode = 5
  Placement = pos=(0,0,-140) rot=(0,-1,0;0.593412rad)
  ResizeMode = 0
  Support = -> [XY_Plane035]
  Width = 744.45
FEATURE [PartDesign::Pad] Pad021  label="BottomFrontScrewColumn"
  BaseFeature = -> Pocket012
  Direction = (0.199368,0,0.979925)
  Length = 12
  Length2 = 10
  Profile = -> Sketch045
  ReferenceAxis = -> Sketch045 [N_Axis]
  Reversed = true
  Type = 3
  UpToFace = -> DatumPlane038
FEATURE [Sketcher::SketchObject] Sketch046
  ExternalGeometry = -> [Pad021]
  FullyConstrained = true
  MapMode = 5
  Placement = pos=(0,0,64) rot=(0,1,0;0.200713rad)
  Support = -> [DatumPlane026]
  sketch-geometry (2):
    g0: Circle CenterX=229.75 CenterY=-46.35 CenterZ=0 NormalX=0 NormalY=0 NormalZ=1 AngleXU=0 Radius=1.5
    g1: Circle CenterX=229.75 CenterY=-130.69 CenterZ=0 NormalX=0 NormalY=0 NormalZ=1 AngleXU=0 Radius=1.5
  constraints (6):
    c: Equal(g0,g1)
    c: Diameter(g0) = 3
    c: DistanceY(g1,g0) = 84.34
    c: DistanceX(g-1,g0) = 229.75
    c: DistanceY(g0,g-1) = 46.35
    c: Vertical(g0,g1)
FEATURE [PartDesign::Pocket] Pocket013  label="FrontScrewHoles"
  Direction = (-0.199368,0,-0.979925)
  Length = 10
  Length2 = 5
  Profile = -> Sketch046
  ReferenceAxis = -> Sketch046 [N_Axis]
  Type = 0
FEATURE [Sketcher::SketchObject] Sketch047
  ExternalGeometry = -> [Pocket013,Sketch045]
  FullyConstrained = true
  MapMode = 5
  Placement = pos=(0,0,52) rot=(0,1,0;0.200713rad)
  Support = -> [DatumPlane027]
  sketch-geometry (28):
    g0: ArcOfCircle CenterX=226.725 CenterY=-45.8 CenterZ=0 NormalX=0 NormalY=0 NormalZ=1 AngleXU=0 Radius=2 StartAngle=1.5708 EndAngle=3.14159
    g1: LineSegment StartX=226.725 StartY=-43.8 StartZ=0 EndX=227.725 EndY=-43.8 EndZ=0
    g2: ArcOfCircle CenterX=227.725 CenterY=-45.8 CenterZ=0 NormalX=0 NormalY=0 NormalZ=1 AngleXU=0 Radius=2 StartAngle=5e-16 EndAngle=1.5708
    g3: LineSegment StartX=229.725 StartY=-45.8 StartZ=0 EndX=229.725 EndY=-46.8 EndZ=0
    g4: ArcOfCircle CenterX=227.725 CenterY=-46.8 CenterZ=0 NormalX=0 NormalY=0 NormalZ=1 AngleXU=0 Radius=2 StartAngle=4.71239 EndAngle=6.28319
    g5: LineSegment StartX=227.725 StartY=-48.8 StartZ=0 EndX=226.725 EndY=-48.8 EndZ=0
    g6: ArcOfCircle CenterX=226.725 CenterY=-46.8 CenterZ=0 NormalX=0 NormalY=0 NormalZ=1 AngleXU=0 Radius=2 StartAngle=3.14159 EndAngle=4.71239
    g7: LineSegment StartX=224.725 StartY=-46.8 StartZ=0 EndX=224.725 EndY=-45.8 EndZ=0
    g8: GeomPoint X=224.725 Y=-43.8 Z=0
    g9: ArcOfCircle CenterX=226.725 CenterY=-130.3 CenterZ=0 NormalX=0 NormalY=0 NormalZ=1 AngleXU=0 Radius=2 StartAngle=1.5708 EndAngle=3.14159
    g10: LineSegment StartX=226.725 StartY=-128.3 StartZ=0 EndX=227.725 EndY=-128.3 EndZ=0
    g11: ArcOfCircle CenterX=227.725 CenterY=-130.3 CenterZ=0 NormalX=0 NormalY=0 NormalZ=1 AngleXU=0 Radius=2 StartAngle=-3.6e-15 EndAngle=1.5708
    g12: LineSegment StartX=229.725 StartY=-130.3 StartZ=0 EndX=229.725 EndY=-131.3 EndZ=0
    g13: ArcOfCircle CenterX=227.725 CenterY=-131.3 CenterZ=0 NormalX=0 NormalY=0 NormalZ=1 AngleXU=0 Radius=2 StartAngle=4.71239 EndAngle=6.28319
    g14: LineSegment StartX=227.725 StartY=-133.3 StartZ=0 EndX=226.725 EndY=-133.3 EndZ=0
    g15: ArcOfCircle CenterX=226.725 CenterY=-131.3 CenterZ=0 NormalX=0 NormalY=0 NormalZ=1 AngleXU=0 Radius=2 StartAngle=3.14159 EndAngle=4.71239
    g16: LineSegment StartX=224.725 StartY=-131.3 StartZ=0 EndX=224.725 EndY=-130.3 EndZ=0
    g17: GeomPoint X=224.725 Y=-128.3 Z=0
    g18: LineSegment StartX=226.725 StartY=-131.3 StartZ=0 EndX=227.725 EndY=-130.3 EndZ=0
    g19: LineSegment StartX=226.725 StartY=-130.3 StartZ=0 EndX=227.725 EndY=-131.3 EndZ=0
    g20: LineSegment StartX=226.725 StartY=-46.8 StartZ=0 EndX=227.725 EndY=-45.8 EndZ=0
    g21: LineSegment StartX=226.725 StartY=-45.8 StartZ=0 EndX=227.725 EndY=-46.8 EndZ=0
    g22: GeomPoint X=227.225 Y=-46.3 Z=0
    g23: GeomPoint X=227.225 Y=-130.8 Z=0
    g24: LineSegment StartX=225.875 StartY=-124.8 StartZ=0 EndX=227.225 EndY=-130.8 EndZ=0
    g25: LineSegment StartX=225.875 StartY=-136.8 StartZ=0 EndX=227.225 EndY=-130.8 EndZ=0
    g26: LineSegment StartX=225.875 StartY=-52.3 StartZ=0 EndX=227.225 EndY=-46.3 EndZ=0
    g27: LineSegment StartX=227.225 StartY=-46.3 StartZ=0 EndX=225.875 EndY=-40.3 EndZ=0
  constraints (64):
    c: Tangent(g0,g1) = 1.5708
    c: Tangent(g1,g2) = 1.5708
    c: Tangent(g2,g3) = 1.5708
    c: Tangent(g3,g4) = 1.5708
    c: Tangent(g4,g5) = 1.5708
    c: Tangent(g5,g6) = 1.5708
    c: Tangent(g6,g7) = 1.5708
    c: Tangent(g7,g0) = 1.5708
    c: Horizontal(g1)
    c: Horizontal(g5)
    c: Vertical(g3)
    c: Vertical(g7)
    c: Equal(g0,g2)
    c: Equal(g2,g4)
    c: Equal(g4,g6)
    c: PointOnObject(g8,g1)
    c: PointOnObject(g8,g7)
    c: Tangent(g9,g10) = 1.5708
    c: Tangent(g10,g11) = 1.5708
    c: Tangent(g11,g12) = 1.5708
    c: Tangent(g12,g13) = 1.5708
    c: Tangent(g13,g14) = 1.5708
    c: Tangent(g14,g15) = 1.5708
    c: Tangent(g15,g16) = 1.5708
    c: Tangent(g16,g9) = 1.5708
    c: Horizontal(g10)
    c: Horizontal(g14)
    c: Vertical(g12)
    c: Vertical(g16)
    c: Equal(g9,g11)
    c: Equal(g11,g13)
    c: Equal(g13,g15)
    c: PointOnObject(g17,g10)
    c: PointOnObject(g17,g16)
    c: Coincident(g18,g15)
    c: Coincident(g18,g11)
    c: Coincident(g19,g9)
    c: Coincident(g19,g13)
    c: Coincident(g20,g6)
    c: Coincident(g20,g2)
    c: Coincident(g21,g0)
    c: Coincident(g21,g4)
    c: Radius(g0) = 2
    c: Radius(g9) = 2
    c: DistanceY(g13,g10) = 5
    c: DistanceX(g9,g11) = 5
    c: DistanceY(g4,g1) = 5
    c: Vertical(g6,g9)
    c: PointOnObject(g23,g18)
    c: PointOnObject(g23,g19)
    c: PointOnObject(g22,g21)
    c: PointOnObject(g22,g20)
    c: Vertical(g3,g11)
    c: Coincident(g24,g-7)
    c: Coincident(g24,g23)
    c: Coincident(g25,g-7)
    c: Coincident(g25,g23)
    c: Coincident(g26,g-8)
    c: Coincident(g26,g22)
    c: Coincident(g27,g-8)
    c: Equal(g27,g26)
    c: Equal(g24,g25)
    c: Coincident(g27,g22)
    c: DistanceX(g27,g22) = 1.35
FEATURE [PartDesign::Pocket] Pocket014  label="FrontUnderScrewPockets"
  BaseFeature = -> Pocket013
  Direction = (-0.199368,0,-0.979925)
  Length = 8
  Length2 = 5
  Profile = -> Sketch047
  ReferenceAxis = -> Sketch047 [N_Axis]
  Reversed = true
  Type = 0
FEATURE [Sketcher::SketchObject] Sketch050
  ExternalGeometry = -> [Pocket014]
  FullyConstrained = true
  MapMode = 5
  Support = -> [DatumPlane025]
  sketch-geometry (4):
    g0: Circle CenterX=12.5 CenterY=-23.85 CenterZ=0 NormalX=0 NormalY=0 NormalZ=1 AngleXU=0 Radius=6.5
    g1: Circle CenterX=12.5 CenterY=-153.25 CenterZ=0 NormalX=0 NormalY=0 NormalZ=1 AngleXU=0 Radius=6.5
    g2: Circle CenterX=192.5 CenterY=-153.25 CenterZ=0 NormalX=0 NormalY=0 NormalZ=1 AngleXU=0 Radius=6.5
    g3: Circle CenterX=192.5 CenterY=-23.85 CenterZ=0 NormalX=0 NormalY=0 NormalZ=1 AngleXU=0 Radius=6.5
  constraints (12):
    c: Equal(g0,g3)
    c: Equal(g1,g2)
    c: Equal(g0,g1)
    c: Diameter(g0) = 13
    c: Vertical(g0,g1)
    c: Vertical(g3,g2)
    c: Horizontal(g3,g0)
    c: Horizontal(g1,g2)
    c: DistanceY(g0,g-4) = 17
    c: DistanceY(g-3,g1) = 17
    c: DistanceX(g-3,g1) = 9
    c: DistanceX(g0,g3) = 180
FEATURE [PartDesign::Pocket] Pocket018  label="RubberFeetPockets"
  Direction = (0,0,-1)
  Length = 1.7
  Length2 = 5
  Profile = -> Sketch050
  ReferenceAxis = -> Sketch050 [N_Axis]
  Reversed = true
  Type = 0
FEATURE [PartDesign::Pad] Pad022  label="ControlBoardSupportPillars"
  BaseFeature = -> Pocket018
  Direction = (0,0,1)
  Length = 4.5
  Length2 = 10
  Profile = -> Sketch051
  ReferenceAxis = -> Sketch051 [N_Axis]
  Reversed = true
  Type = 0
FEATURE [Sketcher::SketchObject] Sketch052
  ExternalGeometry = -> [Pad022]
  FullyConstrained = true
  MapMode = 5
  Placement = pos=(3.1,-7e-16,7e-16) rot=(0.57735,0.57735,0.57735;2.0944rad)
  Support = -> [DatumPlane029]
  sketch-geometry (4):
    g0: LineSegment StartX=-93.85 StartY=8.8 StartZ=0 EndX=-7.35 EndY=8.8 EndZ=0
    g1: LineSegment StartX=-7.35 StartY=8.8 StartZ=0 EndX=-7.35 EndY=7 EndZ=0
    g2: LineSegment StartX=-7.35 StartY=7 StartZ=0 EndX=-93.85 EndY=7 EndZ=0
    g3: LineSegment StartX=-93.85 StartY=7 StartZ=0 EndX=-93.85 EndY=8.8 EndZ=0
  constraints (12):
    c: Horizontal(g0)
    c: Vertical(g3)
    c: Vertical(g1)
    c: Horizontal(g2)
    c: DistanceX(g0,g0) = 86.5
    c: DistanceY(g3,g3) = 1.8
    c: Coincident(g2,g3)
    c: Coincident(g2,g1)
    c: Coincident(g1,g0)
    c: Coincident(g0,g3)
    c: PointOnObject(g-3,g2)
    c: DistanceX(g-3,g1) = 0.5
FEATURE [PartDesign::Pocket] Pocket019  label="BackOfControlPcbSlot"
  BaseFeature = -> Pocket018
  Direction = (-1,1e-16,-1e-16)
  Length = 2
  Length2 = 5
  Profile = -> Sketch052
  ReferenceAxis = -> Sketch052 [N_Axis]
  Type = 0
FEATURE [Sketcher::SketchObject] Sketch053
  ExternalGeometry = -> [Pocket019]
  FullyConstrained = true
  MapMode = 5
  Placement = pos=(0,0,7) rot=(0,0,1;0rad)
  Support = -> [DatumPlane028]
  sketch-geometry (4):
    g0: LineSegment StartX=73 StartY=-5.95 StartZ=0 EndX=73 EndY=-170.95 EndZ=0
    g1: LineSegment StartX=73 StartY=-170.95 StartZ=0 EndX=3 EndY=-170.95 EndZ=0
    g2: LineSegment StartX=3 StartY=-170.95 StartZ=0 EndX=3 EndY=-5.95 EndZ=0
    g3: LineSegment StartX=3 StartY=-5.95 StartZ=0 EndX=73 EndY=-5.95 EndZ=0
  constraints (12):
    c: Coincident(g0,g1)
    c: Coincident(g1,g2)
    c: Horizontal(g1)
    c: Vertical(g0)
    c: Vertical(g2)
    c: DistanceX(g2,g0) = 70
    c: DistanceY(g0,g0) = 165
    c: Coincident(g3,g2)
    c: Coincident(g3,g0)
    c: Horizontal(g3)
    c: PointOnObject(g-3,g2)
    c: DistanceY(g-3,g2) = 1.9
FEATURE [PartDesign::Pocket] Pocket020  label="ControlPcbClearance"
  BaseFeature = -> Pocket019
  Direction = (0,0,-1)
  Length = 80
  Length2 = 5
  Profile = -> Sketch053
  ReferenceAxis = -> Sketch053 [N_Axis]
  Reversed = true
  Type = 0
FEATURE [Sketcher::SketchObject] Sketch057
  ExternalGeometry = -> [DatumPlane034,DatumPlane033]
  FullyConstrained = true
  MapMode = 5
  Placement = pos=(204.126,0,-41.53) rot=(0.534673,-0.534673,-0.654407;1.98266rad)
  Support = -> [Pocket020]
  sketch-geometry (4):
    g0: LineSegment StartX=6.26 StartY=60.7947 StartZ=0 EndX=170.76 EndY=60.7947 EndZ=0
    g1: LineSegment StartX=170.76 StartY=60.7947 StartZ=0 EndX=170.76 EndY=54.0729 EndZ=0
    g2: LineSegment StartX=170.76 StartY=54.0729 StartZ=0 EndX=6.26 EndY=54.0729 EndZ=0
    g3: LineSegment StartX=6.26 StartY=54.0729 StartZ=0 EndX=6.26 EndY=60.7947 EndZ=0
  constraints (12):
    c: Coincident(g0,g1)
    c: Coincident(g1,g2)
    c: Coincident(g2,g3)
    c: Coincident(g3,g0)
    c: Horizontal(g0)
    c: Horizontal(g2)
    c: Vertical(g1)
    c: Vertical(g3)
    c: DistanceX(g2,g2) = 164.5
    c: PointOnObject(g1,g-4)
    c: PointOnObject(g0,g-3)
    c: DistanceX(g-1,g2) = 6.26
FEATURE [PartDesign::Pocket] Pocket024  label="BottomEndOfKeyboardPcb"
  Direction = (0.979925,0,-0.199368)
  Length = 6
  Length2 = 130.5
  Profile = -> Sketch057
  ReferenceAxis = -> Sketch057 [N_Axis]
  Type = 4
FEATURE [Sketcher::SketchObject] Sketch062
  ExternalGeometry = -> [Pocket028]
  FullyConstrained = true
  MapMode = 5
  Placement = pos=(0,0,0) rot=(0.57735,-0.57735,-0.57735;2.0944rad)
  Support = -> [Pocket028]
  sketch-geometry (42):
    g0: LineSegment StartX=66.7225 StartY=8.85 StartZ=0 EndX=67.4725 EndY=7.55096 EndZ=0
    g1: LineSegment StartX=68.4251 StartY=7.00096 StartZ=0 EndX=72.9251 EndY=7.00096 EndZ=0
    g2: LineSegment StartX=73.8778 StartY=7.55096 StartZ=0 EndX=74.6278 EndY=8.85 EndZ=0
    g3: LineSegment StartX=73.6751 StartY=10.5 StartZ=0 EndX=67.6751 EndY=10.5 EndZ=0
    g4: ArcOfCircle CenterX=67.6751 CenterY=9.4 CenterZ=0 NormalX=0 NormalY=0 NormalZ=1 AngleXU=0 Radius=1.1 StartAngle=1.5708 EndAngle=3.66519
    g5: ArcOfCircle CenterX=73.6751 CenterY=9.4 CenterZ=0 NormalX=0 NormalY=0 NormalZ=1 AngleXU=0 Radius=1.1 StartAngle=5.75959 EndAngle=7.85398
    g6: ArcOfCircle CenterX=72.9251 CenterY=8.10096 CenterZ=0 NormalX=0 NormalY=0 NormalZ=1 AngleXU=0 Radius=1.1 StartAngle=4.71239 EndAngle=5.75959
    g7: ArcOfCircle CenterX=68.4251 CenterY=8.10096 CenterZ=0 NormalX=0 NormalY=0 NormalZ=1 AngleXU=0 Radius=1.1 StartAngle=3.66519 EndAngle=4.71239
    g8: Circle CenterX=67.6751 CenterY=9.4 CenterZ=0 NormalX=0 NormalY=0 NormalZ=1 AngleXU=0 Radius=0.5
    g9: Circle CenterX=69.1751 CenterY=9.4 CenterZ=0 NormalX=0 NormalY=0 NormalZ=1 AngleXU=0 Radius=0.5
    g10: Circle CenterX=70.6751 CenterY=9.4 CenterZ=0 NormalX=0 NormalY=0 NormalZ=1 AngleXU=0 Radius=0.5
    g11: Circle CenterX=72.1751 CenterY=9.4 CenterZ=0 NormalX=0 NormalY=0 NormalZ=1 AngleXU=0 Radius=0.5
    g12: Circle CenterX=73.6751 CenterY=9.4 CenterZ=0 NormalX=0 NormalY=0 NormalZ=1 AngleXU=0 Radius=0.5
    g13: Circle CenterX=68.4251 CenterY=8.10096 CenterZ=0 NormalX=0 NormalY=0 NormalZ=1 AngleXU=0 Radius=0.5
    g14: Circle CenterX=69.9251 CenterY=8.10096 CenterZ=0 NormalX=0 NormalY=0 NormalZ=1 AngleXU=0 Radius=0.5
    g15: Circle CenterX=71.4251 CenterY=8.10096 CenterZ=0 NormalX=0 NormalY=0 NormalZ=1 AngleXU=0 Radius=0.5
    g16: Circle CenterX=72.9251 CenterY=8.10096 CenterZ=0 NormalX=0 NormalY=0 NormalZ=1 AngleXU=0 Radius=0.5
    g17: LineSegment StartX=67.6751 StartY=9.4 StartZ=0 EndX=68.4251 EndY=8.10096 EndZ=0
    g18: LineSegment StartX=68.4251 StartY=8.10096 StartZ=0 EndX=69.1751 EndY=9.4 EndZ=0
    g19: LineSegment StartX=69.1751 StartY=9.4 StartZ=0 EndX=69.9251 EndY=8.10096 EndZ=0
    g20: LineSegment StartX=69.9251 StartY=8.10096 StartZ=0 EndX=70.6751 EndY=9.4 EndZ=0
    g21: LineSegment StartX=70.6751 StartY=9.4 StartZ=0 EndX=71.4251 EndY=8.10096 EndZ=0
    g22: LineSegment StartX=71.4251 StartY=8.10096 StartZ=0 EndX=72.1751 EndY=9.4 EndZ=0
    g23: LineSegment StartX=72.1751 StartY=9.4 StartZ=0 EndX=72.9251 EndY=8.10096 EndZ=0
    g24: LineSegment StartX=72.9251 StartY=8.10096 StartZ=0 EndX=73.6751 EndY=9.4 EndZ=0
    g25: LineSegment StartX=67.6751 StartY=9.4 StartZ=0 EndX=69.1751 EndY=9.4 EndZ=0
    g26: LineSegment StartX=69.1751 StartY=9.4 StartZ=0 EndX=70.6751 EndY=9.4 EndZ=0
    g27: LineSegment StartX=70.6751 StartY=9.4 StartZ=0 EndX=72.1751 EndY=9.4 EndZ=0
    g28: LineSegment StartX=72.1751 StartY=9.4 StartZ=0 EndX=73.6751 EndY=9.4 EndZ=0
    g29: LineSegment StartX=57.2225 StartY=10.5 StartZ=0 EndX=65.7225 EndY=10.5 EndZ=0
    g30: LineSegment StartX=51.7225 StartY=9.5 StartZ=0 EndX=55.7225 EndY=9.5 EndZ=0
    g31: LineSegment StartX=55.7225 StartY=9.5 StartZ=0 EndX=55.7225 EndY=4.5 EndZ=0
    g32: LineSegment StartX=55.7225 StartY=4.5 StartZ=0 EndX=51.7225 EndY=4.5 EndZ=0
    g33: LineSegment StartX=51.7225 StartY=4.5 StartZ=0 EndX=51.7225 EndY=9.5 EndZ=0
    g34: LineSegment StartX=51.4725 StartY=9.5 StartZ=0 EndX=48.4725 EndY=9.5 EndZ=0
    g35: LineSegment StartX=48.4725 StartY=9.5 StartZ=0 EndX=48.4725 EndY=6.5 EndZ=0
    g36: LineSegment StartX=48.4725 StartY=6.5 StartZ=0 EndX=51.4725 EndY=6.5 EndZ=0
    g37: LineSegment StartX=51.4725 StartY=6.5 StartZ=0 EndX=51.4725 EndY=9.5 EndZ=0
    g38: LineSegment StartX=49.7225 StartY=10 StartZ=0 EndX=50.7225 EndY=11 EndZ=0
    g39: LineSegment StartX=50.7225 StartY=11 StartZ=0 EndX=56.7225 EndY=11 EndZ=0
    g40: LineSegment StartX=56.7225 StartY=11 StartZ=0 EndX=55.7225 EndY=10 EndZ=0
    g41: LineSegment StartX=55.7225 StartY=10 StartZ=0 EndX=49.7225 EndY=10 EndZ=0
  constraints (107):
    c: Horizontal(g1)
    c: Horizontal(g3)
    c: Angle(g0,g3) = 1.0472
    c: Angle(g3,g2) = 1.0472
    c: Tangent(g0,g4) = -1.5708
    c: Tangent(g3,g4) = -1.5708
    c: Tangent(g3,g5) = -1.5708
    c: Tangent(g2,g5) = -1.5708
    c: Tangent(g2,g6) = -1.5708
    c: Tangent(g1,g6) = -1.5708
    c: Tangent(g1,g7) = -1.5708
    c: Tangent(g0,g7) = -1.5708
    c: Radius(g4) = 1.1
    c: Equal(g4,g5)
    c: Equal(g6,g7)
    c: Equal(g4,g7)
    c: Equal(g8,g9)
    c: Equal(g9,g10)
    c: Equal(g10,g11)
    c: Equal(g11,g12)
    c: Equal(g12,g16)
    c: Equal(g16,g15)
    c: Equal(g15,g14)
    c: Equal(g14,g13)
    c: Radius(g8) = 0.5
    c: Horizontal(g8,g9)
    c: Horizontal(g9,g10)
    c: Horizontal(g10,g11)
    c: Horizontal(g11,g12)
    c: Horizontal(g13,g14)
    c: Horizontal(g14,g15)
    c: Horizontal(g15,g16)
    c: Coincident(g17,g8)
    c: Coincident(g17,g13)
    c: Coincident(g18,g13)
    c: Coincident(g18,g9)
    c: Coincident(g19,g14)
    c: Coincident(g20,g10)
    c: Coincident(g21,g15)
    c: Coincident(g22,g11)
    c: Coincident(g23,g16)
    c: Coincident(g24,g16)
    c: Coincident(g24,g12)
    c: Equal(g17,g18)
    c: Equal(g18,g19)
    c: Equal(g19,g20)
    c: Equal(g20,g21)
    c: Equal(g21,g22)
    c: Equal(g22,g23)
    c: Equal(g23,g24)
    c: Coincident(g25,g8)
    c: Coincident(g25,g9)
    c: Coincident(g26,g9)
    c: Coincident(g26,g10)
    c: Coincident(g27,g10)
    c: Coincident(g27,g11)
    c: Coincident(g28,g11)
    c: Coincident(g28,g12)
    c: Coincident(g11,g23)
    c: Equal(g17,g25)
    c: Coincident(g9,g19)
    c: Coincident(g20,g14)
    c: Coincident(g21,g10)
    c: Coincident(g22,g15)
    c: DistanceX(g25,g25) = 1.5
    c: Coincident(g5,g12)
    c: Coincident(g7,g13)
    c: Coincident(g29,g-3)
    c: Coincident(g29,g-4)
    c: PointOnObject(g3,g29)
    c: DistanceX(g29,g0) = 1
    c: Coincident(g30,g31)
    c: Coincident(g31,g32)
    c: Coincident(g32,g33)
    c: Coincident(g33,g30)
    c: Horizontal(g30)
    c: Horizontal(g32)
    c: Vertical(g31)
    c: Vertical(g33)
    c: DistanceX(g30,g30) = 4
    c: DistanceY(g33,g33) = 5
    c: DistanceX(g30,g29) = 1.5
    c: Coincident(g34,g35)
    c: Coincident(g35,g36)
    c: Coincident(g36,g37)
    c: Coincident(g37,g34)
    c: Horizontal(g34)
    c: Horizontal(g36)
    c: Vertical(g35)
    c: Vertical(g37)
    c: DistanceX(g34,g30) = 0.25
    c: DistanceX(g34,g34) = 3
    c: DistanceY(g35,g35) = 3
    c: Horizontal(g34,g30)
    c: Coincident(g38,g39)
    c: Horizontal(g39)
    c: Coincident(g39,g40)
    c: Coincident(g40,g41)
    c: Coincident(g41,g38)
    c: Horizontal(g41)
    c: Angle(g41,g38) = 0.785398
    c: DistanceX(g39,g39) = 6
    c: Equal(g38,g40)
    c: Vertical(g40,g30)
    c: DistanceY(g38,g38) = 1
    c: DistanceY(g30,g40) = 0.5
    c: DistanceY(g29,g39) = 0.5
FEATURE [PartDesign::Pad] Pad024  label="ConfigGlyphs"
  BaseFeature = -> Pocket028
  Direction = (-1,0,0)
  Length = 0.5
  Length2 = 10
  Profile = -> Sketch062
  ReferenceAxis = -> Sketch062 [N_Axis]
  Type = 0
FEATURE [PartDesign::Plane] DatumPlane039  label="StructurePlane1"
  AttachmentOffset = pos=(0,-4,0) rot=(0,1,0;0.925025rad)
  Length = 986.337
  MapMode = 5
  Placement = pos=(9e-16,-9e-16,-4) rot=(0.230238,0.68811,0.68811;2.689rad)
  ResizeMode = 0
  Support = -> [YZ_Plane035]
  Width = 745.074
FEATURE [Sketcher::SketchObject] Sketch063
  ExternalGeometry = -> [Pad024]
  FullyConstrained = true
  MapMode = 5
  Placement = pos=(9e-16,-9e-16,-4) rot=(0.230238,0.68811,0.68811;2.689rad)
  Support = -> [DatumPlane039]
  sketch-geometry (5):
    g0: LineSegment StartX=-251.27 StartY=7 StartZ=0 EndX=-249.77 EndY=7 EndZ=0
    g1: LineSegment StartX=-249.77 StartY=7 StartZ=0 EndX=-249.77 EndY=8.5 EndZ=0
    g2: LineSegment StartX=-249.77 StartY=8.5 StartZ=0 EndX=-251.27 EndY=8.5 EndZ=0
    g3: LineSegment StartX=-251.27 StartY=8.5 StartZ=0 EndX=-251.27 EndY=7 EndZ=0
    g4: LineSegment StartX=-100.341 StartY=7 StartZ=0 EndX=-259.27 EndY=7 EndZ=0
  constraints (14):
    c: Coincident(g0,g1)
    c: Coincident(g1,g2)
    c: Coincident(g2,g3)
    c: Coincident(g3,g0)
    c: Horizontal(g0)
    c: Horizontal(g2)
    c: Vertical(g1)
    c: Vertical(g3)
    c: DistanceX(g2,g2) = 1.5
    c: DistanceY(g1,g1) = 1.5
    c: Coincident(g4,g-4)
    c: Coincident(g4,g-3)
    c: PointOnObject(g0,g4)
    c: DistanceX(g4,g0) = 8
FEATURE [PartDesign::Pad] Pad025
  Direction = (0.601815,0.798636,0)
  Length = 300
  Length2 = 10
  Midplane = true
  Profile = -> Sketch063
  ReferenceAxis = -> Sketch063 [N_Axis]
  Type = 0
FEATURE [PartDesign::LinearPattern] LinearPattern
  BaseFeature = -> Pad025
  Direction = -> Sketch063 [H_Axis]
  Length = 240
  Occurrences = 15
  Originals = -> [Pad025]
FEATURE [PartDesign::Plane] DatumPlane040  label="StructurePlane2"
  AttachmentOffset = pos=(-120,0,0) rot=(0,1,0;1.97222rad)
  Length = 927.97
  MapMode = 5
  Placement = pos=(-2.66e-14,-120,2.66e-14) rot=(-0.142396,0.699901,0.699901;3.42448rad)
  ResizeMode = 0
  Support = -> [YZ_Plane035]
  Width = 740.457
FEATURE [Sketcher::SketchObject] Sketch064
  ExternalGeometry = -> [LinearPattern]
  FullyConstrained = true
  MapMode = 5
  Placement = pos=(-2.84e-14,-120,2.66e-14) rot=(-0.142396,0.699901,0.699901;3.42448rad)
  Support = -> [DatumPlane040]
  sketch-geometry (5):
    g0: LineSegment StartX=-169.238 StartY=3 StartZ=0 EndX=13.9422 EndY=3 EndZ=0
    g1: LineSegment StartX=-220.558 StartY=3 StartZ=0 EndX=-219.058 EndY=3 EndZ=0
    g2: LineSegment StartX=-219.058 StartY=3 StartZ=0 EndX=-219.058 EndY=4.5 EndZ=0
    g3: LineSegment StartX=-219.058 StartY=4.5 StartZ=0 EndX=-220.558 EndY=4.5 EndZ=0
    g4: LineSegment StartX=-220.558 StartY=4.5 StartZ=0 EndX=-220.558 EndY=3 EndZ=0
  constraints (14):
    c: Coincident(g0,g-3)
    c: Coincident(g0,g-4)
    c: Coincident(g1,g2)
    c: Coincident(g2,g3)
    c: Coincident(g3,g4)
    c: Coincident(g4,g1)
    c: Horizontal(g1)
    c: Horizontal(g3)
    c: Vertical(g2)
    c: Vertical(g4)
    c: PointOnObject(g1,g0)
    c: DistanceX(g3,g3) = 1.5
    c: DistanceY(g2,g2) = 1.5
    c: DistanceX(g2,g0) = 233
FEATURE [PartDesign::Pad] Pad026
  Direction = (-0.390731,0.920505,-2e-16)
  Length = 300
  Length2 = 10
  Midplane = true
  Profile = -> Sketch064
  ReferenceAxis = -> Sketch064 [N_Axis]
  Type = 0
FEATURE [PartDesign::LinearPattern] LinearPattern001
  BaseFeature = -> Pad026
  Direction = -> Sketch064 [H_Axis]
  Length = 240
  Occurrences = 15
  Originals = -> [Pad026]
FEATURE [PartDesign::Plane] DatumPlane041
  AttachmentOffset = pos=(0,0,0) rot=(0,-1,0;0.122173rad)
  Length = 798.614
  MapMode = 5
  Placement = pos=(0,0,0) rot=(0.624332,0.552363,0.552363;2.02535rad)
  ResizeMode = 0
  Support = -> [YZ_Plane035]
  Width = 729.681
FEATURE [Sketcher::SketchObject] Sketch065
  ExternalGeometry = -> [Pad024]
  FullyConstrained = true
  MapMode = 5
  Placement = pos=(0,0,0) rot=(0.624332,0.552363,0.552363;2.02535rad)
  Support = -> [DatumPlane041]
  sketch-geometry (5):
    g0: LineSegment StartX=0 StartY=3 StartZ=0 EndX=-1.5 EndY=3 EndZ=0
    g1: LineSegment StartX=-1.5 StartY=3 StartZ=0 EndX=-1.5 EndY=4.5 EndZ=0
    g2: LineSegment StartX=-1.5 StartY=4.5 StartZ=0 EndX=0 EndY=4.5 EndZ=0
    g3: LineSegment StartX=0 StartY=4.5 StartZ=0 EndX=0 EndY=3 EndZ=0
    g4: LineSegment StartX=-161.171 StartY=3 StartZ=0 EndX=-13.8774 EndY=3 EndZ=0
  constraints (14):
    c: Coincident(g0,g1)
    c: Coincident(g1,g2)
    c: Coincident(g2,g3)
    c: Coincident(g3,g0)
    c: Horizontal(g0)
    c: Horizontal(g2)
    c: Vertical(g1)
    c: Vertical(g3)
    c: DistanceX(g2,g2) = 1.5
    c: DistanceY(g1,g1) = 1.5
    c: DistanceX(g0,g-1) = 0
    c: Coincident(g4,g-3)
    c: Coincident(g4,g-4)
    c: PointOnObject(g0,g4)
FEATURE [PartDesign::Pad] Pad027
  BaseFeature = -> Pad026
  Direction = (0.992546,-0.121869,2e-16)
  Length = 300
  Length2 = 10
  Profile = -> Sketch065
  ReferenceAxis = -> Sketch065 [N_Axis]
  Type = 0
FEATURE [PartDesign::LinearPattern] LinearPattern002
  BaseFeature = -> Pad027
  Direction = -> Sketch065 [H_Axis]
  Length = 144
  Occurrences = 10
  Originals = -> [Pad027]
  Reversed = true
FEATURE [Surface::GeomFillSurface] Surface043
  BoundaryList = -> [Compound003]
  FillType = 0
FEATURE [Part::FeaturePython] Solid002  label="LowPolyLowerInsideCase"  # WARN: FeaturePython — macro-defined, semantics opaque (R4)
  Faces = -> [Surface043,Surface025,Surface024,Surface027,Surface022,Surface030]
  ShapeStatus = Solid
FEATURE [Part::Fuse] Fusion001
  Base = -> LinearPattern
  Tool = -> LinearPattern001
FEATURE [Part::Fuse] Fusion002
  Base = -> Fusion001
  Tool = -> LinearPattern002
FEATURE [Part::Common] Common
  Base = -> Fusion002
  Tool = -> Solid002
FEATURE [App::Part] Part001  label="CaseBottom"
  Group = -> [Body017,Body031,BaseFeature,Body032,Surface012,Surface017,Compound002,Compound003,Surface013,Surface015,Surface019,Surface018,Surface016,Compound004,Surface014,BaseFeature001,Compound006,Line034,Line035,Line037,Line036,Line033,Line032,Solid001,Line049,Line051,Line052,Line053,Line055,Line054,Line050,SplitCurve,Line060,DatumPlane018,Surface011,Surface026,Surface029,Surface025,Surface022,Surface023,+122 more]
  Origin = -> Origin018
FEATURE [Part::Part2DObjectPython] Shape2DView004  # Draft 2D object (typed FeaturePython)
  AutoUpdate = true
  Base = -> Part001
  Clip = false
  FuseArch = false
  HiddenLines = false
  InPlace = true
  OnlySolids = false
  Placement = pos=(0,-183,0) rot=(0,0,1;0rad)
  Projection = (0,0,1)
  ProjectionMode = 0
  SegmentLength = 0.05
  Tessellation = false
  VisibleOnly = false
FEATURE [Part::Part2DObjectPython] Shape2DView005  # Draft 2D object (typed FeaturePython)
  AutoUpdate = true
  Base = -> Part001
  Clip = false
  FuseArch = false
  HiddenLines = false
  InPlace = true
  OnlySolids = false
  Placement = pos=(-2.8e-14,-411,0) rot=(0,0,-1;1.5708rad)
  Projection = (0,-1,0)
  ProjectionMode = 0
  SegmentLength = 0.05
  Tessellation = false
  VisibleOnly = false
FEATURE [Part::Part2DObjectPython] Shape2DView006  # Draft 2D object (typed FeaturePython)
  AutoUpdate = true
  Base = -> Part001
  Clip = false
  FuseArch = false
  HiddenLines = false
  InPlace = true
  OnlySolids = false
  Placement = pos=(-6,-183,0) rot=(0,0,1;3.14159rad)
  Projection = (1,-1.19209e-07,1.68587e-07)
  ProjectionMode = 0
  SegmentLength = 0.05
  Tessellation = false
  VisibleOnly = false
FEATURE [Part::Part2DObjectPython] Shape2DView007  # Draft 2D object (typed FeaturePython)
  AutoUpdate = true
  Base = -> Part001
  Clip = false
  FuseArch = false
  HiddenLines = false
  InPlace = true
  OnlySolids = false
  Placement = pos=(-72,-183,0) rot=(0,0,1;0rad)
  Projection = (8.74228e-08,0,-1)
  ProjectionMode = 0
  SegmentLength = 0.05
  Tessellation = false
  VisibleOnly = false
FEATURE [Part::Compound] Compound007  label="BottomProjections"
  Links = -> [Shape2DView004,Shape2DView005,Shape2DView006,Shape2DView007]
FEATURE [Sketcher::SketchObject] Sketch066
  AttachmentOffset = pos=(0,0,0) rot=(1,0,0;1.74533rad)
  FullyConstrained = true
  MapMode = 4
  Placement = pos=(0,0,0) rot=(-0.086827,0.992433,-0.086827;4.70479rad)
  Support = -> [YZ_Plane039]
  sketch-geometry (4):
    g0: LineSegment StartX=0 StartY=0 StartZ=0 EndX=1.5 EndY=0 EndZ=0
    g1: LineSegment StartX=1.5 StartY=0 StartZ=0 EndX=1.5 EndY=1.5 EndZ=0
    g2: LineSegment StartX=1.5 StartY=1.5 StartZ=0 EndX=0 EndY=1.5 EndZ=0
    g3: LineSegment StartX=0 StartY=1.5 StartZ=0 EndX=0 EndY=0 EndZ=0
  constraints (11):
    c: Coincident(g0,g1)
    c: Coincident(g1,g2)
    c: Coincident(g2,g3)
    c: Coincident(g3,g0)
    c: Horizontal(g0)
    c: Horizontal(g2)
    c: Vertical(g1)
    c: Vertical(g3)
    c: Coincident(g0,g-1)
    c: Equal(g3,g2)
    c: DistanceX(g2,g2) = 1.5
FEATURE [PartDesign::Pad] Pad028
  Direction = (-0.984808,-0.173648,-2e-16)
  Length = 120
  Length2 = 10
  Placement = pos=(0,0,0) rot=(0.57735,0.57735,0.57735;2.0944rad)
  Profile = -> Sketch066
  ReferenceAxis = -> Sketch066 [N_Axis]
  Reversed = true
  Type = 0
FEATURE [Part::Part2DObjectPython] Clone2D  label="Sketch066 (2D)"  # Draft 2D object (typed FeaturePython)
  Fuse = false
  Objects = -> [Sketch066]
  Placement = pos=(40.062,-33.5132,7e-15) rot=(0.889126,0.323616,0.323616;1.68804rad)
  Scale = (1,1,1)
FEATURE [Part::Part2DObjectPython] Clone2D001  label="Sketch066 (2D)001"  # Draft 2D object (typed FeaturePython)
  Fuse = false
  Objects = -> [Sketch066]
  Placement = pos=(52.4403,-20.8873,0) rot=(0.970288,-0.171088,-0.171088;1.60095rad)
  Scale = (1,1,1)
FEATURE [PartDesign::Pad] Pad029
  BaseFeature = -> Pad028
  Direction = (0.642788,-0.766044,-1e-16)
  Length = 200
  Length2 = 10
  Placement = pos=(0,0,0) rot=(0.57735,0.57735,0.57735;2.0944rad)
  Profile = -> Clone2D
  ReferenceAxis = -> Clone2D [N_Axis]
  Reversed = true
  Type = 0
FEATURE [PartDesign::Pad] Pad030
  BaseFeature = -> Pad029
  Direction = (-0.34202,-0.939693,-1e-16)
  Length = 180
  Length2 = 10
  Placement = pos=(0,0,0) rot=(0.57735,0.57735,0.57735;2.0944rad)
  Profile = -> Clone2D001
  ReferenceAxis = -> Clone2D001 [N_Axis]
  Reversed = true
  Type = 0
FEATURE [PartDesign::LinearPattern] LinearPattern005
  BaseFeature = -> Pad030
  Direction = -> Clone2D001 [H_Axis]
  Length = 160
  Occurrences = 7
  Originals = -> [Pad030]
  Placement = pos=(0,0,0) rot=(0.57735,0.57735,0.57735;2.0944rad)
  Reversed = true
FEATURE [PartDesign::LinearPattern] LinearPattern006
  BaseFeature = -> LinearPattern005
  Direction = -> Sketch066 [V_Axis]
  Length = 150
  Occurrences = 7
  Originals = -> [Pad028]
  Placement = pos=(0,0,0) rot=(0.57735,0.57735,0.57735;2.0944rad)
FEATURE [PartDesign::LinearPattern] LinearPattern007
  BaseFeature = -> LinearPattern006
  Direction = -> Clone2D [H_Axis]
  Length = 140
  Occurrences = 6
  Originals = -> [Pad029]
  Placement = pos=(0,0,0) rot=(0.57735,0.57735,0.57735;2.0944rad)
FEATURE [PartDesign::Body] Body035  label="TopRigidity"
  Group = -> [Sketch066,Pad028,Clone2D,Clone2D001,Pad029,Pad030,LinearPattern005,LinearPattern006,LinearPattern007]
  Origin = -> Origin039
  Placement = pos=(5.05,-171,50) rot=(0,0,1;0rad)
  Tip = -> LinearPattern007
FEATURE [Part::Box] Box  label="StructureLimits"
  AttacherType = Attacher::AttachEngine3D
  Height = 2
  Length = 66
  Placement = pos=(6,-171,49.95) rot=(0,0,1;0rad)
  Width = 165.4
  expr: Width = <<Params>>.Width - 9
FEATURE [Part::MultiCommon] Common001  label="TopStructure"
  Placement = pos=(1.5,0,0) rot=(0,0,1;0rad)
  Shapes = -> [Body035,Box]
FEATURE [Part::Cut] Cut
  Base = -> Body
  Tool = -> Fusion
FEATURE [App::Part] Part  label="CaseTop"
  Group = -> [Body,Body003,Shape2DView,Shape2DView001,Shape2DView002,Shape2DView003,Compound001,Projection_Object,Projection_Object001,Sketch020,Pad010,ShapeBinder002,ShapeBinder001,Sketch021,Sketch022,Body024,Body020,Body027,Body022,Body026,Surface040,Surface041,Surface032,Line043,Line042,Line038,Solid,Body030,Body025,Compound,Line044,Line045,Body029,Body023,Body021,Body028,Line047,Line,Line046,Line048,+32 more]
  Origin = -> Origin003
  Placement = pos=(-3,0,0) rot=(0,0,1;0rad)
FEATURE [Mesh::Feature] Mesh001  label="CaseTop (Meshed)"
FEATURE [Mesh::Feature] Mesh  label="CaseBottom (Meshed)"
